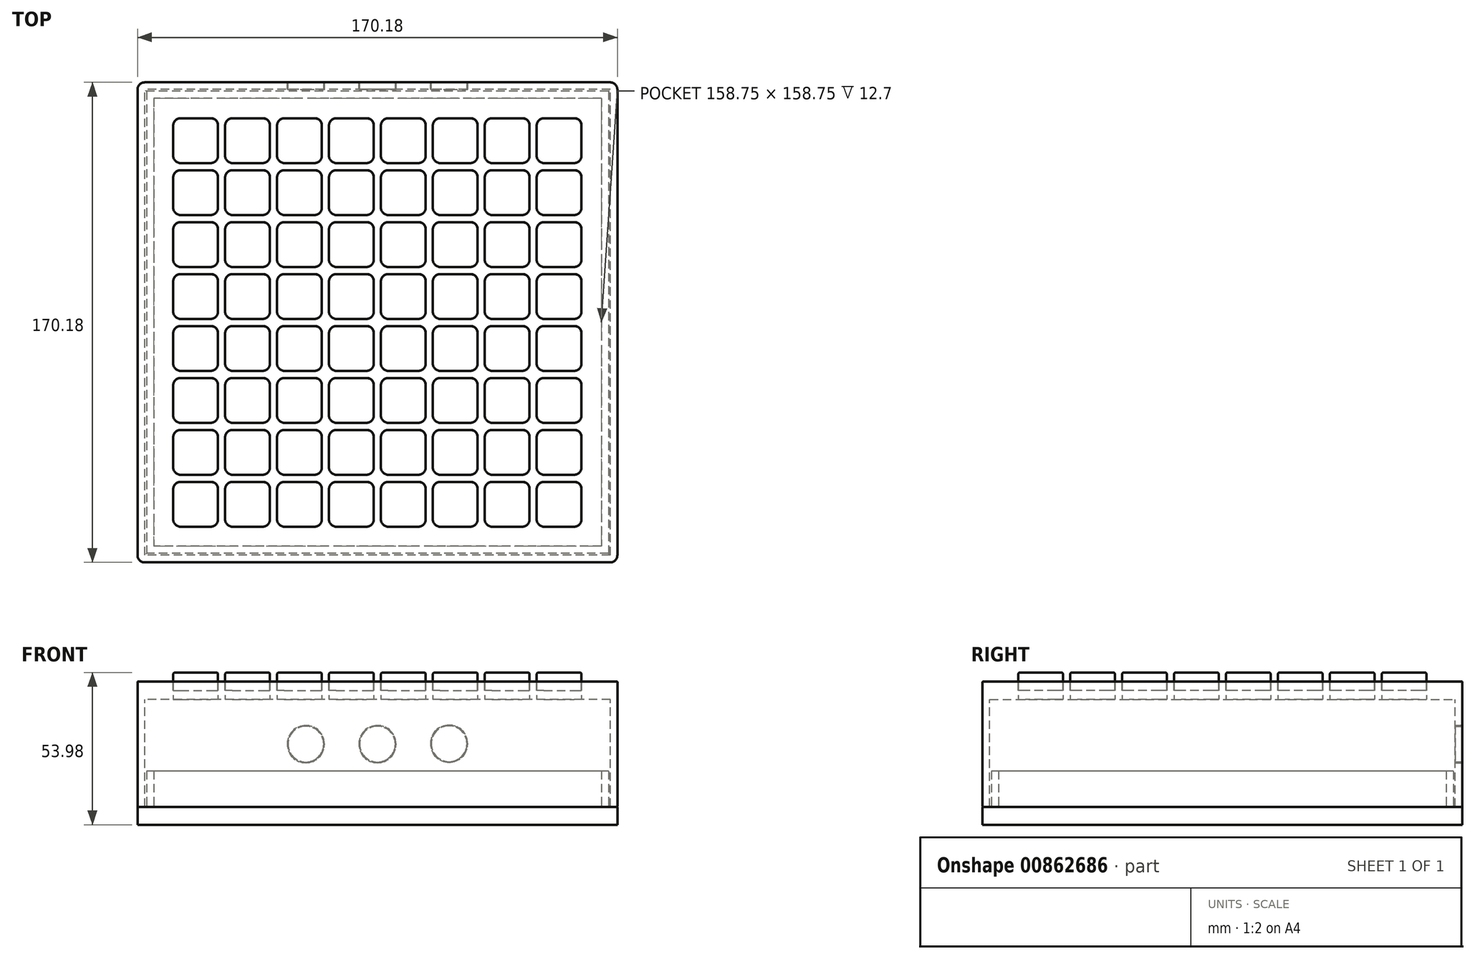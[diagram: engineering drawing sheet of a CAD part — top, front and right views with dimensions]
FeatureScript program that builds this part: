
annotation { "Feature Type Name" : "Feature", "Feature Type Description" : "" }
export const myFeature = defineFeature(function(context is Context, id is Id, definition is map)
    precondition{}
    {
        {
            var Q0;
            Q0=qCreatedBy(makeId("Top.planeOp"),FACE);
            var sketch = newSketch(context, id + "F0", { "sketchPlane" : qUnion([Q0])});
            skLineSegment(sketch, "E0.bottom", {"start": v(82.55, 85.1) * mm, "end": v(-82.55, 85.1) * mm});
            skLineSegment(sketch, "E0.top", {"start": v(82.55, -85.1) * mm, "end": v(-82.55, -85.1) * mm});
            skLineSegment(sketch, "E0.left", {"start": v(85.1, 82.55) * mm, "end": v(85.09, -82.55) * mm});
            skLineSegment(sketch, "E0.right", {"start": v(-85.1, 82.55) * mm, "end": v(-85.1, -82.55) * mm});
            skPoint(sketch, "E0.middle", {"position": v(0, 0) * mm});
            skPoint(sketch, "E1.visualSharp", {"position": v(-85.09, 85.1) * mm});
            skArc(sketch, "E1.filletArc", {"start": v(-82.55, 85.1) * mm, "mid": v(-84.35, 84.35) * mm, "end": v(-85.1, 82.55) * mm});
            skPoint(sketch, "E2.visualSharp", {"position": v(85.1, 85.1) * mm});
            skArc(sketch, "E2.filletArc", {"start": v(85.1, 82.55) * mm, "mid": v(84.35, 84.35) * mm, "end": v(82.55, 85.1) * mm});
            skPoint(sketch, "E3.visualSharp", {"position": v(85.09, -85.1) * mm});
            skArc(sketch, "E3.filletArc", {"start": v(82.55, -85.1) * mm, "mid": v(84.35, -84.35) * mm, "end": v(85.09, -82.55) * mm});
            skPoint(sketch, "E4.visualSharp", {"position": v(-85.1, -85.1) * mm});
            skArc(sketch, "E4.filletArc", {"start": v(-85.1, -82.55) * mm, "mid": v(-84.35, -84.35) * mm, "end": v(-82.55, -85.1) * mm});
            skLineSegment(sketch, "E5.bottom", {"start": v(-69.86, 72.38) * mm, "end": v(-59.07, 72.38) * mm});
            skLineSegment(sketch, "E5.top", {"start": v(-69.86, 56.5) * mm, "end": v(-59.07, 56.5) * mm});
            skLineSegment(sketch, "E5.left", {"start": v(-72.4, 69.84) * mm, "end": v(-72.4, 59.05) * mm});
            skLineSegment(sketch, "E5.right", {"start": v(-56.53, 69.84) * mm, "end": v(-56.53, 59.05) * mm});
            skPoint(sketch, "E6.visualSharp", {"position": v(-72.4, 72.38) * mm});
            skArc(sketch, "E6.filletArc", {"start": v(-69.86, 72.38) * mm, "mid": v(-71.66, 71.64) * mm, "end": v(-72.4, 69.84) * mm});
            skPoint(sketch, "E7.visualSharp", {"position": v(-56.53, 72.38) * mm});
            skArc(sketch, "E7.filletArc", {"start": v(-56.53, 69.84) * mm, "mid": v(-57.27, 71.64) * mm, "end": v(-59.07, 72.38) * mm});
            skPoint(sketch, "E8.visualSharp", {"position": v(-56.53, 56.5) * mm});
            skArc(sketch, "E8.filletArc", {"start": v(-59.07, 56.5) * mm, "mid": v(-57.27, 57.25) * mm, "end": v(-56.53, 59.05) * mm});
            skPoint(sketch, "E9.visualSharp", {"position": v(-72.4, 56.5) * mm});
            skArc(sketch, "E9.filletArc", {"start": v(-72.4, 59.05) * mm, "mid": v(-71.66, 57.25) * mm, "end": v(-69.86, 56.5) * mm});
            skLineSegment(sketch, "E10.0.1.0", {"start": v(-69.86, 53.97) * mm, "end": v(-59.07, 53.97) * mm});
            skArc(sketch, "E10.0.1.1", {"start": v(-56.53, 51.43) * mm, "mid": v(-57.27, 53.22) * mm, "end": v(-59.07, 53.97) * mm});
            skLineSegment(sketch, "E10.0.1.2", {"start": v(-56.53, 51.43) * mm, "end": v(-56.53, 40.63) * mm});
            skArc(sketch, "E10.0.1.3", {"start": v(-59.07, 38.1) * mm, "mid": v(-57.27, 38.84) * mm, "end": v(-56.53, 40.63) * mm});
            skLineSegment(sketch, "E10.0.1.4", {"start": v(-69.86, 38.1) * mm, "end": v(-59.07, 38.1) * mm});
            skArc(sketch, "E10.0.1.5", {"start": v(-72.4, 40.63) * mm, "mid": v(-71.66, 38.84) * mm, "end": v(-69.86, 38.1) * mm});
            skLineSegment(sketch, "E10.0.1.6", {"start": v(-72.4, 51.43) * mm, "end": v(-72.4, 40.63) * mm});
            skArc(sketch, "E10.0.1.7", {"start": v(-69.86, 53.97) * mm, "mid": v(-71.66, 53.22) * mm, "end": v(-72.4, 51.43) * mm});
            skLineSegment(sketch, "E10.0.2.0", {"start": v(-69.86, 35.55) * mm, "end": v(-59.07, 35.55) * mm});
            skArc(sketch, "E10.0.2.1", {"start": v(-56.53, 33.01) * mm, "mid": v(-57.27, 34.8) * mm, "end": v(-59.07, 35.55) * mm});
            skLineSegment(sketch, "E10.0.2.2", {"start": v(-56.53, 33.01) * mm, "end": v(-56.53, 22.22) * mm});
            skArc(sketch, "E10.0.2.3", {"start": v(-59.07, 19.68) * mm, "mid": v(-57.27, 20.42) * mm, "end": v(-56.53, 22.22) * mm});
            skLineSegment(sketch, "E10.0.2.4", {"start": v(-69.86, 19.68) * mm, "end": v(-59.07, 19.68) * mm});
            skArc(sketch, "E10.0.2.5", {"start": v(-72.4, 22.22) * mm, "mid": v(-71.66, 20.42) * mm, "end": v(-69.86, 19.68) * mm});
            skLineSegment(sketch, "E10.0.2.6", {"start": v(-72.4, 33.01) * mm, "end": v(-72.4, 22.22) * mm});
            skArc(sketch, "E10.0.2.7", {"start": v(-69.86, 35.55) * mm, "mid": v(-71.66, 34.8) * mm, "end": v(-72.4, 33.01) * mm});
            skLineSegment(sketch, "E10.0.3.0", {"start": v(-69.86, 17.14) * mm, "end": v(-59.07, 17.14) * mm});
            skArc(sketch, "E10.0.3.1", {"start": v(-56.53, 14.6) * mm, "mid": v(-57.27, 16.4) * mm, "end": v(-59.07, 17.14) * mm});
            skLineSegment(sketch, "E10.0.3.2", {"start": v(-56.53, 14.6) * mm, "end": v(-56.53, 3.8) * mm});
            skArc(sketch, "E10.0.3.3", {"start": v(-59.07, 1.26) * mm, "mid": v(-57.27, 2) * mm, "end": v(-56.53, 3.8) * mm});
            skLineSegment(sketch, "E10.0.3.4", {"start": v(-69.86, 1.26) * mm, "end": v(-59.07, 1.26) * mm});
            skArc(sketch, "E10.0.3.5", {"start": v(-72.4, 3.8) * mm, "mid": v(-71.66, 2) * mm, "end": v(-69.86, 1.26) * mm});
            skLineSegment(sketch, "E10.0.3.6", {"start": v(-72.4, 14.6) * mm, "end": v(-72.4, 3.8) * mm});
            skArc(sketch, "E10.0.3.7", {"start": v(-69.86, 17.14) * mm, "mid": v(-71.66, 16.4) * mm, "end": v(-72.4, 14.6) * mm});
            skLineSegment(sketch, "E10.0.4.0", {"start": v(-69.86, -1.28) * mm, "end": v(-59.07, -1.28) * mm});
            skArc(sketch, "E10.0.4.1", {"start": v(-56.53, -3.82) * mm, "mid": v(-57.27, -2.02) * mm, "end": v(-59.07, -1.28) * mm});
            skLineSegment(sketch, "E10.0.4.2", {"start": v(-56.53, -3.82) * mm, "end": v(-56.53, -14.61) * mm});
            skArc(sketch, "E10.0.4.3", {"start": v(-59.07, -17.15) * mm, "mid": v(-57.27, -16.4) * mm, "end": v(-56.53, -14.61) * mm});
            skLineSegment(sketch, "E10.0.4.4", {"start": v(-69.86, -17.15) * mm, "end": v(-59.07, -17.15) * mm});
            skArc(sketch, "E10.0.4.5", {"start": v(-72.4, -14.61) * mm, "mid": v(-71.66, -16.4) * mm, "end": v(-69.86, -17.15) * mm});
            skLineSegment(sketch, "E10.0.4.6", {"start": v(-72.4, -3.82) * mm, "end": v(-72.4, -14.61) * mm});
            skArc(sketch, "E10.0.4.7", {"start": v(-69.86, -1.28) * mm, "mid": v(-71.66, -2.02) * mm, "end": v(-72.4, -3.82) * mm});
            skLineSegment(sketch, "E10.0.5.0", {"start": v(-69.86, -19.7) * mm, "end": v(-59.07, -19.7) * mm});
            skArc(sketch, "E10.0.5.1", {"start": v(-56.53, -22.23) * mm, "mid": v(-57.27, -20.44) * mm, "end": v(-59.07, -19.7) * mm});
            skLineSegment(sketch, "E10.0.5.2", {"start": v(-56.53, -22.23) * mm, "end": v(-56.53, -33.03) * mm});
            skArc(sketch, "E10.0.5.3", {"start": v(-59.07, -35.57) * mm, "mid": v(-57.27, -34.82) * mm, "end": v(-56.53, -33.03) * mm});
            skLineSegment(sketch, "E10.0.5.4", {"start": v(-69.86, -35.57) * mm, "end": v(-59.07, -35.57) * mm});
            skArc(sketch, "E10.0.5.5", {"start": v(-72.4, -33.03) * mm, "mid": v(-71.66, -34.82) * mm, "end": v(-69.86, -35.57) * mm});
            skLineSegment(sketch, "E10.0.5.6", {"start": v(-72.4, -22.23) * mm, "end": v(-72.4, -33.03) * mm});
            skArc(sketch, "E10.0.5.7", {"start": v(-69.86, -19.7) * mm, "mid": v(-71.66, -20.44) * mm, "end": v(-72.4, -22.23) * mm});
            skLineSegment(sketch, "E10.0.6.0", {"start": v(-69.86, -38.1) * mm, "end": v(-59.07, -38.1) * mm});
            skArc(sketch, "E10.0.6.1", {"start": v(-56.53, -40.65) * mm, "mid": v(-57.27, -38.85) * mm, "end": v(-59.07, -38.1) * mm});
            skLineSegment(sketch, "E10.0.6.2", {"start": v(-56.53, -40.65) * mm, "end": v(-56.53, -51.44) * mm});
            skArc(sketch, "E10.0.6.3", {"start": v(-59.07, -53.98) * mm, "mid": v(-57.27, -53.24) * mm, "end": v(-56.53, -51.44) * mm});
            skLineSegment(sketch, "E10.0.6.4", {"start": v(-69.86, -53.98) * mm, "end": v(-59.07, -53.98) * mm});
            skArc(sketch, "E10.0.6.5", {"start": v(-72.4, -51.44) * mm, "mid": v(-71.66, -53.24) * mm, "end": v(-69.86, -53.98) * mm});
            skLineSegment(sketch, "E10.0.6.6", {"start": v(-72.4, -40.65) * mm, "end": v(-72.4, -51.44) * mm});
            skArc(sketch, "E10.0.6.7", {"start": v(-69.86, -38.1) * mm, "mid": v(-71.66, -38.85) * mm, "end": v(-72.4, -40.65) * mm});
            skLineSegment(sketch, "E10.0.7.0", {"start": v(-69.86, -56.52) * mm, "end": v(-59.07, -56.52) * mm});
            skArc(sketch, "E10.0.7.1", {"start": v(-56.53, -59.06) * mm, "mid": v(-57.27, -57.27) * mm, "end": v(-59.07, -56.52) * mm});
            skLineSegment(sketch, "E10.0.7.2", {"start": v(-56.53, -59.06) * mm, "end": v(-56.53, -69.86) * mm});
            skArc(sketch, "E10.0.7.3", {"start": v(-59.07, -72.4) * mm, "mid": v(-57.27, -71.65) * mm, "end": v(-56.53, -69.86) * mm});
            skLineSegment(sketch, "E10.0.7.4", {"start": v(-69.86, -72.4) * mm, "end": v(-59.07, -72.4) * mm});
            skArc(sketch, "E10.0.7.5", {"start": v(-72.4, -69.86) * mm, "mid": v(-71.66, -71.65) * mm, "end": v(-69.86, -72.4) * mm});
            skLineSegment(sketch, "E10.0.7.6", {"start": v(-72.4, -59.06) * mm, "end": v(-72.4, -69.86) * mm});
            skArc(sketch, "E10.0.7.7", {"start": v(-69.86, -56.52) * mm, "mid": v(-71.66, -57.27) * mm, "end": v(-72.4, -59.06) * mm});
            skLineSegment(sketch, "E10.1.0.0", {"start": v(-51.45, 72.38) * mm, "end": v(-40.65, 72.38) * mm});
            skArc(sketch, "E10.1.0.1", {"start": v(-38.11, 69.84) * mm, "mid": v(-38.85, 71.64) * mm, "end": v(-40.65, 72.38) * mm});
            skLineSegment(sketch, "E10.1.0.2", {"start": v(-38.11, 69.84) * mm, "end": v(-38.11, 59.05) * mm});
            skArc(sketch, "E10.1.0.3", {"start": v(-40.65, 56.5) * mm, "mid": v(-38.85, 57.25) * mm, "end": v(-38.11, 59.05) * mm});
            skLineSegment(sketch, "E10.1.0.4", {"start": v(-51.45, 56.5) * mm, "end": v(-40.65, 56.5) * mm});
            skArc(sketch, "E10.1.0.5", {"start": v(-53.99, 59.05) * mm, "mid": v(-53.24, 57.25) * mm, "end": v(-51.45, 56.5) * mm});
            skLineSegment(sketch, "E10.1.0.6", {"start": v(-53.99, 69.84) * mm, "end": v(-53.99, 59.05) * mm});
            skArc(sketch, "E10.1.0.7", {"start": v(-51.45, 72.38) * mm, "mid": v(-53.24, 71.64) * mm, "end": v(-53.99, 69.84) * mm});
            skLineSegment(sketch, "E10.1.1.0", {"start": v(-51.45, 53.97) * mm, "end": v(-40.65, 53.97) * mm});
            skArc(sketch, "E10.1.1.1", {"start": v(-38.11, 51.43) * mm, "mid": v(-38.85, 53.22) * mm, "end": v(-40.65, 53.97) * mm});
            skLineSegment(sketch, "E10.1.1.2", {"start": v(-38.11, 51.43) * mm, "end": v(-38.11, 40.63) * mm});
            skArc(sketch, "E10.1.1.3", {"start": v(-40.65, 38.1) * mm, "mid": v(-38.85, 38.84) * mm, "end": v(-38.11, 40.63) * mm});
            skLineSegment(sketch, "E10.1.1.4", {"start": v(-51.45, 38.1) * mm, "end": v(-40.65, 38.1) * mm});
            skArc(sketch, "E10.1.1.5", {"start": v(-53.99, 40.63) * mm, "mid": v(-53.24, 38.84) * mm, "end": v(-51.45, 38.1) * mm});
            skLineSegment(sketch, "E10.1.1.6", {"start": v(-53.99, 51.43) * mm, "end": v(-53.99, 40.63) * mm});
            skArc(sketch, "E10.1.1.7", {"start": v(-51.45, 53.97) * mm, "mid": v(-53.24, 53.22) * mm, "end": v(-53.99, 51.43) * mm});
            skLineSegment(sketch, "E10.1.2.0", {"start": v(-51.45, 35.55) * mm, "end": v(-40.65, 35.55) * mm});
            skArc(sketch, "E10.1.2.1", {"start": v(-38.11, 33.01) * mm, "mid": v(-38.85, 34.8) * mm, "end": v(-40.65, 35.55) * mm});
            skLineSegment(sketch, "E10.1.2.2", {"start": v(-38.11, 33.01) * mm, "end": v(-38.11, 22.22) * mm});
            skArc(sketch, "E10.1.2.3", {"start": v(-40.65, 19.68) * mm, "mid": v(-38.85, 20.42) * mm, "end": v(-38.11, 22.22) * mm});
            skLineSegment(sketch, "E10.1.2.4", {"start": v(-51.45, 19.68) * mm, "end": v(-40.65, 19.68) * mm});
            skArc(sketch, "E10.1.2.5", {"start": v(-53.99, 22.22) * mm, "mid": v(-53.24, 20.42) * mm, "end": v(-51.45, 19.68) * mm});
            skLineSegment(sketch, "E10.1.2.6", {"start": v(-53.99, 33.01) * mm, "end": v(-53.99, 22.22) * mm});
            skArc(sketch, "E10.1.2.7", {"start": v(-51.45, 35.55) * mm, "mid": v(-53.24, 34.8) * mm, "end": v(-53.99, 33.01) * mm});
            skLineSegment(sketch, "E10.1.3.0", {"start": v(-51.45, 17.14) * mm, "end": v(-40.65, 17.14) * mm});
            skArc(sketch, "E10.1.3.1", {"start": v(-38.11, 14.6) * mm, "mid": v(-38.85, 16.4) * mm, "end": v(-40.65, 17.14) * mm});
            skLineSegment(sketch, "E10.1.3.2", {"start": v(-38.11, 14.6) * mm, "end": v(-38.11, 3.8) * mm});
            skArc(sketch, "E10.1.3.3", {"start": v(-40.65, 1.26) * mm, "mid": v(-38.85, 2) * mm, "end": v(-38.11, 3.8) * mm});
            skLineSegment(sketch, "E10.1.3.4", {"start": v(-51.45, 1.26) * mm, "end": v(-40.65, 1.26) * mm});
            skArc(sketch, "E10.1.3.5", {"start": v(-53.99, 3.8) * mm, "mid": v(-53.24, 2) * mm, "end": v(-51.45, 1.26) * mm});
            skLineSegment(sketch, "E10.1.3.6", {"start": v(-53.99, 14.6) * mm, "end": v(-53.99, 3.8) * mm});
            skArc(sketch, "E10.1.3.7", {"start": v(-51.45, 17.14) * mm, "mid": v(-53.24, 16.4) * mm, "end": v(-53.99, 14.6) * mm});
            skLineSegment(sketch, "E10.1.4.0", {"start": v(-51.45, -1.28) * mm, "end": v(-40.65, -1.28) * mm});
            skArc(sketch, "E10.1.4.1", {"start": v(-38.11, -3.82) * mm, "mid": v(-38.85, -2.02) * mm, "end": v(-40.65, -1.28) * mm});
            skLineSegment(sketch, "E10.1.4.2", {"start": v(-38.11, -3.82) * mm, "end": v(-38.11, -14.61) * mm});
            skArc(sketch, "E10.1.4.3", {"start": v(-40.65, -17.15) * mm, "mid": v(-38.85, -16.4) * mm, "end": v(-38.11, -14.61) * mm});
            skLineSegment(sketch, "E10.1.4.4", {"start": v(-51.45, -17.15) * mm, "end": v(-40.65, -17.15) * mm});
            skArc(sketch, "E10.1.4.5", {"start": v(-53.99, -14.61) * mm, "mid": v(-53.24, -16.4) * mm, "end": v(-51.45, -17.15) * mm});
            skLineSegment(sketch, "E10.1.4.6", {"start": v(-53.99, -3.82) * mm, "end": v(-53.99, -14.61) * mm});
            skArc(sketch, "E10.1.4.7", {"start": v(-51.45, -1.28) * mm, "mid": v(-53.24, -2.02) * mm, "end": v(-53.99, -3.82) * mm});
            skLineSegment(sketch, "E10.1.5.0", {"start": v(-51.45, -19.7) * mm, "end": v(-40.65, -19.7) * mm});
            skArc(sketch, "E10.1.5.1", {"start": v(-38.11, -22.23) * mm, "mid": v(-38.85, -20.44) * mm, "end": v(-40.65, -19.7) * mm});
            skLineSegment(sketch, "E10.1.5.2", {"start": v(-38.11, -22.23) * mm, "end": v(-38.11, -33.03) * mm});
            skArc(sketch, "E10.1.5.3", {"start": v(-40.65, -35.57) * mm, "mid": v(-38.85, -34.82) * mm, "end": v(-38.11, -33.03) * mm});
            skLineSegment(sketch, "E10.1.5.4", {"start": v(-51.45, -35.57) * mm, "end": v(-40.65, -35.57) * mm});
            skArc(sketch, "E10.1.5.5", {"start": v(-53.99, -33.03) * mm, "mid": v(-53.24, -34.82) * mm, "end": v(-51.45, -35.57) * mm});
            skLineSegment(sketch, "E10.1.5.6", {"start": v(-53.99, -22.23) * mm, "end": v(-53.99, -33.03) * mm});
            skArc(sketch, "E10.1.5.7", {"start": v(-51.45, -19.7) * mm, "mid": v(-53.24, -20.44) * mm, "end": v(-53.99, -22.23) * mm});
            skLineSegment(sketch, "E10.1.6.0", {"start": v(-51.45, -38.1) * mm, "end": v(-40.65, -38.1) * mm});
            skArc(sketch, "E10.1.6.1", {"start": v(-38.11, -40.65) * mm, "mid": v(-38.85, -38.85) * mm, "end": v(-40.65, -38.1) * mm});
            skLineSegment(sketch, "E10.1.6.2", {"start": v(-38.11, -40.65) * mm, "end": v(-38.11, -51.44) * mm});
            skArc(sketch, "E10.1.6.3", {"start": v(-40.65, -53.98) * mm, "mid": v(-38.85, -53.24) * mm, "end": v(-38.11, -51.44) * mm});
            skLineSegment(sketch, "E10.1.6.4", {"start": v(-51.45, -53.98) * mm, "end": v(-40.65, -53.98) * mm});
            skArc(sketch, "E10.1.6.5", {"start": v(-53.99, -51.44) * mm, "mid": v(-53.24, -53.24) * mm, "end": v(-51.45, -53.98) * mm});
            skLineSegment(sketch, "E10.1.6.6", {"start": v(-53.99, -40.65) * mm, "end": v(-53.99, -51.44) * mm});
            skArc(sketch, "E10.1.6.7", {"start": v(-51.45, -38.1) * mm, "mid": v(-53.24, -38.85) * mm, "end": v(-53.99, -40.65) * mm});
            skLineSegment(sketch, "E10.1.7.0", {"start": v(-51.45, -56.52) * mm, "end": v(-40.65, -56.52) * mm});
            skArc(sketch, "E10.1.7.1", {"start": v(-38.11, -59.06) * mm, "mid": v(-38.85, -57.27) * mm, "end": v(-40.65, -56.52) * mm});
            skLineSegment(sketch, "E10.1.7.2", {"start": v(-38.11, -59.06) * mm, "end": v(-38.11, -69.86) * mm});
            skArc(sketch, "E10.1.7.3", {"start": v(-40.65, -72.4) * mm, "mid": v(-38.85, -71.65) * mm, "end": v(-38.11, -69.86) * mm});
            skLineSegment(sketch, "E10.1.7.4", {"start": v(-51.45, -72.4) * mm, "end": v(-40.65, -72.4) * mm});
            skArc(sketch, "E10.1.7.5", {"start": v(-53.99, -69.86) * mm, "mid": v(-53.24, -71.65) * mm, "end": v(-51.45, -72.4) * mm});
            skLineSegment(sketch, "E10.1.7.6", {"start": v(-53.99, -59.06) * mm, "end": v(-53.99, -69.86) * mm});
            skArc(sketch, "E10.1.7.7", {"start": v(-51.45, -56.52) * mm, "mid": v(-53.24, -57.27) * mm, "end": v(-53.99, -59.06) * mm});
            skLineSegment(sketch, "E10.2.0.0", {"start": v(-33.03, 72.38) * mm, "end": v(-22.24, 72.38) * mm});
            skArc(sketch, "E10.2.0.1", {"start": v(-19.7, 69.84) * mm, "mid": v(-20.44, 71.64) * mm, "end": v(-22.24, 72.38) * mm});
            skLineSegment(sketch, "E10.2.0.2", {"start": v(-19.7, 69.84) * mm, "end": v(-19.7, 59.05) * mm});
            skArc(sketch, "E10.2.0.3", {"start": v(-22.24, 56.5) * mm, "mid": v(-20.44, 57.25) * mm, "end": v(-19.7, 59.05) * mm});
            skLineSegment(sketch, "E10.2.0.4", {"start": v(-33.03, 56.5) * mm, "end": v(-22.24, 56.5) * mm});
            skArc(sketch, "E10.2.0.5", {"start": v(-35.57, 59.05) * mm, "mid": v(-34.83, 57.25) * mm, "end": v(-33.03, 56.5) * mm});
            skLineSegment(sketch, "E10.2.0.6", {"start": v(-35.57, 69.84) * mm, "end": v(-35.57, 59.05) * mm});
            skArc(sketch, "E10.2.0.7", {"start": v(-33.03, 72.38) * mm, "mid": v(-34.83, 71.64) * mm, "end": v(-35.57, 69.84) * mm});
            skLineSegment(sketch, "E10.2.1.0", {"start": v(-33.03, 53.97) * mm, "end": v(-22.24, 53.97) * mm});
            skArc(sketch, "E10.2.1.1", {"start": v(-19.7, 51.43) * mm, "mid": v(-20.44, 53.22) * mm, "end": v(-22.24, 53.97) * mm});
            skLineSegment(sketch, "E10.2.1.2", {"start": v(-19.7, 51.43) * mm, "end": v(-19.7, 40.63) * mm});
            skArc(sketch, "E10.2.1.3", {"start": v(-22.24, 38.1) * mm, "mid": v(-20.44, 38.84) * mm, "end": v(-19.7, 40.63) * mm});
            skLineSegment(sketch, "E10.2.1.4", {"start": v(-33.03, 38.1) * mm, "end": v(-22.24, 38.1) * mm});
            skArc(sketch, "E10.2.1.5", {"start": v(-35.57, 40.63) * mm, "mid": v(-34.83, 38.84) * mm, "end": v(-33.03, 38.1) * mm});
            skLineSegment(sketch, "E10.2.1.6", {"start": v(-35.57, 51.43) * mm, "end": v(-35.57, 40.63) * mm});
            skArc(sketch, "E10.2.1.7", {"start": v(-33.03, 53.97) * mm, "mid": v(-34.83, 53.22) * mm, "end": v(-35.57, 51.43) * mm});
            skLineSegment(sketch, "E10.2.2.0", {"start": v(-33.03, 35.55) * mm, "end": v(-22.24, 35.55) * mm});
            skArc(sketch, "E10.2.2.1", {"start": v(-19.7, 33.01) * mm, "mid": v(-20.44, 34.8) * mm, "end": v(-22.24, 35.55) * mm});
            skLineSegment(sketch, "E10.2.2.2", {"start": v(-19.7, 33.01) * mm, "end": v(-19.7, 22.22) * mm});
            skArc(sketch, "E10.2.2.3", {"start": v(-22.24, 19.68) * mm, "mid": v(-20.44, 20.42) * mm, "end": v(-19.7, 22.22) * mm});
            skLineSegment(sketch, "E10.2.2.4", {"start": v(-33.03, 19.68) * mm, "end": v(-22.24, 19.68) * mm});
            skArc(sketch, "E10.2.2.5", {"start": v(-35.57, 22.22) * mm, "mid": v(-34.83, 20.42) * mm, "end": v(-33.03, 19.68) * mm});
            skLineSegment(sketch, "E10.2.2.6", {"start": v(-35.57, 33.01) * mm, "end": v(-35.57, 22.22) * mm});
            skArc(sketch, "E10.2.2.7", {"start": v(-33.03, 35.55) * mm, "mid": v(-34.83, 34.8) * mm, "end": v(-35.57, 33.01) * mm});
            skLineSegment(sketch, "E10.2.3.0", {"start": v(-33.03, 17.14) * mm, "end": v(-22.24, 17.14) * mm});
            skArc(sketch, "E10.2.3.1", {"start": v(-19.7, 14.6) * mm, "mid": v(-20.44, 16.4) * mm, "end": v(-22.24, 17.14) * mm});
            skLineSegment(sketch, "E10.2.3.2", {"start": v(-19.7, 14.6) * mm, "end": v(-19.7, 3.8) * mm});
            skArc(sketch, "E10.2.3.3", {"start": v(-22.24, 1.26) * mm, "mid": v(-20.44, 2) * mm, "end": v(-19.7, 3.8) * mm});
            skLineSegment(sketch, "E10.2.3.4", {"start": v(-33.03, 1.26) * mm, "end": v(-22.24, 1.26) * mm});
            skArc(sketch, "E10.2.3.5", {"start": v(-35.57, 3.8) * mm, "mid": v(-34.83, 2) * mm, "end": v(-33.03, 1.26) * mm});
            skLineSegment(sketch, "E10.2.3.6", {"start": v(-35.57, 14.6) * mm, "end": v(-35.57, 3.8) * mm});
            skArc(sketch, "E10.2.3.7", {"start": v(-33.03, 17.14) * mm, "mid": v(-34.83, 16.4) * mm, "end": v(-35.57, 14.6) * mm});
            skLineSegment(sketch, "E10.2.4.0", {"start": v(-33.03, -1.28) * mm, "end": v(-22.24, -1.28) * mm});
            skArc(sketch, "E10.2.4.1", {"start": v(-19.7, -3.82) * mm, "mid": v(-20.44, -2.02) * mm, "end": v(-22.24, -1.28) * mm});
            skLineSegment(sketch, "E10.2.4.2", {"start": v(-19.7, -3.82) * mm, "end": v(-19.7, -14.61) * mm});
            skArc(sketch, "E10.2.4.3", {"start": v(-22.24, -17.15) * mm, "mid": v(-20.44, -16.4) * mm, "end": v(-19.7, -14.61) * mm});
            skLineSegment(sketch, "E10.2.4.4", {"start": v(-33.03, -17.15) * mm, "end": v(-22.24, -17.15) * mm});
            skArc(sketch, "E10.2.4.5", {"start": v(-35.57, -14.61) * mm, "mid": v(-34.83, -16.4) * mm, "end": v(-33.03, -17.15) * mm});
            skLineSegment(sketch, "E10.2.4.6", {"start": v(-35.57, -3.82) * mm, "end": v(-35.57, -14.61) * mm});
            skArc(sketch, "E10.2.4.7", {"start": v(-33.03, -1.28) * mm, "mid": v(-34.83, -2.02) * mm, "end": v(-35.57, -3.82) * mm});
            skLineSegment(sketch, "E10.2.5.0", {"start": v(-33.03, -19.7) * mm, "end": v(-22.24, -19.7) * mm});
            skArc(sketch, "E10.2.5.1", {"start": v(-19.7, -22.23) * mm, "mid": v(-20.44, -20.44) * mm, "end": v(-22.24, -19.7) * mm});
            skLineSegment(sketch, "E10.2.5.2", {"start": v(-19.7, -22.23) * mm, "end": v(-19.7, -33.03) * mm});
            skArc(sketch, "E10.2.5.3", {"start": v(-22.24, -35.57) * mm, "mid": v(-20.44, -34.82) * mm, "end": v(-19.7, -33.03) * mm});
            skLineSegment(sketch, "E10.2.5.4", {"start": v(-33.03, -35.57) * mm, "end": v(-22.24, -35.57) * mm});
            skArc(sketch, "E10.2.5.5", {"start": v(-35.57, -33.03) * mm, "mid": v(-34.83, -34.82) * mm, "end": v(-33.03, -35.57) * mm});
            skLineSegment(sketch, "E10.2.5.6", {"start": v(-35.57, -22.23) * mm, "end": v(-35.57, -33.03) * mm});
            skArc(sketch, "E10.2.5.7", {"start": v(-33.03, -19.7) * mm, "mid": v(-34.83, -20.44) * mm, "end": v(-35.57, -22.23) * mm});
            skLineSegment(sketch, "E10.2.6.0", {"start": v(-33.03, -38.1) * mm, "end": v(-22.24, -38.1) * mm});
            skArc(sketch, "E10.2.6.1", {"start": v(-19.7, -40.65) * mm, "mid": v(-20.44, -38.85) * mm, "end": v(-22.24, -38.1) * mm});
            skLineSegment(sketch, "E10.2.6.2", {"start": v(-19.7, -40.65) * mm, "end": v(-19.7, -51.44) * mm});
            skArc(sketch, "E10.2.6.3", {"start": v(-22.24, -53.98) * mm, "mid": v(-20.44, -53.24) * mm, "end": v(-19.7, -51.44) * mm});
            skLineSegment(sketch, "E10.2.6.4", {"start": v(-33.03, -53.98) * mm, "end": v(-22.24, -53.98) * mm});
            skArc(sketch, "E10.2.6.5", {"start": v(-35.57, -51.44) * mm, "mid": v(-34.83, -53.24) * mm, "end": v(-33.03, -53.98) * mm});
            skLineSegment(sketch, "E10.2.6.6", {"start": v(-35.57, -40.65) * mm, "end": v(-35.57, -51.44) * mm});
            skArc(sketch, "E10.2.6.7", {"start": v(-33.03, -38.1) * mm, "mid": v(-34.83, -38.85) * mm, "end": v(-35.57, -40.65) * mm});
            skLineSegment(sketch, "E10.2.7.0", {"start": v(-33.03, -56.52) * mm, "end": v(-22.24, -56.52) * mm});
            skArc(sketch, "E10.2.7.1", {"start": v(-19.7, -59.06) * mm, "mid": v(-20.44, -57.27) * mm, "end": v(-22.24, -56.52) * mm});
            skLineSegment(sketch, "E10.2.7.2", {"start": v(-19.7, -59.06) * mm, "end": v(-19.7, -69.86) * mm});
            skArc(sketch, "E10.2.7.3", {"start": v(-22.24, -72.4) * mm, "mid": v(-20.44, -71.65) * mm, "end": v(-19.7, -69.86) * mm});
            skLineSegment(sketch, "E10.2.7.4", {"start": v(-33.03, -72.4) * mm, "end": v(-22.24, -72.4) * mm});
            skArc(sketch, "E10.2.7.5", {"start": v(-35.57, -69.86) * mm, "mid": v(-34.83, -71.65) * mm, "end": v(-33.03, -72.4) * mm});
            skLineSegment(sketch, "E10.2.7.6", {"start": v(-35.57, -59.06) * mm, "end": v(-35.57, -69.86) * mm});
            skArc(sketch, "E10.2.7.7", {"start": v(-33.03, -56.52) * mm, "mid": v(-34.83, -57.27) * mm, "end": v(-35.57, -59.06) * mm});
            skLineSegment(sketch, "E10.3.0.0", {"start": v(-14.62, 72.38) * mm, "end": v(-3.82, 72.38) * mm});
            skArc(sketch, "E10.3.0.1", {"start": v(-1.28, 69.84) * mm, "mid": v(-2.02, 71.64) * mm, "end": v(-3.82, 72.38) * mm});
            skLineSegment(sketch, "E10.3.0.2", {"start": v(-1.28, 69.84) * mm, "end": v(-1.28, 59.05) * mm});
            skArc(sketch, "E10.3.0.3", {"start": v(-3.82, 56.5) * mm, "mid": v(-2.02, 57.25) * mm, "end": v(-1.28, 59.05) * mm});
            skLineSegment(sketch, "E10.3.0.4", {"start": v(-14.62, 56.5) * mm, "end": v(-3.82, 56.5) * mm});
            skArc(sketch, "E10.3.0.5", {"start": v(-17.16, 59.05) * mm, "mid": v(-16.41, 57.25) * mm, "end": v(-14.62, 56.5) * mm});
            skLineSegment(sketch, "E10.3.0.6", {"start": v(-17.16, 69.84) * mm, "end": v(-17.16, 59.05) * mm});
            skArc(sketch, "E10.3.0.7", {"start": v(-14.62, 72.38) * mm, "mid": v(-16.41, 71.64) * mm, "end": v(-17.16, 69.84) * mm});
            skLineSegment(sketch, "E10.3.1.0", {"start": v(-14.62, 53.97) * mm, "end": v(-3.82, 53.97) * mm});
            skArc(sketch, "E10.3.1.1", {"start": v(-1.28, 51.43) * mm, "mid": v(-2.02, 53.22) * mm, "end": v(-3.82, 53.97) * mm});
            skLineSegment(sketch, "E10.3.1.2", {"start": v(-1.28, 51.43) * mm, "end": v(-1.28, 40.63) * mm});
            skArc(sketch, "E10.3.1.3", {"start": v(-3.82, 38.1) * mm, "mid": v(-2.02, 38.84) * mm, "end": v(-1.28, 40.63) * mm});
            skLineSegment(sketch, "E10.3.1.4", {"start": v(-14.62, 38.1) * mm, "end": v(-3.82, 38.1) * mm});
            skArc(sketch, "E10.3.1.5", {"start": v(-17.16, 40.63) * mm, "mid": v(-16.41, 38.84) * mm, "end": v(-14.62, 38.1) * mm});
            skLineSegment(sketch, "E10.3.1.6", {"start": v(-17.16, 51.43) * mm, "end": v(-17.16, 40.63) * mm});
            skArc(sketch, "E10.3.1.7", {"start": v(-14.62, 53.97) * mm, "mid": v(-16.41, 53.22) * mm, "end": v(-17.16, 51.43) * mm});
            skLineSegment(sketch, "E10.3.2.0", {"start": v(-14.62, 35.55) * mm, "end": v(-3.82, 35.55) * mm});
            skArc(sketch, "E10.3.2.1", {"start": v(-1.28, 33.01) * mm, "mid": v(-2.02, 34.8) * mm, "end": v(-3.82, 35.55) * mm});
            skLineSegment(sketch, "E10.3.2.2", {"start": v(-1.28, 33.01) * mm, "end": v(-1.28, 22.22) * mm});
            skArc(sketch, "E10.3.2.3", {"start": v(-3.82, 19.68) * mm, "mid": v(-2.02, 20.42) * mm, "end": v(-1.28, 22.22) * mm});
            skLineSegment(sketch, "E10.3.2.4", {"start": v(-14.62, 19.68) * mm, "end": v(-3.82, 19.68) * mm});
            skArc(sketch, "E10.3.2.5", {"start": v(-17.16, 22.22) * mm, "mid": v(-16.41, 20.42) * mm, "end": v(-14.62, 19.68) * mm});
            skLineSegment(sketch, "E10.3.2.6", {"start": v(-17.16, 33.01) * mm, "end": v(-17.16, 22.22) * mm});
            skArc(sketch, "E10.3.2.7", {"start": v(-14.62, 35.55) * mm, "mid": v(-16.41, 34.8) * mm, "end": v(-17.16, 33.01) * mm});
            skLineSegment(sketch, "E10.3.3.0", {"start": v(-14.62, 17.14) * mm, "end": v(-3.82, 17.14) * mm});
            skArc(sketch, "E10.3.3.1", {"start": v(-1.28, 14.6) * mm, "mid": v(-2.02, 16.4) * mm, "end": v(-3.82, 17.14) * mm});
            skLineSegment(sketch, "E10.3.3.2", {"start": v(-1.28, 14.6) * mm, "end": v(-1.28, 3.8) * mm});
            skArc(sketch, "E10.3.3.3", {"start": v(-3.82, 1.26) * mm, "mid": v(-2.02, 2) * mm, "end": v(-1.28, 3.8) * mm});
            skLineSegment(sketch, "E10.3.3.4", {"start": v(-14.62, 1.26) * mm, "end": v(-3.82, 1.26) * mm});
            skArc(sketch, "E10.3.3.5", {"start": v(-17.16, 3.8) * mm, "mid": v(-16.41, 2) * mm, "end": v(-14.62, 1.26) * mm});
            skLineSegment(sketch, "E10.3.3.6", {"start": v(-17.16, 14.6) * mm, "end": v(-17.16, 3.8) * mm});
            skArc(sketch, "E10.3.3.7", {"start": v(-14.62, 17.14) * mm, "mid": v(-16.41, 16.4) * mm, "end": v(-17.16, 14.6) * mm});
            skLineSegment(sketch, "E10.3.4.0", {"start": v(-14.62, -1.28) * mm, "end": v(-3.82, -1.28) * mm});
            skArc(sketch, "E10.3.4.1", {"start": v(-1.28, -3.82) * mm, "mid": v(-2.02, -2.02) * mm, "end": v(-3.82, -1.28) * mm});
            skLineSegment(sketch, "E10.3.4.2", {"start": v(-1.28, -3.82) * mm, "end": v(-1.28, -14.61) * mm});
            skArc(sketch, "E10.3.4.3", {"start": v(-3.82, -17.15) * mm, "mid": v(-2.02, -16.4) * mm, "end": v(-1.28, -14.61) * mm});
            skLineSegment(sketch, "E10.3.4.4", {"start": v(-14.62, -17.15) * mm, "end": v(-3.82, -17.15) * mm});
            skArc(sketch, "E10.3.4.5", {"start": v(-17.16, -14.61) * mm, "mid": v(-16.41, -16.4) * mm, "end": v(-14.62, -17.15) * mm});
            skLineSegment(sketch, "E10.3.4.6", {"start": v(-17.16, -3.82) * mm, "end": v(-17.16, -14.61) * mm});
            skArc(sketch, "E10.3.4.7", {"start": v(-14.62, -1.28) * mm, "mid": v(-16.41, -2.02) * mm, "end": v(-17.16, -3.82) * mm});
            skLineSegment(sketch, "E10.3.5.0", {"start": v(-14.62, -19.7) * mm, "end": v(-3.82, -19.7) * mm});
            skArc(sketch, "E10.3.5.1", {"start": v(-1.28, -22.23) * mm, "mid": v(-2.02, -20.44) * mm, "end": v(-3.82, -19.7) * mm});
            skLineSegment(sketch, "E10.3.5.2", {"start": v(-1.28, -22.23) * mm, "end": v(-1.28, -33.03) * mm});
            skArc(sketch, "E10.3.5.3", {"start": v(-3.82, -35.57) * mm, "mid": v(-2.02, -34.82) * mm, "end": v(-1.28, -33.03) * mm});
            skLineSegment(sketch, "E10.3.5.4", {"start": v(-14.62, -35.57) * mm, "end": v(-3.82, -35.57) * mm});
            skArc(sketch, "E10.3.5.5", {"start": v(-17.16, -33.03) * mm, "mid": v(-16.41, -34.82) * mm, "end": v(-14.62, -35.57) * mm});
            skLineSegment(sketch, "E10.3.5.6", {"start": v(-17.16, -22.23) * mm, "end": v(-17.16, -33.03) * mm});
            skArc(sketch, "E10.3.5.7", {"start": v(-14.62, -19.7) * mm, "mid": v(-16.41, -20.44) * mm, "end": v(-17.16, -22.23) * mm});
            skLineSegment(sketch, "E10.3.6.0", {"start": v(-14.62, -38.1) * mm, "end": v(-3.82, -38.1) * mm});
            skArc(sketch, "E10.3.6.1", {"start": v(-1.28, -40.65) * mm, "mid": v(-2.02, -38.85) * mm, "end": v(-3.82, -38.1) * mm});
            skLineSegment(sketch, "E10.3.6.2", {"start": v(-1.28, -40.65) * mm, "end": v(-1.28, -51.44) * mm});
            skArc(sketch, "E10.3.6.3", {"start": v(-3.82, -53.98) * mm, "mid": v(-2.02, -53.24) * mm, "end": v(-1.28, -51.44) * mm});
            skLineSegment(sketch, "E10.3.6.4", {"start": v(-14.62, -53.98) * mm, "end": v(-3.82, -53.98) * mm});
            skArc(sketch, "E10.3.6.5", {"start": v(-17.16, -51.44) * mm, "mid": v(-16.41, -53.24) * mm, "end": v(-14.62, -53.98) * mm});
            skLineSegment(sketch, "E10.3.6.6", {"start": v(-17.16, -40.65) * mm, "end": v(-17.16, -51.44) * mm});
            skArc(sketch, "E10.3.6.7", {"start": v(-14.62, -38.1) * mm, "mid": v(-16.41, -38.85) * mm, "end": v(-17.16, -40.65) * mm});
            skLineSegment(sketch, "E10.3.7.0", {"start": v(-14.62, -56.52) * mm, "end": v(-3.82, -56.52) * mm});
            skArc(sketch, "E10.3.7.1", {"start": v(-1.28, -59.06) * mm, "mid": v(-2.02, -57.27) * mm, "end": v(-3.82, -56.52) * mm});
            skLineSegment(sketch, "E10.3.7.2", {"start": v(-1.28, -59.06) * mm, "end": v(-1.28, -69.86) * mm});
            skArc(sketch, "E10.3.7.3", {"start": v(-3.82, -72.4) * mm, "mid": v(-2.02, -71.65) * mm, "end": v(-1.28, -69.86) * mm});
            skLineSegment(sketch, "E10.3.7.4", {"start": v(-14.62, -72.4) * mm, "end": v(-3.82, -72.4) * mm});
            skArc(sketch, "E10.3.7.5", {"start": v(-17.16, -69.86) * mm, "mid": v(-16.41, -71.65) * mm, "end": v(-14.62, -72.4) * mm});
            skLineSegment(sketch, "E10.3.7.6", {"start": v(-17.16, -59.06) * mm, "end": v(-17.16, -69.86) * mm});
            skArc(sketch, "E10.3.7.7", {"start": v(-14.62, -56.52) * mm, "mid": v(-16.41, -57.27) * mm, "end": v(-17.16, -59.06) * mm});
            skLineSegment(sketch, "E10.4.0.0", {"start": v(3.8, 72.38) * mm, "end": v(14.6, 72.38) * mm});
            skArc(sketch, "E10.4.0.1", {"start": v(17.13, 69.84) * mm, "mid": v(16.4, 71.64) * mm, "end": v(14.6, 72.38) * mm});
            skLineSegment(sketch, "E10.4.0.2", {"start": v(17.13, 69.84) * mm, "end": v(17.13, 59.05) * mm});
            skArc(sketch, "E10.4.0.3", {"start": v(14.6, 56.5) * mm, "mid": v(16.4, 57.25) * mm, "end": v(17.13, 59.05) * mm});
            skLineSegment(sketch, "E10.4.0.4", {"start": v(3.8, 56.5) * mm, "end": v(14.6, 56.5) * mm});
            skArc(sketch, "E10.4.0.5", {"start": v(1.26, 59.05) * mm, "mid": v(2, 57.25) * mm, "end": v(3.8, 56.5) * mm});
            skLineSegment(sketch, "E10.4.0.6", {"start": v(1.26, 69.84) * mm, "end": v(1.26, 59.05) * mm});
            skArc(sketch, "E10.4.0.7", {"start": v(3.8, 72.38) * mm, "mid": v(2, 71.64) * mm, "end": v(1.26, 69.84) * mm});
            skLineSegment(sketch, "E10.4.1.0", {"start": v(3.8, 53.97) * mm, "end": v(14.6, 53.97) * mm});
            skArc(sketch, "E10.4.1.1", {"start": v(17.13, 51.43) * mm, "mid": v(16.4, 53.22) * mm, "end": v(14.6, 53.97) * mm});
            skLineSegment(sketch, "E10.4.1.2", {"start": v(17.13, 51.43) * mm, "end": v(17.13, 40.63) * mm});
            skArc(sketch, "E10.4.1.3", {"start": v(14.6, 38.1) * mm, "mid": v(16.4, 38.84) * mm, "end": v(17.13, 40.63) * mm});
            skLineSegment(sketch, "E10.4.1.4", {"start": v(3.8, 38.1) * mm, "end": v(14.6, 38.1) * mm});
            skArc(sketch, "E10.4.1.5", {"start": v(1.26, 40.63) * mm, "mid": v(2, 38.84) * mm, "end": v(3.8, 38.1) * mm});
            skLineSegment(sketch, "E10.4.1.6", {"start": v(1.26, 51.43) * mm, "end": v(1.26, 40.63) * mm});
            skArc(sketch, "E10.4.1.7", {"start": v(3.8, 53.97) * mm, "mid": v(2, 53.22) * mm, "end": v(1.26, 51.43) * mm});
            skLineSegment(sketch, "E10.4.2.0", {"start": v(3.8, 35.55) * mm, "end": v(14.6, 35.55) * mm});
            skArc(sketch, "E10.4.2.1", {"start": v(17.13, 33.01) * mm, "mid": v(16.4, 34.8) * mm, "end": v(14.6, 35.55) * mm});
            skLineSegment(sketch, "E10.4.2.2", {"start": v(17.13, 33.01) * mm, "end": v(17.13, 22.22) * mm});
            skArc(sketch, "E10.4.2.3", {"start": v(14.6, 19.68) * mm, "mid": v(16.4, 20.42) * mm, "end": v(17.13, 22.22) * mm});
            skLineSegment(sketch, "E10.4.2.4", {"start": v(3.8, 19.68) * mm, "end": v(14.6, 19.68) * mm});
            skArc(sketch, "E10.4.2.5", {"start": v(1.26, 22.22) * mm, "mid": v(2, 20.42) * mm, "end": v(3.8, 19.68) * mm});
            skLineSegment(sketch, "E10.4.2.6", {"start": v(1.26, 33.01) * mm, "end": v(1.26, 22.22) * mm});
            skArc(sketch, "E10.4.2.7", {"start": v(3.8, 35.55) * mm, "mid": v(2, 34.8) * mm, "end": v(1.26, 33.01) * mm});
            skLineSegment(sketch, "E10.4.3.0", {"start": v(3.8, 17.14) * mm, "end": v(14.6, 17.14) * mm});
            skArc(sketch, "E10.4.3.1", {"start": v(17.13, 14.6) * mm, "mid": v(16.4, 16.4) * mm, "end": v(14.6, 17.14) * mm});
            skLineSegment(sketch, "E10.4.3.2", {"start": v(17.13, 14.6) * mm, "end": v(17.13, 3.8) * mm});
            skArc(sketch, "E10.4.3.3", {"start": v(14.6, 1.26) * mm, "mid": v(16.4, 2) * mm, "end": v(17.13, 3.8) * mm});
            skLineSegment(sketch, "E10.4.3.4", {"start": v(3.8, 1.26) * mm, "end": v(14.6, 1.26) * mm});
            skArc(sketch, "E10.4.3.5", {"start": v(1.26, 3.8) * mm, "mid": v(2, 2) * mm, "end": v(3.8, 1.26) * mm});
            skLineSegment(sketch, "E10.4.3.6", {"start": v(1.26, 14.6) * mm, "end": v(1.26, 3.8) * mm});
            skArc(sketch, "E10.4.3.7", {"start": v(3.8, 17.14) * mm, "mid": v(2, 16.4) * mm, "end": v(1.26, 14.6) * mm});
            skLineSegment(sketch, "E10.4.4.0", {"start": v(3.8, -1.28) * mm, "end": v(14.6, -1.28) * mm});
            skArc(sketch, "E10.4.4.1", {"start": v(17.13, -3.82) * mm, "mid": v(16.4, -2.02) * mm, "end": v(14.6, -1.28) * mm});
            skLineSegment(sketch, "E10.4.4.2", {"start": v(17.13, -3.82) * mm, "end": v(17.13, -14.61) * mm});
            skArc(sketch, "E10.4.4.3", {"start": v(14.6, -17.15) * mm, "mid": v(16.4, -16.4) * mm, "end": v(17.13, -14.61) * mm});
            skLineSegment(sketch, "E10.4.4.4", {"start": v(3.8, -17.15) * mm, "end": v(14.6, -17.15) * mm});
            skArc(sketch, "E10.4.4.5", {"start": v(1.26, -14.61) * mm, "mid": v(2, -16.4) * mm, "end": v(3.8, -17.15) * mm});
            skLineSegment(sketch, "E10.4.4.6", {"start": v(1.26, -3.82) * mm, "end": v(1.26, -14.61) * mm});
            skArc(sketch, "E10.4.4.7", {"start": v(3.8, -1.28) * mm, "mid": v(2, -2.02) * mm, "end": v(1.26, -3.82) * mm});
            skLineSegment(sketch, "E10.4.5.0", {"start": v(3.8, -19.7) * mm, "end": v(14.6, -19.7) * mm});
            skArc(sketch, "E10.4.5.1", {"start": v(17.13, -22.23) * mm, "mid": v(16.4, -20.44) * mm, "end": v(14.6, -19.7) * mm});
            skLineSegment(sketch, "E10.4.5.2", {"start": v(17.13, -22.23) * mm, "end": v(17.13, -33.03) * mm});
            skArc(sketch, "E10.4.5.3", {"start": v(14.6, -35.57) * mm, "mid": v(16.4, -34.82) * mm, "end": v(17.13, -33.03) * mm});
            skLineSegment(sketch, "E10.4.5.4", {"start": v(3.8, -35.57) * mm, "end": v(14.6, -35.57) * mm});
            skArc(sketch, "E10.4.5.5", {"start": v(1.26, -33.03) * mm, "mid": v(2, -34.82) * mm, "end": v(3.8, -35.57) * mm});
            skLineSegment(sketch, "E10.4.5.6", {"start": v(1.26, -22.23) * mm, "end": v(1.26, -33.03) * mm});
            skArc(sketch, "E10.4.5.7", {"start": v(3.8, -19.7) * mm, "mid": v(2, -20.44) * mm, "end": v(1.26, -22.23) * mm});
            skLineSegment(sketch, "E10.4.6.0", {"start": v(3.8, -38.1) * mm, "end": v(14.6, -38.1) * mm});
            skArc(sketch, "E10.4.6.1", {"start": v(17.13, -40.65) * mm, "mid": v(16.4, -38.85) * mm, "end": v(14.6, -38.1) * mm});
            skLineSegment(sketch, "E10.4.6.2", {"start": v(17.13, -40.65) * mm, "end": v(17.13, -51.44) * mm});
            skArc(sketch, "E10.4.6.3", {"start": v(14.6, -53.98) * mm, "mid": v(16.4, -53.24) * mm, "end": v(17.13, -51.44) * mm});
            skLineSegment(sketch, "E10.4.6.4", {"start": v(3.8, -53.98) * mm, "end": v(14.6, -53.98) * mm});
            skArc(sketch, "E10.4.6.5", {"start": v(1.26, -51.44) * mm, "mid": v(2, -53.24) * mm, "end": v(3.8, -53.98) * mm});
            skLineSegment(sketch, "E10.4.6.6", {"start": v(1.26, -40.65) * mm, "end": v(1.26, -51.44) * mm});
            skArc(sketch, "E10.4.6.7", {"start": v(3.8, -38.1) * mm, "mid": v(2, -38.85) * mm, "end": v(1.26, -40.65) * mm});
            skLineSegment(sketch, "E10.4.7.0", {"start": v(3.8, -56.52) * mm, "end": v(14.6, -56.52) * mm});
            skArc(sketch, "E10.4.7.1", {"start": v(17.13, -59.06) * mm, "mid": v(16.4, -57.27) * mm, "end": v(14.6, -56.52) * mm});
            skLineSegment(sketch, "E10.4.7.2", {"start": v(17.13, -59.06) * mm, "end": v(17.13, -69.86) * mm});
            skArc(sketch, "E10.4.7.3", {"start": v(14.6, -72.4) * mm, "mid": v(16.4, -71.65) * mm, "end": v(17.13, -69.86) * mm});
            skLineSegment(sketch, "E10.4.7.4", {"start": v(3.8, -72.4) * mm, "end": v(14.6, -72.4) * mm});
            skArc(sketch, "E10.4.7.5", {"start": v(1.26, -69.86) * mm, "mid": v(2, -71.65) * mm, "end": v(3.8, -72.4) * mm});
            skLineSegment(sketch, "E10.4.7.6", {"start": v(1.26, -59.06) * mm, "end": v(1.26, -69.86) * mm});
            skArc(sketch, "E10.4.7.7", {"start": v(3.8, -56.52) * mm, "mid": v(2, -57.27) * mm, "end": v(1.26, -59.06) * mm});
            skLineSegment(sketch, "E10.5.0.0", {"start": v(22.21, 72.38) * mm, "end": v(33, 72.38) * mm});
            skArc(sketch, "E10.5.0.1", {"start": v(35.55, 69.84) * mm, "mid": v(34.8, 71.64) * mm, "end": v(33, 72.38) * mm});
            skLineSegment(sketch, "E10.5.0.2", {"start": v(35.55, 69.84) * mm, "end": v(35.55, 59.05) * mm});
            skArc(sketch, "E10.5.0.3", {"start": v(33, 56.5) * mm, "mid": v(34.8, 57.25) * mm, "end": v(35.55, 59.05) * mm});
            skLineSegment(sketch, "E10.5.0.4", {"start": v(22.21, 56.5) * mm, "end": v(33, 56.5) * mm});
            skArc(sketch, "E10.5.0.5", {"start": v(19.67, 59.05) * mm, "mid": v(20.42, 57.25) * mm, "end": v(22.21, 56.5) * mm});
            skLineSegment(sketch, "E10.5.0.6", {"start": v(19.67, 69.84) * mm, "end": v(19.67, 59.05) * mm});
            skArc(sketch, "E10.5.0.7", {"start": v(22.21, 72.38) * mm, "mid": v(20.42, 71.64) * mm, "end": v(19.67, 69.84) * mm});
            skLineSegment(sketch, "E10.5.1.0", {"start": v(22.21, 53.97) * mm, "end": v(33, 53.97) * mm});
            skArc(sketch, "E10.5.1.1", {"start": v(35.55, 51.43) * mm, "mid": v(34.8, 53.22) * mm, "end": v(33, 53.97) * mm});
            skLineSegment(sketch, "E10.5.1.2", {"start": v(35.55, 51.43) * mm, "end": v(35.55, 40.63) * mm});
            skArc(sketch, "E10.5.1.3", {"start": v(33, 38.1) * mm, "mid": v(34.8, 38.84) * mm, "end": v(35.55, 40.63) * mm});
            skLineSegment(sketch, "E10.5.1.4", {"start": v(22.21, 38.1) * mm, "end": v(33, 38.1) * mm});
            skArc(sketch, "E10.5.1.5", {"start": v(19.67, 40.63) * mm, "mid": v(20.42, 38.84) * mm, "end": v(22.21, 38.1) * mm});
            skLineSegment(sketch, "E10.5.1.6", {"start": v(19.67, 51.43) * mm, "end": v(19.67, 40.63) * mm});
            skArc(sketch, "E10.5.1.7", {"start": v(22.21, 53.97) * mm, "mid": v(20.42, 53.22) * mm, "end": v(19.67, 51.43) * mm});
            skLineSegment(sketch, "E10.5.2.0", {"start": v(22.21, 35.55) * mm, "end": v(33, 35.55) * mm});
            skArc(sketch, "E10.5.2.1", {"start": v(35.55, 33.01) * mm, "mid": v(34.8, 34.8) * mm, "end": v(33, 35.55) * mm});
            skLineSegment(sketch, "E10.5.2.2", {"start": v(35.55, 33.01) * mm, "end": v(35.55, 22.22) * mm});
            skArc(sketch, "E10.5.2.3", {"start": v(33, 19.68) * mm, "mid": v(34.8, 20.42) * mm, "end": v(35.55, 22.22) * mm});
            skLineSegment(sketch, "E10.5.2.4", {"start": v(22.21, 19.68) * mm, "end": v(33, 19.68) * mm});
            skArc(sketch, "E10.5.2.5", {"start": v(19.67, 22.22) * mm, "mid": v(20.42, 20.42) * mm, "end": v(22.21, 19.68) * mm});
            skLineSegment(sketch, "E10.5.2.6", {"start": v(19.67, 33.01) * mm, "end": v(19.67, 22.22) * mm});
            skArc(sketch, "E10.5.2.7", {"start": v(22.21, 35.55) * mm, "mid": v(20.42, 34.8) * mm, "end": v(19.67, 33.01) * mm});
            skLineSegment(sketch, "E10.5.3.0", {"start": v(22.21, 17.14) * mm, "end": v(33, 17.14) * mm});
            skArc(sketch, "E10.5.3.1", {"start": v(35.55, 14.6) * mm, "mid": v(34.8, 16.4) * mm, "end": v(33, 17.14) * mm});
            skLineSegment(sketch, "E10.5.3.2", {"start": v(35.55, 14.6) * mm, "end": v(35.55, 3.8) * mm});
            skArc(sketch, "E10.5.3.3", {"start": v(33, 1.26) * mm, "mid": v(34.8, 2) * mm, "end": v(35.55, 3.8) * mm});
            skLineSegment(sketch, "E10.5.3.4", {"start": v(22.21, 1.26) * mm, "end": v(33, 1.26) * mm});
            skArc(sketch, "E10.5.3.5", {"start": v(19.67, 3.8) * mm, "mid": v(20.42, 2) * mm, "end": v(22.21, 1.26) * mm});
            skLineSegment(sketch, "E10.5.3.6", {"start": v(19.67, 14.6) * mm, "end": v(19.67, 3.8) * mm});
            skArc(sketch, "E10.5.3.7", {"start": v(22.21, 17.14) * mm, "mid": v(20.42, 16.4) * mm, "end": v(19.67, 14.6) * mm});
            skLineSegment(sketch, "E10.5.4.0", {"start": v(22.21, -1.28) * mm, "end": v(33, -1.28) * mm});
            skArc(sketch, "E10.5.4.1", {"start": v(35.55, -3.82) * mm, "mid": v(34.8, -2.02) * mm, "end": v(33, -1.28) * mm});
            skLineSegment(sketch, "E10.5.4.2", {"start": v(35.55, -3.82) * mm, "end": v(35.55, -14.61) * mm});
            skArc(sketch, "E10.5.4.3", {"start": v(33, -17.15) * mm, "mid": v(34.8, -16.4) * mm, "end": v(35.55, -14.61) * mm});
            skLineSegment(sketch, "E10.5.4.4", {"start": v(22.21, -17.15) * mm, "end": v(33, -17.15) * mm});
            skArc(sketch, "E10.5.4.5", {"start": v(19.67, -14.61) * mm, "mid": v(20.42, -16.4) * mm, "end": v(22.21, -17.15) * mm});
            skLineSegment(sketch, "E10.5.4.6", {"start": v(19.67, -3.82) * mm, "end": v(19.67, -14.61) * mm});
            skArc(sketch, "E10.5.4.7", {"start": v(22.21, -1.28) * mm, "mid": v(20.42, -2.02) * mm, "end": v(19.67, -3.82) * mm});
            skLineSegment(sketch, "E10.5.5.0", {"start": v(22.21, -19.7) * mm, "end": v(33, -19.7) * mm});
            skArc(sketch, "E10.5.5.1", {"start": v(35.55, -22.23) * mm, "mid": v(34.8, -20.44) * mm, "end": v(33, -19.7) * mm});
            skLineSegment(sketch, "E10.5.5.2", {"start": v(35.55, -22.23) * mm, "end": v(35.55, -33.03) * mm});
            skArc(sketch, "E10.5.5.3", {"start": v(33, -35.57) * mm, "mid": v(34.8, -34.82) * mm, "end": v(35.55, -33.03) * mm});
            skLineSegment(sketch, "E10.5.5.4", {"start": v(22.21, -35.57) * mm, "end": v(33, -35.57) * mm});
            skArc(sketch, "E10.5.5.5", {"start": v(19.67, -33.03) * mm, "mid": v(20.42, -34.82) * mm, "end": v(22.21, -35.57) * mm});
            skLineSegment(sketch, "E10.5.5.6", {"start": v(19.67, -22.23) * mm, "end": v(19.67, -33.03) * mm});
            skArc(sketch, "E10.5.5.7", {"start": v(22.21, -19.7) * mm, "mid": v(20.42, -20.44) * mm, "end": v(19.67, -22.23) * mm});
            skLineSegment(sketch, "E10.5.6.0", {"start": v(22.21, -38.1) * mm, "end": v(33, -38.1) * mm});
            skArc(sketch, "E10.5.6.1", {"start": v(35.55, -40.65) * mm, "mid": v(34.8, -38.85) * mm, "end": v(33, -38.1) * mm});
            skLineSegment(sketch, "E10.5.6.2", {"start": v(35.55, -40.65) * mm, "end": v(35.55, -51.44) * mm});
            skArc(sketch, "E10.5.6.3", {"start": v(33, -53.98) * mm, "mid": v(34.8, -53.24) * mm, "end": v(35.55, -51.44) * mm});
            skLineSegment(sketch, "E10.5.6.4", {"start": v(22.21, -53.98) * mm, "end": v(33, -53.98) * mm});
            skArc(sketch, "E10.5.6.5", {"start": v(19.67, -51.44) * mm, "mid": v(20.42, -53.24) * mm, "end": v(22.21, -53.98) * mm});
            skLineSegment(sketch, "E10.5.6.6", {"start": v(19.67, -40.65) * mm, "end": v(19.67, -51.44) * mm});
            skArc(sketch, "E10.5.6.7", {"start": v(22.21, -38.1) * mm, "mid": v(20.42, -38.85) * mm, "end": v(19.67, -40.65) * mm});
            skLineSegment(sketch, "E10.5.7.0", {"start": v(22.21, -56.52) * mm, "end": v(33, -56.52) * mm});
            skArc(sketch, "E10.5.7.1", {"start": v(35.55, -59.06) * mm, "mid": v(34.8, -57.27) * mm, "end": v(33, -56.52) * mm});
            skLineSegment(sketch, "E10.5.7.2", {"start": v(35.55, -59.06) * mm, "end": v(35.55, -69.86) * mm});
            skArc(sketch, "E10.5.7.3", {"start": v(33, -72.4) * mm, "mid": v(34.8, -71.65) * mm, "end": v(35.55, -69.86) * mm});
            skLineSegment(sketch, "E10.5.7.4", {"start": v(22.21, -72.4) * mm, "end": v(33, -72.4) * mm});
            skArc(sketch, "E10.5.7.5", {"start": v(19.67, -69.86) * mm, "mid": v(20.42, -71.65) * mm, "end": v(22.21, -72.4) * mm});
            skLineSegment(sketch, "E10.5.7.6", {"start": v(19.67, -59.06) * mm, "end": v(19.67, -69.86) * mm});
            skArc(sketch, "E10.5.7.7", {"start": v(22.21, -56.52) * mm, "mid": v(20.42, -57.27) * mm, "end": v(19.67, -59.06) * mm});
            skLineSegment(sketch, "E10.6.0.0", {"start": v(40.63, 72.38) * mm, "end": v(51.42, 72.38) * mm});
            skArc(sketch, "E10.6.0.1", {"start": v(53.96, 69.84) * mm, "mid": v(53.22, 71.64) * mm, "end": v(51.42, 72.38) * mm});
            skLineSegment(sketch, "E10.6.0.2", {"start": v(53.96, 69.84) * mm, "end": v(53.96, 59.05) * mm});
            skArc(sketch, "E10.6.0.3", {"start": v(51.42, 56.5) * mm, "mid": v(53.22, 57.25) * mm, "end": v(53.96, 59.05) * mm});
            skLineSegment(sketch, "E10.6.0.4", {"start": v(40.63, 56.5) * mm, "end": v(51.42, 56.5) * mm});
            skArc(sketch, "E10.6.0.5", {"start": v(38.09, 59.05) * mm, "mid": v(38.83, 57.25) * mm, "end": v(40.63, 56.5) * mm});
            skLineSegment(sketch, "E10.6.0.6", {"start": v(38.09, 69.84) * mm, "end": v(38.09, 59.05) * mm});
            skArc(sketch, "E10.6.0.7", {"start": v(40.63, 72.38) * mm, "mid": v(38.83, 71.64) * mm, "end": v(38.09, 69.84) * mm});
            skLineSegment(sketch, "E10.6.1.0", {"start": v(40.63, 53.97) * mm, "end": v(51.42, 53.97) * mm});
            skArc(sketch, "E10.6.1.1", {"start": v(53.96, 51.43) * mm, "mid": v(53.22, 53.22) * mm, "end": v(51.42, 53.97) * mm});
            skLineSegment(sketch, "E10.6.1.2", {"start": v(53.96, 51.43) * mm, "end": v(53.96, 40.63) * mm});
            skArc(sketch, "E10.6.1.3", {"start": v(51.42, 38.1) * mm, "mid": v(53.22, 38.84) * mm, "end": v(53.96, 40.63) * mm});
            skLineSegment(sketch, "E10.6.1.4", {"start": v(40.63, 38.1) * mm, "end": v(51.42, 38.1) * mm});
            skArc(sketch, "E10.6.1.5", {"start": v(38.09, 40.63) * mm, "mid": v(38.83, 38.84) * mm, "end": v(40.63, 38.1) * mm});
            skLineSegment(sketch, "E10.6.1.6", {"start": v(38.09, 51.43) * mm, "end": v(38.09, 40.63) * mm});
            skArc(sketch, "E10.6.1.7", {"start": v(40.63, 53.97) * mm, "mid": v(38.83, 53.22) * mm, "end": v(38.09, 51.43) * mm});
            skLineSegment(sketch, "E10.6.2.0", {"start": v(40.63, 35.55) * mm, "end": v(51.42, 35.55) * mm});
            skArc(sketch, "E10.6.2.1", {"start": v(53.96, 33.01) * mm, "mid": v(53.22, 34.8) * mm, "end": v(51.42, 35.55) * mm});
            skLineSegment(sketch, "E10.6.2.2", {"start": v(53.96, 33.01) * mm, "end": v(53.96, 22.22) * mm});
            skArc(sketch, "E10.6.2.3", {"start": v(51.42, 19.68) * mm, "mid": v(53.22, 20.42) * mm, "end": v(53.96, 22.22) * mm});
            skLineSegment(sketch, "E10.6.2.4", {"start": v(40.63, 19.68) * mm, "end": v(51.42, 19.68) * mm});
            skArc(sketch, "E10.6.2.5", {"start": v(38.09, 22.22) * mm, "mid": v(38.83, 20.42) * mm, "end": v(40.63, 19.68) * mm});
            skLineSegment(sketch, "E10.6.2.6", {"start": v(38.09, 33.01) * mm, "end": v(38.09, 22.22) * mm});
            skArc(sketch, "E10.6.2.7", {"start": v(40.63, 35.55) * mm, "mid": v(38.83, 34.8) * mm, "end": v(38.09, 33.01) * mm});
            skLineSegment(sketch, "E10.6.3.0", {"start": v(40.63, 17.14) * mm, "end": v(51.42, 17.14) * mm});
            skArc(sketch, "E10.6.3.1", {"start": v(53.96, 14.6) * mm, "mid": v(53.22, 16.4) * mm, "end": v(51.42, 17.14) * mm});
            skLineSegment(sketch, "E10.6.3.2", {"start": v(53.96, 14.6) * mm, "end": v(53.96, 3.8) * mm});
            skArc(sketch, "E10.6.3.3", {"start": v(51.42, 1.26) * mm, "mid": v(53.22, 2) * mm, "end": v(53.96, 3.8) * mm});
            skLineSegment(sketch, "E10.6.3.4", {"start": v(40.63, 1.26) * mm, "end": v(51.42, 1.26) * mm});
            skArc(sketch, "E10.6.3.5", {"start": v(38.09, 3.8) * mm, "mid": v(38.83, 2) * mm, "end": v(40.63, 1.26) * mm});
            skLineSegment(sketch, "E10.6.3.6", {"start": v(38.09, 14.6) * mm, "end": v(38.09, 3.8) * mm});
            skArc(sketch, "E10.6.3.7", {"start": v(40.63, 17.14) * mm, "mid": v(38.83, 16.4) * mm, "end": v(38.09, 14.6) * mm});
            skLineSegment(sketch, "E10.6.4.0", {"start": v(40.63, -1.28) * mm, "end": v(51.42, -1.28) * mm});
            skArc(sketch, "E10.6.4.1", {"start": v(53.96, -3.82) * mm, "mid": v(53.22, -2.02) * mm, "end": v(51.42, -1.28) * mm});
            skLineSegment(sketch, "E10.6.4.2", {"start": v(53.96, -3.82) * mm, "end": v(53.96, -14.61) * mm});
            skArc(sketch, "E10.6.4.3", {"start": v(51.42, -17.15) * mm, "mid": v(53.22, -16.4) * mm, "end": v(53.96, -14.61) * mm});
            skLineSegment(sketch, "E10.6.4.4", {"start": v(40.63, -17.15) * mm, "end": v(51.42, -17.15) * mm});
            skArc(sketch, "E10.6.4.5", {"start": v(38.09, -14.61) * mm, "mid": v(38.83, -16.4) * mm, "end": v(40.63, -17.15) * mm});
            skLineSegment(sketch, "E10.6.4.6", {"start": v(38.09, -3.82) * mm, "end": v(38.09, -14.61) * mm});
            skArc(sketch, "E10.6.4.7", {"start": v(40.63, -1.28) * mm, "mid": v(38.83, -2.02) * mm, "end": v(38.09, -3.82) * mm});
            skLineSegment(sketch, "E10.6.5.0", {"start": v(40.63, -19.7) * mm, "end": v(51.42, -19.7) * mm});
            skArc(sketch, "E10.6.5.1", {"start": v(53.96, -22.23) * mm, "mid": v(53.22, -20.44) * mm, "end": v(51.42, -19.7) * mm});
            skLineSegment(sketch, "E10.6.5.2", {"start": v(53.96, -22.23) * mm, "end": v(53.96, -33.03) * mm});
            skArc(sketch, "E10.6.5.3", {"start": v(51.42, -35.57) * mm, "mid": v(53.22, -34.82) * mm, "end": v(53.96, -33.03) * mm});
            skLineSegment(sketch, "E10.6.5.4", {"start": v(40.63, -35.57) * mm, "end": v(51.42, -35.57) * mm});
            skArc(sketch, "E10.6.5.5", {"start": v(38.09, -33.03) * mm, "mid": v(38.83, -34.82) * mm, "end": v(40.63, -35.57) * mm});
            skLineSegment(sketch, "E10.6.5.6", {"start": v(38.09, -22.23) * mm, "end": v(38.09, -33.03) * mm});
            skArc(sketch, "E10.6.5.7", {"start": v(40.63, -19.7) * mm, "mid": v(38.83, -20.44) * mm, "end": v(38.09, -22.23) * mm});
            skLineSegment(sketch, "E10.6.6.0", {"start": v(40.63, -38.1) * mm, "end": v(51.42, -38.1) * mm});
            skArc(sketch, "E10.6.6.1", {"start": v(53.96, -40.65) * mm, "mid": v(53.22, -38.85) * mm, "end": v(51.42, -38.1) * mm});
            skLineSegment(sketch, "E10.6.6.2", {"start": v(53.96, -40.65) * mm, "end": v(53.96, -51.44) * mm});
            skArc(sketch, "E10.6.6.3", {"start": v(51.42, -53.98) * mm, "mid": v(53.22, -53.24) * mm, "end": v(53.96, -51.44) * mm});
            skLineSegment(sketch, "E10.6.6.4", {"start": v(40.63, -53.98) * mm, "end": v(51.42, -53.98) * mm});
            skArc(sketch, "E10.6.6.5", {"start": v(38.09, -51.44) * mm, "mid": v(38.83, -53.24) * mm, "end": v(40.63, -53.98) * mm});
            skLineSegment(sketch, "E10.6.6.6", {"start": v(38.09, -40.65) * mm, "end": v(38.09, -51.44) * mm});
            skArc(sketch, "E10.6.6.7", {"start": v(40.63, -38.1) * mm, "mid": v(38.83, -38.85) * mm, "end": v(38.09, -40.65) * mm});
            skLineSegment(sketch, "E10.6.7.0", {"start": v(40.63, -56.52) * mm, "end": v(51.42, -56.52) * mm});
            skArc(sketch, "E10.6.7.1", {"start": v(53.96, -59.06) * mm, "mid": v(53.22, -57.27) * mm, "end": v(51.42, -56.52) * mm});
            skLineSegment(sketch, "E10.6.7.2", {"start": v(53.96, -59.06) * mm, "end": v(53.96, -69.86) * mm});
            skArc(sketch, "E10.6.7.3", {"start": v(51.42, -72.4) * mm, "mid": v(53.22, -71.65) * mm, "end": v(53.96, -69.86) * mm});
            skLineSegment(sketch, "E10.6.7.4", {"start": v(40.63, -72.4) * mm, "end": v(51.42, -72.4) * mm});
            skArc(sketch, "E10.6.7.5", {"start": v(38.09, -69.86) * mm, "mid": v(38.83, -71.65) * mm, "end": v(40.63, -72.4) * mm});
            skLineSegment(sketch, "E10.6.7.6", {"start": v(38.09, -59.06) * mm, "end": v(38.09, -69.86) * mm});
            skArc(sketch, "E10.6.7.7", {"start": v(40.63, -56.52) * mm, "mid": v(38.83, -57.27) * mm, "end": v(38.09, -59.06) * mm});
            skLineSegment(sketch, "E10.7.0.0", {"start": v(59.04, 72.38) * mm, "end": v(69.84, 72.38) * mm});
            skArc(sketch, "E10.7.0.1", {"start": v(72.38, 69.84) * mm, "mid": v(71.64, 71.64) * mm, "end": v(69.84, 72.38) * mm});
            skLineSegment(sketch, "E10.7.0.2", {"start": v(72.38, 69.84) * mm, "end": v(72.38, 59.05) * mm});
            skArc(sketch, "E10.7.0.3", {"start": v(69.84, 56.5) * mm, "mid": v(71.64, 57.25) * mm, "end": v(72.38, 59.05) * mm});
            skLineSegment(sketch, "E10.7.0.4", {"start": v(59.04, 56.5) * mm, "end": v(69.84, 56.5) * mm});
            skArc(sketch, "E10.7.0.5", {"start": v(56.5, 59.05) * mm, "mid": v(57.25, 57.25) * mm, "end": v(59.04, 56.5) * mm});
            skLineSegment(sketch, "E10.7.0.6", {"start": v(56.5, 69.84) * mm, "end": v(56.5, 59.05) * mm});
            skArc(sketch, "E10.7.0.7", {"start": v(59.04, 72.38) * mm, "mid": v(57.25, 71.64) * mm, "end": v(56.5, 69.84) * mm});
            skLineSegment(sketch, "E10.7.1.0", {"start": v(59.04, 53.97) * mm, "end": v(69.84, 53.97) * mm});
            skArc(sketch, "E10.7.1.1", {"start": v(72.38, 51.43) * mm, "mid": v(71.64, 53.22) * mm, "end": v(69.84, 53.97) * mm});
            skLineSegment(sketch, "E10.7.1.2", {"start": v(72.38, 51.43) * mm, "end": v(72.38, 40.63) * mm});
            skArc(sketch, "E10.7.1.3", {"start": v(69.84, 38.1) * mm, "mid": v(71.64, 38.84) * mm, "end": v(72.38, 40.63) * mm});
            skLineSegment(sketch, "E10.7.1.4", {"start": v(59.04, 38.1) * mm, "end": v(69.84, 38.1) * mm});
            skArc(sketch, "E10.7.1.5", {"start": v(56.5, 40.63) * mm, "mid": v(57.25, 38.84) * mm, "end": v(59.04, 38.1) * mm});
            skLineSegment(sketch, "E10.7.1.6", {"start": v(56.5, 51.43) * mm, "end": v(56.5, 40.63) * mm});
            skArc(sketch, "E10.7.1.7", {"start": v(59.04, 53.97) * mm, "mid": v(57.25, 53.22) * mm, "end": v(56.5, 51.43) * mm});
            skLineSegment(sketch, "E10.7.2.0", {"start": v(59.04, 35.55) * mm, "end": v(69.84, 35.55) * mm});
            skArc(sketch, "E10.7.2.1", {"start": v(72.38, 33.01) * mm, "mid": v(71.64, 34.8) * mm, "end": v(69.84, 35.55) * mm});
            skLineSegment(sketch, "E10.7.2.2", {"start": v(72.38, 33.01) * mm, "end": v(72.38, 22.22) * mm});
            skArc(sketch, "E10.7.2.3", {"start": v(69.84, 19.68) * mm, "mid": v(71.64, 20.42) * mm, "end": v(72.38, 22.22) * mm});
            skLineSegment(sketch, "E10.7.2.4", {"start": v(59.04, 19.68) * mm, "end": v(69.84, 19.68) * mm});
            skArc(sketch, "E10.7.2.5", {"start": v(56.5, 22.22) * mm, "mid": v(57.25, 20.42) * mm, "end": v(59.04, 19.68) * mm});
            skLineSegment(sketch, "E10.7.2.6", {"start": v(56.5, 33.01) * mm, "end": v(56.5, 22.22) * mm});
            skArc(sketch, "E10.7.2.7", {"start": v(59.04, 35.55) * mm, "mid": v(57.25, 34.8) * mm, "end": v(56.5, 33.01) * mm});
            skLineSegment(sketch, "E10.7.3.0", {"start": v(59.04, 17.14) * mm, "end": v(69.84, 17.14) * mm});
            skArc(sketch, "E10.7.3.1", {"start": v(72.38, 14.6) * mm, "mid": v(71.64, 16.4) * mm, "end": v(69.84, 17.14) * mm});
            skLineSegment(sketch, "E10.7.3.2", {"start": v(72.38, 14.6) * mm, "end": v(72.38, 3.8) * mm});
            skArc(sketch, "E10.7.3.3", {"start": v(69.84, 1.26) * mm, "mid": v(71.64, 2) * mm, "end": v(72.38, 3.8) * mm});
            skLineSegment(sketch, "E10.7.3.4", {"start": v(59.04, 1.26) * mm, "end": v(69.84, 1.26) * mm});
            skArc(sketch, "E10.7.3.5", {"start": v(56.5, 3.8) * mm, "mid": v(57.25, 2) * mm, "end": v(59.04, 1.26) * mm});
            skLineSegment(sketch, "E10.7.3.6", {"start": v(56.5, 14.6) * mm, "end": v(56.5, 3.8) * mm});
            skArc(sketch, "E10.7.3.7", {"start": v(59.04, 17.14) * mm, "mid": v(57.25, 16.4) * mm, "end": v(56.5, 14.6) * mm});
            skLineSegment(sketch, "E10.7.4.0", {"start": v(59.04, -1.28) * mm, "end": v(69.84, -1.28) * mm});
            skArc(sketch, "E10.7.4.1", {"start": v(72.38, -3.82) * mm, "mid": v(71.64, -2.02) * mm, "end": v(69.84, -1.28) * mm});
            skLineSegment(sketch, "E10.7.4.2", {"start": v(72.38, -3.82) * mm, "end": v(72.38, -14.61) * mm});
            skArc(sketch, "E10.7.4.3", {"start": v(69.84, -17.15) * mm, "mid": v(71.64, -16.4) * mm, "end": v(72.38, -14.61) * mm});
            skLineSegment(sketch, "E10.7.4.4", {"start": v(59.04, -17.15) * mm, "end": v(69.84, -17.15) * mm});
            skArc(sketch, "E10.7.4.5", {"start": v(56.5, -14.61) * mm, "mid": v(57.25, -16.4) * mm, "end": v(59.04, -17.15) * mm});
            skLineSegment(sketch, "E10.7.4.6", {"start": v(56.5, -3.82) * mm, "end": v(56.5, -14.61) * mm});
            skArc(sketch, "E10.7.4.7", {"start": v(59.04, -1.28) * mm, "mid": v(57.25, -2.02) * mm, "end": v(56.5, -3.82) * mm});
            skLineSegment(sketch, "E10.7.5.0", {"start": v(59.04, -19.7) * mm, "end": v(69.84, -19.7) * mm});
            skArc(sketch, "E10.7.5.1", {"start": v(72.38, -22.23) * mm, "mid": v(71.64, -20.44) * mm, "end": v(69.84, -19.7) * mm});
            skLineSegment(sketch, "E10.7.5.2", {"start": v(72.38, -22.23) * mm, "end": v(72.38, -33.03) * mm});
            skArc(sketch, "E10.7.5.3", {"start": v(69.84, -35.57) * mm, "mid": v(71.64, -34.82) * mm, "end": v(72.38, -33.03) * mm});
            skLineSegment(sketch, "E10.7.5.4", {"start": v(59.04, -35.57) * mm, "end": v(69.84, -35.57) * mm});
            skArc(sketch, "E10.7.5.5", {"start": v(56.5, -33.03) * mm, "mid": v(57.25, -34.82) * mm, "end": v(59.04, -35.57) * mm});
            skLineSegment(sketch, "E10.7.5.6", {"start": v(56.5, -22.23) * mm, "end": v(56.5, -33.03) * mm});
            skArc(sketch, "E10.7.5.7", {"start": v(59.04, -19.7) * mm, "mid": v(57.25, -20.44) * mm, "end": v(56.5, -22.23) * mm});
            skLineSegment(sketch, "E10.7.6.0", {"start": v(59.04, -38.1) * mm, "end": v(69.84, -38.1) * mm});
            skArc(sketch, "E10.7.6.1", {"start": v(72.38, -40.65) * mm, "mid": v(71.64, -38.85) * mm, "end": v(69.84, -38.1) * mm});
            skLineSegment(sketch, "E10.7.6.2", {"start": v(72.38, -40.65) * mm, "end": v(72.38, -51.44) * mm});
            skArc(sketch, "E10.7.6.3", {"start": v(69.84, -53.98) * mm, "mid": v(71.64, -53.24) * mm, "end": v(72.38, -51.44) * mm});
            skLineSegment(sketch, "E10.7.6.4", {"start": v(59.04, -53.98) * mm, "end": v(69.84, -53.98) * mm});
            skArc(sketch, "E10.7.6.5", {"start": v(56.5, -51.44) * mm, "mid": v(57.25, -53.24) * mm, "end": v(59.04, -53.98) * mm});
            skLineSegment(sketch, "E10.7.6.6", {"start": v(56.5, -40.65) * mm, "end": v(56.5, -51.44) * mm});
            skArc(sketch, "E10.7.6.7", {"start": v(59.04, -38.1) * mm, "mid": v(57.25, -38.85) * mm, "end": v(56.5, -40.65) * mm});
            skLineSegment(sketch, "E10.7.7.0", {"start": v(59.04, -56.52) * mm, "end": v(69.84, -56.52) * mm});
            skArc(sketch, "E10.7.7.1", {"start": v(72.38, -59.06) * mm, "mid": v(71.64, -57.27) * mm, "end": v(69.84, -56.52) * mm});
            skLineSegment(sketch, "E10.7.7.2", {"start": v(72.38, -59.06) * mm, "end": v(72.38, -69.86) * mm});
            skArc(sketch, "E10.7.7.3", {"start": v(69.84, -72.4) * mm, "mid": v(71.64, -71.65) * mm, "end": v(72.38, -69.86) * mm});
            skLineSegment(sketch, "E10.7.7.4", {"start": v(59.04, -72.4) * mm, "end": v(69.84, -72.4) * mm});
            skArc(sketch, "E10.7.7.5", {"start": v(56.5, -69.86) * mm, "mid": v(57.25, -71.65) * mm, "end": v(59.04, -72.4) * mm});
            skLineSegment(sketch, "E10.7.7.6", {"start": v(56.5, -59.06) * mm, "end": v(56.5, -69.86) * mm});
            skArc(sketch, "E10.7.7.7", {"start": v(59.04, -56.52) * mm, "mid": v(57.25, -57.27) * mm, "end": v(56.5, -59.06) * mm});
            skLineSegment(sketch, "E10.direction1", {"start": v(-69.86, 72.38) * mm, "end": v(-51.45, 72.38) * mm, "construction": true});
            skLineSegment(sketch, "E10.direction2", {"start": v(-69.86, 72.38) * mm, "end": v(-69.86, 53.97) * mm, "construction": true});
            skSolve(sketch);
        }
        {
            var Q0;
            Q0 = qSketchRegion(id + "F0", true);
            extrude(context, id + "F1", {"entities" : qUnion([Q0]), "depth" : 6.35 * mm, "offsetDistance" : 25.4 * mm});
        }
        {
            var Q0;
            Q0=makeQuery(id+"F1.opExtrude","CAP_FACE",FACE,{"disambiguationData":[OSD([sQuery(id+"F0.wireOp",EDGE,"E0.bottom"),sQuery(id+"F0.wireOp",EDGE,"E0.top"),sQuery(id+"F0.wireOp",EDGE,"E0.left"),sQuery(id+"F0.wireOp",EDGE,"E0.right"),sQuery(id+"F0.wireOp",EDGE,"E1.filletArc"),sQuery(id+"F0.wireOp",EDGE,"E2.filletArc"),sQuery(id+"F0.wireOp",EDGE,"E3.filletArc"),sQuery(id+"F0.wireOp",EDGE,"E4.filletArc"),sQuery(id+"F0.wireOp",EDGE,"E5.bottom"),sQuery(id+"F0.wireOp",EDGE,"E5.top"),sQuery(id+"F0.wireOp",EDGE,"E5.left"),sQuery(id+"F0.wireOp",EDGE,"E5.right"),sQuery(id+"F0.wireOp",EDGE,"E6.filletArc"),sQuery(id+"F0.wireOp",EDGE,"E7.filletArc"),sQuery(id+"F0.wireOp",EDGE,"E8.filletArc"),sQuery(id+"F0.wireOp",EDGE,"E9.filletArc"),sQuery(id+"F0.wireOp",EDGE,"E10.0.1.0"),sQuery(id+"F0.wireOp",EDGE,"E10.0.1.1"),sQuery(id+"F0.wireOp",EDGE,"E10.0.1.2"),sQuery(id+"F0.wireOp",EDGE,"E10.0.1.3"),sQuery(id+"F0.wireOp",EDGE,"E10.0.1.4"),sQuery(id+"F0.wireOp",EDGE,"E10.0.1.5"),sQuery(id+"F0.wireOp",EDGE,"E10.0.1.6"),sQuery(id+"F0.wireOp",EDGE,"E10.0.1.7"),sQuery(id+"F0.wireOp",EDGE,"E10.0.2.0"),sQuery(id+"F0.wireOp",EDGE,"E10.0.2.1"),sQuery(id+"F0.wireOp",EDGE,"E10.0.2.2"),sQuery(id+"F0.wireOp",EDGE,"E10.0.2.3"),sQuery(id+"F0.wireOp",EDGE,"E10.0.2.4"),sQuery(id+"F0.wireOp",EDGE,"E10.0.2.5"),sQuery(id+"F0.wireOp",EDGE,"E10.0.2.6"),sQuery(id+"F0.wireOp",EDGE,"E10.0.2.7"),sQuery(id+"F0.wireOp",EDGE,"E10.0.3.0"),sQuery(id+"F0.wireOp",EDGE,"E10.0.3.1"),sQuery(id+"F0.wireOp",EDGE,"E10.0.3.2"),sQuery(id+"F0.wireOp",EDGE,"E10.0.3.3"),sQuery(id+"F0.wireOp",EDGE,"E10.0.3.4"),sQuery(id+"F0.wireOp",EDGE,"E10.0.3.5"),sQuery(id+"F0.wireOp",EDGE,"E10.0.3.6"),sQuery(id+"F0.wireOp",EDGE,"E10.0.3.7"),sQuery(id+"F0.wireOp",EDGE,"E10.0.4.0"),sQuery(id+"F0.wireOp",EDGE,"E10.0.4.1"),sQuery(id+"F0.wireOp",EDGE,"E10.0.4.2"),sQuery(id+"F0.wireOp",EDGE,"E10.0.4.3"),sQuery(id+"F0.wireOp",EDGE,"E10.0.4.4"),sQuery(id+"F0.wireOp",EDGE,"E10.0.4.5"),sQuery(id+"F0.wireOp",EDGE,"E10.0.4.6"),sQuery(id+"F0.wireOp",EDGE,"E10.0.4.7"),sQuery(id+"F0.wireOp",EDGE,"E10.0.5.0"),sQuery(id+"F0.wireOp",EDGE,"E10.0.5.1"),sQuery(id+"F0.wireOp",EDGE,"E10.0.5.2"),sQuery(id+"F0.wireOp",EDGE,"E10.0.5.3"),sQuery(id+"F0.wireOp",EDGE,"E10.0.5.4"),sQuery(id+"F0.wireOp",EDGE,"E10.0.5.5"),sQuery(id+"F0.wireOp",EDGE,"E10.0.5.6"),sQuery(id+"F0.wireOp",EDGE,"E10.0.5.7"),sQuery(id+"F0.wireOp",EDGE,"E10.0.6.0"),sQuery(id+"F0.wireOp",EDGE,"E10.0.6.1"),sQuery(id+"F0.wireOp",EDGE,"E10.0.6.2"),sQuery(id+"F0.wireOp",EDGE,"E10.0.6.3"),sQuery(id+"F0.wireOp",EDGE,"E10.0.6.4"),sQuery(id+"F0.wireOp",EDGE,"E10.0.6.5"),sQuery(id+"F0.wireOp",EDGE,"E10.0.6.6"),sQuery(id+"F0.wireOp",EDGE,"E10.0.6.7"),sQuery(id+"F0.wireOp",EDGE,"E10.0.7.0"),sQuery(id+"F0.wireOp",EDGE,"E10.0.7.1"),sQuery(id+"F0.wireOp",EDGE,"E10.0.7.2"),sQuery(id+"F0.wireOp",EDGE,"E10.0.7.3"),sQuery(id+"F0.wireOp",EDGE,"E10.0.7.4"),sQuery(id+"F0.wireOp",EDGE,"E10.0.7.5"),sQuery(id+"F0.wireOp",EDGE,"E10.0.7.6"),sQuery(id+"F0.wireOp",EDGE,"E10.0.7.7"),sQuery(id+"F0.wireOp",EDGE,"E10.1.0.0"),sQuery(id+"F0.wireOp",EDGE,"E10.1.0.1"),sQuery(id+"F0.wireOp",EDGE,"E10.1.0.2"),sQuery(id+"F0.wireOp",EDGE,"E10.1.0.3"),sQuery(id+"F0.wireOp",EDGE,"E10.1.0.4"),sQuery(id+"F0.wireOp",EDGE,"E10.1.0.5"),sQuery(id+"F0.wireOp",EDGE,"E10.1.0.6"),sQuery(id+"F0.wireOp",EDGE,"E10.1.0.7"),sQuery(id+"F0.wireOp",EDGE,"E10.1.1.0"),sQuery(id+"F0.wireOp",EDGE,"E10.1.1.1"),sQuery(id+"F0.wireOp",EDGE,"E10.1.1.2"),sQuery(id+"F0.wireOp",EDGE,"E10.1.1.3"),sQuery(id+"F0.wireOp",EDGE,"E10.1.1.4"),sQuery(id+"F0.wireOp",EDGE,"E10.1.1.5"),sQuery(id+"F0.wireOp",EDGE,"E10.1.1.6"),sQuery(id+"F0.wireOp",EDGE,"E10.1.1.7"),sQuery(id+"F0.wireOp",EDGE,"E10.1.2.0"),sQuery(id+"F0.wireOp",EDGE,"E10.1.2.1"),sQuery(id+"F0.wireOp",EDGE,"E10.1.2.2"),sQuery(id+"F0.wireOp",EDGE,"E10.1.2.3"),sQuery(id+"F0.wireOp",EDGE,"E10.1.2.4"),sQuery(id+"F0.wireOp",EDGE,"E10.1.2.5"),sQuery(id+"F0.wireOp",EDGE,"E10.1.2.6"),sQuery(id+"F0.wireOp",EDGE,"E10.1.2.7"),sQuery(id+"F0.wireOp",EDGE,"E10.1.3.0"),sQuery(id+"F0.wireOp",EDGE,"E10.1.3.1"),sQuery(id+"F0.wireOp",EDGE,"E10.1.3.2"),sQuery(id+"F0.wireOp",EDGE,"E10.1.3.3"),sQuery(id+"F0.wireOp",EDGE,"E10.1.3.4"),sQuery(id+"F0.wireOp",EDGE,"E10.1.3.5"),sQuery(id+"F0.wireOp",EDGE,"E10.1.3.6"),sQuery(id+"F0.wireOp",EDGE,"E10.1.3.7"),sQuery(id+"F0.wireOp",EDGE,"E10.1.4.0"),sQuery(id+"F0.wireOp",EDGE,"E10.1.4.1"),sQuery(id+"F0.wireOp",EDGE,"E10.1.4.2"),sQuery(id+"F0.wireOp",EDGE,"E10.1.4.3"),sQuery(id+"F0.wireOp",EDGE,"E10.1.4.4"),sQuery(id+"F0.wireOp",EDGE,"E10.1.4.5"),sQuery(id+"F0.wireOp",EDGE,"E10.1.4.6"),sQuery(id+"F0.wireOp",EDGE,"E10.1.4.7"),sQuery(id+"F0.wireOp",EDGE,"E10.1.5.0"),sQuery(id+"F0.wireOp",EDGE,"E10.1.5.1"),sQuery(id+"F0.wireOp",EDGE,"E10.1.5.2"),sQuery(id+"F0.wireOp",EDGE,"E10.1.5.3"),sQuery(id+"F0.wireOp",EDGE,"E10.1.5.4"),sQuery(id+"F0.wireOp",EDGE,"E10.1.5.5"),sQuery(id+"F0.wireOp",EDGE,"E10.1.5.6"),sQuery(id+"F0.wireOp",EDGE,"E10.1.5.7"),sQuery(id+"F0.wireOp",EDGE,"E10.1.6.0"),sQuery(id+"F0.wireOp",EDGE,"E10.1.6.1"),sQuery(id+"F0.wireOp",EDGE,"E10.1.6.2"),sQuery(id+"F0.wireOp",EDGE,"E10.1.6.3"),sQuery(id+"F0.wireOp",EDGE,"E10.1.6.4"),sQuery(id+"F0.wireOp",EDGE,"E10.1.6.5"),sQuery(id+"F0.wireOp",EDGE,"E10.1.6.6"),sQuery(id+"F0.wireOp",EDGE,"E10.1.6.7"),sQuery(id+"F0.wireOp",EDGE,"E10.1.7.0"),sQuery(id+"F0.wireOp",EDGE,"E10.1.7.1"),sQuery(id+"F0.wireOp",EDGE,"E10.1.7.2"),sQuery(id+"F0.wireOp",EDGE,"E10.1.7.3"),sQuery(id+"F0.wireOp",EDGE,"E10.1.7.4"),sQuery(id+"F0.wireOp",EDGE,"E10.1.7.5"),sQuery(id+"F0.wireOp",EDGE,"E10.1.7.6"),sQuery(id+"F0.wireOp",EDGE,"E10.1.7.7"),sQuery(id+"F0.wireOp",EDGE,"E10.2.0.0"),sQuery(id+"F0.wireOp",EDGE,"E10.2.0.1"),sQuery(id+"F0.wireOp",EDGE,"E10.2.0.2"),sQuery(id+"F0.wireOp",EDGE,"E10.2.0.3"),sQuery(id+"F0.wireOp",EDGE,"E10.2.0.4"),sQuery(id+"F0.wireOp",EDGE,"E10.2.0.5"),sQuery(id+"F0.wireOp",EDGE,"E10.2.0.6"),sQuery(id+"F0.wireOp",EDGE,"E10.2.0.7"),sQuery(id+"F0.wireOp",EDGE,"E10.2.1.0"),sQuery(id+"F0.wireOp",EDGE,"E10.2.1.1"),sQuery(id+"F0.wireOp",EDGE,"E10.2.1.2"),sQuery(id+"F0.wireOp",EDGE,"E10.2.1.3"),sQuery(id+"F0.wireOp",EDGE,"E10.2.1.4"),sQuery(id+"F0.wireOp",EDGE,"E10.2.1.5"),sQuery(id+"F0.wireOp",EDGE,"E10.2.1.6"),sQuery(id+"F0.wireOp",EDGE,"E10.2.1.7"),sQuery(id+"F0.wireOp",EDGE,"E10.2.2.0"),sQuery(id+"F0.wireOp",EDGE,"E10.2.2.1"),sQuery(id+"F0.wireOp",EDGE,"E10.2.2.2"),sQuery(id+"F0.wireOp",EDGE,"E10.2.2.3"),sQuery(id+"F0.wireOp",EDGE,"E10.2.2.4"),sQuery(id+"F0.wireOp",EDGE,"E10.2.2.5"),sQuery(id+"F0.wireOp",EDGE,"E10.2.2.6"),sQuery(id+"F0.wireOp",EDGE,"E10.2.2.7"),sQuery(id+"F0.wireOp",EDGE,"E10.2.3.0"),sQuery(id+"F0.wireOp",EDGE,"E10.2.3.1"),sQuery(id+"F0.wireOp",EDGE,"E10.2.3.2"),sQuery(id+"F0.wireOp",EDGE,"E10.2.3.3"),sQuery(id+"F0.wireOp",EDGE,"E10.2.3.4"),sQuery(id+"F0.wireOp",EDGE,"E10.2.3.5"),sQuery(id+"F0.wireOp",EDGE,"E10.2.3.6"),sQuery(id+"F0.wireOp",EDGE,"E10.2.3.7"),sQuery(id+"F0.wireOp",EDGE,"E10.2.4.0"),sQuery(id+"F0.wireOp",EDGE,"E10.2.4.1"),sQuery(id+"F0.wireOp",EDGE,"E10.2.4.2"),sQuery(id+"F0.wireOp",EDGE,"E10.2.4.3"),sQuery(id+"F0.wireOp",EDGE,"E10.2.4.4"),sQuery(id+"F0.wireOp",EDGE,"E10.2.4.5"),sQuery(id+"F0.wireOp",EDGE,"E10.2.4.6"),sQuery(id+"F0.wireOp",EDGE,"E10.2.4.7"),sQuery(id+"F0.wireOp",EDGE,"E10.2.5.0"),sQuery(id+"F0.wireOp",EDGE,"E10.2.5.1"),sQuery(id+"F0.wireOp",EDGE,"E10.2.5.2"),sQuery(id+"F0.wireOp",EDGE,"E10.2.5.3"),sQuery(id+"F0.wireOp",EDGE,"E10.2.5.4"),sQuery(id+"F0.wireOp",EDGE,"E10.2.5.5"),sQuery(id+"F0.wireOp",EDGE,"E10.2.5.6"),sQuery(id+"F0.wireOp",EDGE,"E10.2.5.7"),sQuery(id+"F0.wireOp",EDGE,"E10.2.6.0"),sQuery(id+"F0.wireOp",EDGE,"E10.2.6.1"),sQuery(id+"F0.wireOp",EDGE,"E10.2.6.2"),sQuery(id+"F0.wireOp",EDGE,"E10.2.6.3"),sQuery(id+"F0.wireOp",EDGE,"E10.2.6.4"),sQuery(id+"F0.wireOp",EDGE,"E10.2.6.5"),sQuery(id+"F0.wireOp",EDGE,"E10.2.6.6"),sQuery(id+"F0.wireOp",EDGE,"E10.2.6.7"),sQuery(id+"F0.wireOp",EDGE,"E10.2.7.0"),sQuery(id+"F0.wireOp",EDGE,"E10.2.7.1"),sQuery(id+"F0.wireOp",EDGE,"E10.2.7.2"),sQuery(id+"F0.wireOp",EDGE,"E10.2.7.3"),sQuery(id+"F0.wireOp",EDGE,"E10.2.7.4"),sQuery(id+"F0.wireOp",EDGE,"E10.2.7.5"),sQuery(id+"F0.wireOp",EDGE,"E10.2.7.6"),sQuery(id+"F0.wireOp",EDGE,"E10.2.7.7"),sQuery(id+"F0.wireOp",EDGE,"E10.3.0.0"),sQuery(id+"F0.wireOp",EDGE,"E10.3.0.1"),sQuery(id+"F0.wireOp",EDGE,"E10.3.0.2"),sQuery(id+"F0.wireOp",EDGE,"E10.3.0.3"),sQuery(id+"F0.wireOp",EDGE,"E10.3.0.4"),sQuery(id+"F0.wireOp",EDGE,"E10.3.0.5"),sQuery(id+"F0.wireOp",EDGE,"E10.3.0.6"),sQuery(id+"F0.wireOp",EDGE,"E10.3.0.7"),sQuery(id+"F0.wireOp",EDGE,"E10.3.1.0"),sQuery(id+"F0.wireOp",EDGE,"E10.3.1.1"),sQuery(id+"F0.wireOp",EDGE,"E10.3.1.2"),sQuery(id+"F0.wireOp",EDGE,"E10.3.1.3"),sQuery(id+"F0.wireOp",EDGE,"E10.3.1.4"),sQuery(id+"F0.wireOp",EDGE,"E10.3.1.5"),sQuery(id+"F0.wireOp",EDGE,"E10.3.1.6"),sQuery(id+"F0.wireOp",EDGE,"E10.3.1.7"),sQuery(id+"F0.wireOp",EDGE,"E10.3.2.0"),sQuery(id+"F0.wireOp",EDGE,"E10.3.2.1"),sQuery(id+"F0.wireOp",EDGE,"E10.3.2.2"),sQuery(id+"F0.wireOp",EDGE,"E10.3.2.3"),sQuery(id+"F0.wireOp",EDGE,"E10.3.2.4"),sQuery(id+"F0.wireOp",EDGE,"E10.3.2.5"),sQuery(id+"F0.wireOp",EDGE,"E10.3.2.6"),sQuery(id+"F0.wireOp",EDGE,"E10.3.2.7"),sQuery(id+"F0.wireOp",EDGE,"E10.3.3.0"),sQuery(id+"F0.wireOp",EDGE,"E10.3.3.1"),sQuery(id+"F0.wireOp",EDGE,"E10.3.3.2"),sQuery(id+"F0.wireOp",EDGE,"E10.3.3.3"),sQuery(id+"F0.wireOp",EDGE,"E10.3.3.4"),sQuery(id+"F0.wireOp",EDGE,"E10.3.3.5"),sQuery(id+"F0.wireOp",EDGE,"E10.3.3.6"),sQuery(id+"F0.wireOp",EDGE,"E10.3.3.7"),sQuery(id+"F0.wireOp",EDGE,"E10.3.4.0"),sQuery(id+"F0.wireOp",EDGE,"E10.3.4.1"),sQuery(id+"F0.wireOp",EDGE,"E10.3.4.2"),sQuery(id+"F0.wireOp",EDGE,"E10.3.4.3"),sQuery(id+"F0.wireOp",EDGE,"E10.3.4.4"),sQuery(id+"F0.wireOp",EDGE,"E10.3.4.5"),sQuery(id+"F0.wireOp",EDGE,"E10.3.4.6"),sQuery(id+"F0.wireOp",EDGE,"E10.3.4.7"),sQuery(id+"F0.wireOp",EDGE,"E10.3.5.0"),sQuery(id+"F0.wireOp",EDGE,"E10.3.5.1"),sQuery(id+"F0.wireOp",EDGE,"E10.3.5.2"),sQuery(id+"F0.wireOp",EDGE,"E10.3.5.3"),sQuery(id+"F0.wireOp",EDGE,"E10.3.5.4"),sQuery(id+"F0.wireOp",EDGE,"E10.3.5.5"),sQuery(id+"F0.wireOp",EDGE,"E10.3.5.6"),sQuery(id+"F0.wireOp",EDGE,"E10.3.5.7"),sQuery(id+"F0.wireOp",EDGE,"E10.3.6.0"),sQuery(id+"F0.wireOp",EDGE,"E10.3.6.1"),sQuery(id+"F0.wireOp",EDGE,"E10.3.6.2"),sQuery(id+"F0.wireOp",EDGE,"E10.3.6.3"),sQuery(id+"F0.wireOp",EDGE,"E10.3.6.4"),sQuery(id+"F0.wireOp",EDGE,"E10.3.6.5"),sQuery(id+"F0.wireOp",EDGE,"E10.3.6.6"),sQuery(id+"F0.wireOp",EDGE,"E10.3.6.7"),sQuery(id+"F0.wireOp",EDGE,"E10.3.7.0"),sQuery(id+"F0.wireOp",EDGE,"E10.3.7.1"),sQuery(id+"F0.wireOp",EDGE,"E10.3.7.2"),sQuery(id+"F0.wireOp",EDGE,"E10.3.7.3"),sQuery(id+"F0.wireOp",EDGE,"E10.3.7.4"),sQuery(id+"F0.wireOp",EDGE,"E10.3.7.5"),sQuery(id+"F0.wireOp",EDGE,"E10.3.7.6"),sQuery(id+"F0.wireOp",EDGE,"E10.3.7.7"),sQuery(id+"F0.wireOp",EDGE,"E10.4.0.0"),sQuery(id+"F0.wireOp",EDGE,"E10.4.0.1"),sQuery(id+"F0.wireOp",EDGE,"E10.4.0.2"),sQuery(id+"F0.wireOp",EDGE,"E10.4.0.3"),sQuery(id+"F0.wireOp",EDGE,"E10.4.0.4"),sQuery(id+"F0.wireOp",EDGE,"E10.4.0.5"),sQuery(id+"F0.wireOp",EDGE,"E10.4.0.6"),sQuery(id+"F0.wireOp",EDGE,"E10.4.0.7"),sQuery(id+"F0.wireOp",EDGE,"E10.4.1.0"),sQuery(id+"F0.wireOp",EDGE,"E10.4.1.1"),sQuery(id+"F0.wireOp",EDGE,"E10.4.1.2"),sQuery(id+"F0.wireOp",EDGE,"E10.4.1.3"),sQuery(id+"F0.wireOp",EDGE,"E10.4.1.4"),sQuery(id+"F0.wireOp",EDGE,"E10.4.1.5"),sQuery(id+"F0.wireOp",EDGE,"E10.4.1.6"),sQuery(id+"F0.wireOp",EDGE,"E10.4.1.7"),sQuery(id+"F0.wireOp",EDGE,"E10.4.2.0"),sQuery(id+"F0.wireOp",EDGE,"E10.4.2.1"),sQuery(id+"F0.wireOp",EDGE,"E10.4.2.2"),sQuery(id+"F0.wireOp",EDGE,"E10.4.2.3"),sQuery(id+"F0.wireOp",EDGE,"E10.4.2.4"),sQuery(id+"F0.wireOp",EDGE,"E10.4.2.5"),sQuery(id+"F0.wireOp",EDGE,"E10.4.2.6"),sQuery(id+"F0.wireOp",EDGE,"E10.4.2.7"),sQuery(id+"F0.wireOp",EDGE,"E10.4.3.0"),sQuery(id+"F0.wireOp",EDGE,"E10.4.3.1"),sQuery(id+"F0.wireOp",EDGE,"E10.4.3.2"),sQuery(id+"F0.wireOp",EDGE,"E10.4.3.3"),sQuery(id+"F0.wireOp",EDGE,"E10.4.3.4"),sQuery(id+"F0.wireOp",EDGE,"E10.4.3.5"),sQuery(id+"F0.wireOp",EDGE,"E10.4.3.6"),sQuery(id+"F0.wireOp",EDGE,"E10.4.3.7"),sQuery(id+"F0.wireOp",EDGE,"E10.4.4.0"),sQuery(id+"F0.wireOp",EDGE,"E10.4.4.1"),sQuery(id+"F0.wireOp",EDGE,"E10.4.4.2"),sQuery(id+"F0.wireOp",EDGE,"E10.4.4.3"),sQuery(id+"F0.wireOp",EDGE,"E10.4.4.4"),sQuery(id+"F0.wireOp",EDGE,"E10.4.4.5"),sQuery(id+"F0.wireOp",EDGE,"E10.4.4.6"),sQuery(id+"F0.wireOp",EDGE,"E10.4.4.7"),sQuery(id+"F0.wireOp",EDGE,"E10.4.5.0"),sQuery(id+"F0.wireOp",EDGE,"E10.4.5.1"),sQuery(id+"F0.wireOp",EDGE,"E10.4.5.2"),sQuery(id+"F0.wireOp",EDGE,"E10.4.5.3"),sQuery(id+"F0.wireOp",EDGE,"E10.4.5.4"),sQuery(id+"F0.wireOp",EDGE,"E10.4.5.5"),sQuery(id+"F0.wireOp",EDGE,"E10.4.5.6"),sQuery(id+"F0.wireOp",EDGE,"E10.4.5.7"),sQuery(id+"F0.wireOp",EDGE,"E10.4.6.0"),sQuery(id+"F0.wireOp",EDGE,"E10.4.6.1"),sQuery(id+"F0.wireOp",EDGE,"E10.4.6.2"),sQuery(id+"F0.wireOp",EDGE,"E10.4.6.3"),sQuery(id+"F0.wireOp",EDGE,"E10.4.6.4"),sQuery(id+"F0.wireOp",EDGE,"E10.4.6.5"),sQuery(id+"F0.wireOp",EDGE,"E10.4.6.6"),sQuery(id+"F0.wireOp",EDGE,"E10.4.6.7"),sQuery(id+"F0.wireOp",EDGE,"E10.4.7.0"),sQuery(id+"F0.wireOp",EDGE,"E10.4.7.1"),sQuery(id+"F0.wireOp",EDGE,"E10.4.7.2"),sQuery(id+"F0.wireOp",EDGE,"E10.4.7.3"),sQuery(id+"F0.wireOp",EDGE,"E10.4.7.4"),sQuery(id+"F0.wireOp",EDGE,"E10.4.7.5"),sQuery(id+"F0.wireOp",EDGE,"E10.4.7.6"),sQuery(id+"F0.wireOp",EDGE,"E10.4.7.7"),sQuery(id+"F0.wireOp",EDGE,"E10.5.0.0"),sQuery(id+"F0.wireOp",EDGE,"E10.5.0.1"),sQuery(id+"F0.wireOp",EDGE,"E10.5.0.2"),sQuery(id+"F0.wireOp",EDGE,"E10.5.0.3"),sQuery(id+"F0.wireOp",EDGE,"E10.5.0.4"),sQuery(id+"F0.wireOp",EDGE,"E10.5.0.5"),sQuery(id+"F0.wireOp",EDGE,"E10.5.0.6"),sQuery(id+"F0.wireOp",EDGE,"E10.5.0.7"),sQuery(id+"F0.wireOp",EDGE,"E10.5.1.0"),sQuery(id+"F0.wireOp",EDGE,"E10.5.1.1"),sQuery(id+"F0.wireOp",EDGE,"E10.5.1.2"),sQuery(id+"F0.wireOp",EDGE,"E10.5.1.3"),sQuery(id+"F0.wireOp",EDGE,"E10.5.1.4"),sQuery(id+"F0.wireOp",EDGE,"E10.5.1.5"),sQuery(id+"F0.wireOp",EDGE,"E10.5.1.6"),sQuery(id+"F0.wireOp",EDGE,"E10.5.1.7"),sQuery(id+"F0.wireOp",EDGE,"E10.5.2.0"),sQuery(id+"F0.wireOp",EDGE,"E10.5.2.1"),sQuery(id+"F0.wireOp",EDGE,"E10.5.2.2"),sQuery(id+"F0.wireOp",EDGE,"E10.5.2.3"),sQuery(id+"F0.wireOp",EDGE,"E10.5.2.4"),sQuery(id+"F0.wireOp",EDGE,"E10.5.2.5"),sQuery(id+"F0.wireOp",EDGE,"E10.5.2.6"),sQuery(id+"F0.wireOp",EDGE,"E10.5.2.7"),sQuery(id+"F0.wireOp",EDGE,"E10.5.3.0"),sQuery(id+"F0.wireOp",EDGE,"E10.5.3.1"),sQuery(id+"F0.wireOp",EDGE,"E10.5.3.2"),sQuery(id+"F0.wireOp",EDGE,"E10.5.3.3"),sQuery(id+"F0.wireOp",EDGE,"E10.5.3.4"),sQuery(id+"F0.wireOp",EDGE,"E10.5.3.5"),sQuery(id+"F0.wireOp",EDGE,"E10.5.3.6"),sQuery(id+"F0.wireOp",EDGE,"E10.5.3.7"),sQuery(id+"F0.wireOp",EDGE,"E10.5.4.0"),sQuery(id+"F0.wireOp",EDGE,"E10.5.4.1"),sQuery(id+"F0.wireOp",EDGE,"E10.5.4.2"),sQuery(id+"F0.wireOp",EDGE,"E10.5.4.3"),sQuery(id+"F0.wireOp",EDGE,"E10.5.4.4"),sQuery(id+"F0.wireOp",EDGE,"E10.5.4.5"),sQuery(id+"F0.wireOp",EDGE,"E10.5.4.6"),sQuery(id+"F0.wireOp",EDGE,"E10.5.4.7"),sQuery(id+"F0.wireOp",EDGE,"E10.5.5.0"),sQuery(id+"F0.wireOp",EDGE,"E10.5.5.1"),sQuery(id+"F0.wireOp",EDGE,"E10.5.5.2"),sQuery(id+"F0.wireOp",EDGE,"E10.5.5.3"),sQuery(id+"F0.wireOp",EDGE,"E10.5.5.4"),sQuery(id+"F0.wireOp",EDGE,"E10.5.5.5"),sQuery(id+"F0.wireOp",EDGE,"E10.5.5.6"),sQuery(id+"F0.wireOp",EDGE,"E10.5.5.7"),sQuery(id+"F0.wireOp",EDGE,"E10.5.6.0"),sQuery(id+"F0.wireOp",EDGE,"E10.5.6.1"),sQuery(id+"F0.wireOp",EDGE,"E10.5.6.2"),sQuery(id+"F0.wireOp",EDGE,"E10.5.6.3"),sQuery(id+"F0.wireOp",EDGE,"E10.5.6.4"),sQuery(id+"F0.wireOp",EDGE,"E10.5.6.5"),sQuery(id+"F0.wireOp",EDGE,"E10.5.6.6"),sQuery(id+"F0.wireOp",EDGE,"E10.5.6.7"),sQuery(id+"F0.wireOp",EDGE,"E10.5.7.0"),sQuery(id+"F0.wireOp",EDGE,"E10.5.7.1"),sQuery(id+"F0.wireOp",EDGE,"E10.5.7.2"),sQuery(id+"F0.wireOp",EDGE,"E10.5.7.3"),sQuery(id+"F0.wireOp",EDGE,"E10.5.7.4"),sQuery(id+"F0.wireOp",EDGE,"E10.5.7.5"),sQuery(id+"F0.wireOp",EDGE,"E10.5.7.6"),sQuery(id+"F0.wireOp",EDGE,"E10.5.7.7"),sQuery(id+"F0.wireOp",EDGE,"E10.6.0.0"),sQuery(id+"F0.wireOp",EDGE,"E10.6.0.1"),sQuery(id+"F0.wireOp",EDGE,"E10.6.0.2"),sQuery(id+"F0.wireOp",EDGE,"E10.6.0.3"),sQuery(id+"F0.wireOp",EDGE,"E10.6.0.4"),sQuery(id+"F0.wireOp",EDGE,"E10.6.0.5"),sQuery(id+"F0.wireOp",EDGE,"E10.6.0.6"),sQuery(id+"F0.wireOp",EDGE,"E10.6.0.7"),sQuery(id+"F0.wireOp",EDGE,"E10.6.1.0"),sQuery(id+"F0.wireOp",EDGE,"E10.6.1.1"),sQuery(id+"F0.wireOp",EDGE,"E10.6.1.2"),sQuery(id+"F0.wireOp",EDGE,"E10.6.1.3"),sQuery(id+"F0.wireOp",EDGE,"E10.6.1.4"),sQuery(id+"F0.wireOp",EDGE,"E10.6.1.5"),sQuery(id+"F0.wireOp",EDGE,"E10.6.1.6"),sQuery(id+"F0.wireOp",EDGE,"E10.6.1.7"),sQuery(id+"F0.wireOp",EDGE,"E10.6.2.0"),sQuery(id+"F0.wireOp",EDGE,"E10.6.2.1"),sQuery(id+"F0.wireOp",EDGE,"E10.6.2.2"),sQuery(id+"F0.wireOp",EDGE,"E10.6.2.3"),sQuery(id+"F0.wireOp",EDGE,"E10.6.2.4"),sQuery(id+"F0.wireOp",EDGE,"E10.6.2.5"),sQuery(id+"F0.wireOp",EDGE,"E10.6.2.6"),sQuery(id+"F0.wireOp",EDGE,"E10.6.2.7"),sQuery(id+"F0.wireOp",EDGE,"E10.6.3.0"),sQuery(id+"F0.wireOp",EDGE,"E10.6.3.1"),sQuery(id+"F0.wireOp",EDGE,"E10.6.3.2"),sQuery(id+"F0.wireOp",EDGE,"E10.6.3.3"),sQuery(id+"F0.wireOp",EDGE,"E10.6.3.4"),sQuery(id+"F0.wireOp",EDGE,"E10.6.3.5"),sQuery(id+"F0.wireOp",EDGE,"E10.6.3.6"),sQuery(id+"F0.wireOp",EDGE,"E10.6.3.7"),sQuery(id+"F0.wireOp",EDGE,"E10.6.4.0"),sQuery(id+"F0.wireOp",EDGE,"E10.6.4.1"),sQuery(id+"F0.wireOp",EDGE,"E10.6.4.2"),sQuery(id+"F0.wireOp",EDGE,"E10.6.4.3"),sQuery(id+"F0.wireOp",EDGE,"E10.6.4.4"),sQuery(id+"F0.wireOp",EDGE,"E10.6.4.5"),sQuery(id+"F0.wireOp",EDGE,"E10.6.4.6"),sQuery(id+"F0.wireOp",EDGE,"E10.6.4.7"),sQuery(id+"F0.wireOp",EDGE,"E10.6.5.0"),sQuery(id+"F0.wireOp",EDGE,"E10.6.5.1"),sQuery(id+"F0.wireOp",EDGE,"E10.6.5.2"),sQuery(id+"F0.wireOp",EDGE,"E10.6.5.3"),sQuery(id+"F0.wireOp",EDGE,"E10.6.5.4"),sQuery(id+"F0.wireOp",EDGE,"E10.6.5.5"),sQuery(id+"F0.wireOp",EDGE,"E10.6.5.6"),sQuery(id+"F0.wireOp",EDGE,"E10.6.5.7"),sQuery(id+"F0.wireOp",EDGE,"E10.6.6.0"),sQuery(id+"F0.wireOp",EDGE,"E10.6.6.1"),sQuery(id+"F0.wireOp",EDGE,"E10.6.6.2"),sQuery(id+"F0.wireOp",EDGE,"E10.6.6.3"),sQuery(id+"F0.wireOp",EDGE,"E10.6.6.4"),sQuery(id+"F0.wireOp",EDGE,"E10.6.6.5"),sQuery(id+"F0.wireOp",EDGE,"E10.6.6.6"),sQuery(id+"F0.wireOp",EDGE,"E10.6.6.7"),sQuery(id+"F0.wireOp",EDGE,"E10.6.7.0"),sQuery(id+"F0.wireOp",EDGE,"E10.6.7.1"),sQuery(id+"F0.wireOp",EDGE,"E10.6.7.2"),sQuery(id+"F0.wireOp",EDGE,"E10.6.7.3"),sQuery(id+"F0.wireOp",EDGE,"E10.6.7.4"),sQuery(id+"F0.wireOp",EDGE,"E10.6.7.5"),sQuery(id+"F0.wireOp",EDGE,"E10.6.7.6"),sQuery(id+"F0.wireOp",EDGE,"E10.6.7.7"),sQuery(id+"F0.wireOp",EDGE,"E10.7.0.0"),sQuery(id+"F0.wireOp",EDGE,"E10.7.0.1"),sQuery(id+"F0.wireOp",EDGE,"E10.7.0.2"),sQuery(id+"F0.wireOp",EDGE,"E10.7.0.3"),sQuery(id+"F0.wireOp",EDGE,"E10.7.0.4"),sQuery(id+"F0.wireOp",EDGE,"E10.7.0.5"),sQuery(id+"F0.wireOp",EDGE,"E10.7.0.6"),sQuery(id+"F0.wireOp",EDGE,"E10.7.0.7"),sQuery(id+"F0.wireOp",EDGE,"E10.7.1.0"),sQuery(id+"F0.wireOp",EDGE,"E10.7.1.1"),sQuery(id+"F0.wireOp",EDGE,"E10.7.1.2"),sQuery(id+"F0.wireOp",EDGE,"E10.7.1.3"),sQuery(id+"F0.wireOp",EDGE,"E10.7.1.4"),sQuery(id+"F0.wireOp",EDGE,"E10.7.1.5"),sQuery(id+"F0.wireOp",EDGE,"E10.7.1.6"),sQuery(id+"F0.wireOp",EDGE,"E10.7.1.7"),sQuery(id+"F0.wireOp",EDGE,"E10.7.2.0"),sQuery(id+"F0.wireOp",EDGE,"E10.7.2.1"),sQuery(id+"F0.wireOp",EDGE,"E10.7.2.2"),sQuery(id+"F0.wireOp",EDGE,"E10.7.2.3"),sQuery(id+"F0.wireOp",EDGE,"E10.7.2.4"),sQuery(id+"F0.wireOp",EDGE,"E10.7.2.5"),sQuery(id+"F0.wireOp",EDGE,"E10.7.2.6"),sQuery(id+"F0.wireOp",EDGE,"E10.7.2.7"),sQuery(id+"F0.wireOp",EDGE,"E10.7.3.0"),sQuery(id+"F0.wireOp",EDGE,"E10.7.3.1"),sQuery(id+"F0.wireOp",EDGE,"E10.7.3.2"),sQuery(id+"F0.wireOp",EDGE,"E10.7.3.3"),sQuery(id+"F0.wireOp",EDGE,"E10.7.3.4"),sQuery(id+"F0.wireOp",EDGE,"E10.7.3.5"),sQuery(id+"F0.wireOp",EDGE,"E10.7.3.6"),sQuery(id+"F0.wireOp",EDGE,"E10.7.3.7"),sQuery(id+"F0.wireOp",EDGE,"E10.7.4.0"),sQuery(id+"F0.wireOp",EDGE,"E10.7.4.1"),sQuery(id+"F0.wireOp",EDGE,"E10.7.4.2"),sQuery(id+"F0.wireOp",EDGE,"E10.7.4.3"),sQuery(id+"F0.wireOp",EDGE,"E10.7.4.4"),sQuery(id+"F0.wireOp",EDGE,"E10.7.4.5"),sQuery(id+"F0.wireOp",EDGE,"E10.7.4.6"),sQuery(id+"F0.wireOp",EDGE,"E10.7.4.7"),sQuery(id+"F0.wireOp",EDGE,"E10.7.5.0"),sQuery(id+"F0.wireOp",EDGE,"E10.7.5.1"),sQuery(id+"F0.wireOp",EDGE,"E10.7.5.2"),sQuery(id+"F0.wireOp",EDGE,"E10.7.5.3"),sQuery(id+"F0.wireOp",EDGE,"E10.7.5.4"),sQuery(id+"F0.wireOp",EDGE,"E10.7.5.5"),sQuery(id+"F0.wireOp",EDGE,"E10.7.5.6"),sQuery(id+"F0.wireOp",EDGE,"E10.7.5.7"),sQuery(id+"F0.wireOp",EDGE,"E10.7.6.0"),sQuery(id+"F0.wireOp",EDGE,"E10.7.6.1"),sQuery(id+"F0.wireOp",EDGE,"E10.7.6.2"),sQuery(id+"F0.wireOp",EDGE,"E10.7.6.3"),sQuery(id+"F0.wireOp",EDGE,"E10.7.6.4"),sQuery(id+"F0.wireOp",EDGE,"E10.7.6.5"),sQuery(id+"F0.wireOp",EDGE,"E10.7.6.6"),sQuery(id+"F0.wireOp",EDGE,"E10.7.6.7"),sQuery(id+"F0.wireOp",EDGE,"E10.7.7.0"),sQuery(id+"F0.wireOp",EDGE,"E10.7.7.1"),sQuery(id+"F0.wireOp",EDGE,"E10.7.7.2"),sQuery(id+"F0.wireOp",EDGE,"E10.7.7.3"),sQuery(id+"F0.wireOp",EDGE,"E10.7.7.4"),sQuery(id+"F0.wireOp",EDGE,"E10.7.7.5"),sQuery(id+"F0.wireOp",EDGE,"E10.7.7.6"),sQuery(id+"F0.wireOp",EDGE,"E10.7.7.7")])],"isStart":false});
            fillet(context, id + "F2", {"entities" : qUnion([Q0]), "radius" : 0.25 * mm, "tangentPropagation" : true, "allowEdgeOverflow" : false});
        }
        {
            var Q0;
            Q0=makeQuery(id+"F1.opExtrude","CAP_FACE",FACE,{"disambiguationData":[OSD([sQuery(id+"F0.wireOp",EDGE,"E0.bottom"),sQuery(id+"F0.wireOp",EDGE,"E0.top"),sQuery(id+"F0.wireOp",EDGE,"E0.left"),sQuery(id+"F0.wireOp",EDGE,"E0.right"),sQuery(id+"F0.wireOp",EDGE,"E1.filletArc"),sQuery(id+"F0.wireOp",EDGE,"E2.filletArc"),sQuery(id+"F0.wireOp",EDGE,"E3.filletArc"),sQuery(id+"F0.wireOp",EDGE,"E4.filletArc"),sQuery(id+"F0.wireOp",EDGE,"E5.bottom"),sQuery(id+"F0.wireOp",EDGE,"E5.top"),sQuery(id+"F0.wireOp",EDGE,"E5.left"),sQuery(id+"F0.wireOp",EDGE,"E5.right"),sQuery(id+"F0.wireOp",EDGE,"E6.filletArc"),sQuery(id+"F0.wireOp",EDGE,"E7.filletArc"),sQuery(id+"F0.wireOp",EDGE,"E8.filletArc"),sQuery(id+"F0.wireOp",EDGE,"E9.filletArc"),sQuery(id+"F0.wireOp",EDGE,"E10.0.1.0"),sQuery(id+"F0.wireOp",EDGE,"E10.0.1.1"),sQuery(id+"F0.wireOp",EDGE,"E10.0.1.2"),sQuery(id+"F0.wireOp",EDGE,"E10.0.1.3"),sQuery(id+"F0.wireOp",EDGE,"E10.0.1.4"),sQuery(id+"F0.wireOp",EDGE,"E10.0.1.5"),sQuery(id+"F0.wireOp",EDGE,"E10.0.1.6"),sQuery(id+"F0.wireOp",EDGE,"E10.0.1.7"),sQuery(id+"F0.wireOp",EDGE,"E10.0.2.0"),sQuery(id+"F0.wireOp",EDGE,"E10.0.2.1"),sQuery(id+"F0.wireOp",EDGE,"E10.0.2.2"),sQuery(id+"F0.wireOp",EDGE,"E10.0.2.3"),sQuery(id+"F0.wireOp",EDGE,"E10.0.2.4"),sQuery(id+"F0.wireOp",EDGE,"E10.0.2.5"),sQuery(id+"F0.wireOp",EDGE,"E10.0.2.6"),sQuery(id+"F0.wireOp",EDGE,"E10.0.2.7"),sQuery(id+"F0.wireOp",EDGE,"E10.0.3.0"),sQuery(id+"F0.wireOp",EDGE,"E10.0.3.1"),sQuery(id+"F0.wireOp",EDGE,"E10.0.3.2"),sQuery(id+"F0.wireOp",EDGE,"E10.0.3.3"),sQuery(id+"F0.wireOp",EDGE,"E10.0.3.4"),sQuery(id+"F0.wireOp",EDGE,"E10.0.3.5"),sQuery(id+"F0.wireOp",EDGE,"E10.0.3.6"),sQuery(id+"F0.wireOp",EDGE,"E10.0.3.7"),sQuery(id+"F0.wireOp",EDGE,"E10.0.4.0"),sQuery(id+"F0.wireOp",EDGE,"E10.0.4.1"),sQuery(id+"F0.wireOp",EDGE,"E10.0.4.2"),sQuery(id+"F0.wireOp",EDGE,"E10.0.4.3"),sQuery(id+"F0.wireOp",EDGE,"E10.0.4.4"),sQuery(id+"F0.wireOp",EDGE,"E10.0.4.5"),sQuery(id+"F0.wireOp",EDGE,"E10.0.4.6"),sQuery(id+"F0.wireOp",EDGE,"E10.0.4.7"),sQuery(id+"F0.wireOp",EDGE,"E10.0.5.0"),sQuery(id+"F0.wireOp",EDGE,"E10.0.5.1"),sQuery(id+"F0.wireOp",EDGE,"E10.0.5.2"),sQuery(id+"F0.wireOp",EDGE,"E10.0.5.3"),sQuery(id+"F0.wireOp",EDGE,"E10.0.5.4"),sQuery(id+"F0.wireOp",EDGE,"E10.0.5.5"),sQuery(id+"F0.wireOp",EDGE,"E10.0.5.6"),sQuery(id+"F0.wireOp",EDGE,"E10.0.5.7"),sQuery(id+"F0.wireOp",EDGE,"E10.0.6.0"),sQuery(id+"F0.wireOp",EDGE,"E10.0.6.1"),sQuery(id+"F0.wireOp",EDGE,"E10.0.6.2"),sQuery(id+"F0.wireOp",EDGE,"E10.0.6.3"),sQuery(id+"F0.wireOp",EDGE,"E10.0.6.4"),sQuery(id+"F0.wireOp",EDGE,"E10.0.6.5"),sQuery(id+"F0.wireOp",EDGE,"E10.0.6.6"),sQuery(id+"F0.wireOp",EDGE,"E10.0.6.7"),sQuery(id+"F0.wireOp",EDGE,"E10.0.7.0"),sQuery(id+"F0.wireOp",EDGE,"E10.0.7.1"),sQuery(id+"F0.wireOp",EDGE,"E10.0.7.2"),sQuery(id+"F0.wireOp",EDGE,"E10.0.7.3"),sQuery(id+"F0.wireOp",EDGE,"E10.0.7.4"),sQuery(id+"F0.wireOp",EDGE,"E10.0.7.5"),sQuery(id+"F0.wireOp",EDGE,"E10.0.7.6"),sQuery(id+"F0.wireOp",EDGE,"E10.0.7.7"),sQuery(id+"F0.wireOp",EDGE,"E10.1.0.0"),sQuery(id+"F0.wireOp",EDGE,"E10.1.0.1"),sQuery(id+"F0.wireOp",EDGE,"E10.1.0.2"),sQuery(id+"F0.wireOp",EDGE,"E10.1.0.3"),sQuery(id+"F0.wireOp",EDGE,"E10.1.0.4"),sQuery(id+"F0.wireOp",EDGE,"E10.1.0.5"),sQuery(id+"F0.wireOp",EDGE,"E10.1.0.6"),sQuery(id+"F0.wireOp",EDGE,"E10.1.0.7"),sQuery(id+"F0.wireOp",EDGE,"E10.1.1.0"),sQuery(id+"F0.wireOp",EDGE,"E10.1.1.1"),sQuery(id+"F0.wireOp",EDGE,"E10.1.1.2"),sQuery(id+"F0.wireOp",EDGE,"E10.1.1.3"),sQuery(id+"F0.wireOp",EDGE,"E10.1.1.4"),sQuery(id+"F0.wireOp",EDGE,"E10.1.1.5"),sQuery(id+"F0.wireOp",EDGE,"E10.1.1.6"),sQuery(id+"F0.wireOp",EDGE,"E10.1.1.7"),sQuery(id+"F0.wireOp",EDGE,"E10.1.2.0"),sQuery(id+"F0.wireOp",EDGE,"E10.1.2.1"),sQuery(id+"F0.wireOp",EDGE,"E10.1.2.2"),sQuery(id+"F0.wireOp",EDGE,"E10.1.2.3"),sQuery(id+"F0.wireOp",EDGE,"E10.1.2.4"),sQuery(id+"F0.wireOp",EDGE,"E10.1.2.5"),sQuery(id+"F0.wireOp",EDGE,"E10.1.2.6"),sQuery(id+"F0.wireOp",EDGE,"E10.1.2.7"),sQuery(id+"F0.wireOp",EDGE,"E10.1.3.0"),sQuery(id+"F0.wireOp",EDGE,"E10.1.3.1"),sQuery(id+"F0.wireOp",EDGE,"E10.1.3.2"),sQuery(id+"F0.wireOp",EDGE,"E10.1.3.3"),sQuery(id+"F0.wireOp",EDGE,"E10.1.3.4"),sQuery(id+"F0.wireOp",EDGE,"E10.1.3.5"),sQuery(id+"F0.wireOp",EDGE,"E10.1.3.6"),sQuery(id+"F0.wireOp",EDGE,"E10.1.3.7"),sQuery(id+"F0.wireOp",EDGE,"E10.1.4.0"),sQuery(id+"F0.wireOp",EDGE,"E10.1.4.1"),sQuery(id+"F0.wireOp",EDGE,"E10.1.4.2"),sQuery(id+"F0.wireOp",EDGE,"E10.1.4.3"),sQuery(id+"F0.wireOp",EDGE,"E10.1.4.4"),sQuery(id+"F0.wireOp",EDGE,"E10.1.4.5"),sQuery(id+"F0.wireOp",EDGE,"E10.1.4.6"),sQuery(id+"F0.wireOp",EDGE,"E10.1.4.7"),sQuery(id+"F0.wireOp",EDGE,"E10.1.5.0"),sQuery(id+"F0.wireOp",EDGE,"E10.1.5.1"),sQuery(id+"F0.wireOp",EDGE,"E10.1.5.2"),sQuery(id+"F0.wireOp",EDGE,"E10.1.5.3"),sQuery(id+"F0.wireOp",EDGE,"E10.1.5.4"),sQuery(id+"F0.wireOp",EDGE,"E10.1.5.5"),sQuery(id+"F0.wireOp",EDGE,"E10.1.5.6"),sQuery(id+"F0.wireOp",EDGE,"E10.1.5.7"),sQuery(id+"F0.wireOp",EDGE,"E10.1.6.0"),sQuery(id+"F0.wireOp",EDGE,"E10.1.6.1"),sQuery(id+"F0.wireOp",EDGE,"E10.1.6.2"),sQuery(id+"F0.wireOp",EDGE,"E10.1.6.3"),sQuery(id+"F0.wireOp",EDGE,"E10.1.6.4"),sQuery(id+"F0.wireOp",EDGE,"E10.1.6.5"),sQuery(id+"F0.wireOp",EDGE,"E10.1.6.6"),sQuery(id+"F0.wireOp",EDGE,"E10.1.6.7"),sQuery(id+"F0.wireOp",EDGE,"E10.1.7.0"),sQuery(id+"F0.wireOp",EDGE,"E10.1.7.1"),sQuery(id+"F0.wireOp",EDGE,"E10.1.7.2"),sQuery(id+"F0.wireOp",EDGE,"E10.1.7.3"),sQuery(id+"F0.wireOp",EDGE,"E10.1.7.4"),sQuery(id+"F0.wireOp",EDGE,"E10.1.7.5"),sQuery(id+"F0.wireOp",EDGE,"E10.1.7.6"),sQuery(id+"F0.wireOp",EDGE,"E10.1.7.7"),sQuery(id+"F0.wireOp",EDGE,"E10.2.0.0"),sQuery(id+"F0.wireOp",EDGE,"E10.2.0.1"),sQuery(id+"F0.wireOp",EDGE,"E10.2.0.2"),sQuery(id+"F0.wireOp",EDGE,"E10.2.0.3"),sQuery(id+"F0.wireOp",EDGE,"E10.2.0.4"),sQuery(id+"F0.wireOp",EDGE,"E10.2.0.5"),sQuery(id+"F0.wireOp",EDGE,"E10.2.0.6"),sQuery(id+"F0.wireOp",EDGE,"E10.2.0.7"),sQuery(id+"F0.wireOp",EDGE,"E10.2.1.0"),sQuery(id+"F0.wireOp",EDGE,"E10.2.1.1"),sQuery(id+"F0.wireOp",EDGE,"E10.2.1.2"),sQuery(id+"F0.wireOp",EDGE,"E10.2.1.3"),sQuery(id+"F0.wireOp",EDGE,"E10.2.1.4"),sQuery(id+"F0.wireOp",EDGE,"E10.2.1.5"),sQuery(id+"F0.wireOp",EDGE,"E10.2.1.6"),sQuery(id+"F0.wireOp",EDGE,"E10.2.1.7"),sQuery(id+"F0.wireOp",EDGE,"E10.2.2.0"),sQuery(id+"F0.wireOp",EDGE,"E10.2.2.1"),sQuery(id+"F0.wireOp",EDGE,"E10.2.2.2"),sQuery(id+"F0.wireOp",EDGE,"E10.2.2.3"),sQuery(id+"F0.wireOp",EDGE,"E10.2.2.4"),sQuery(id+"F0.wireOp",EDGE,"E10.2.2.5"),sQuery(id+"F0.wireOp",EDGE,"E10.2.2.6"),sQuery(id+"F0.wireOp",EDGE,"E10.2.2.7"),sQuery(id+"F0.wireOp",EDGE,"E10.2.3.0"),sQuery(id+"F0.wireOp",EDGE,"E10.2.3.1"),sQuery(id+"F0.wireOp",EDGE,"E10.2.3.2"),sQuery(id+"F0.wireOp",EDGE,"E10.2.3.3"),sQuery(id+"F0.wireOp",EDGE,"E10.2.3.4"),sQuery(id+"F0.wireOp",EDGE,"E10.2.3.5"),sQuery(id+"F0.wireOp",EDGE,"E10.2.3.6"),sQuery(id+"F0.wireOp",EDGE,"E10.2.3.7"),sQuery(id+"F0.wireOp",EDGE,"E10.2.4.0"),sQuery(id+"F0.wireOp",EDGE,"E10.2.4.1"),sQuery(id+"F0.wireOp",EDGE,"E10.2.4.2"),sQuery(id+"F0.wireOp",EDGE,"E10.2.4.3"),sQuery(id+"F0.wireOp",EDGE,"E10.2.4.4"),sQuery(id+"F0.wireOp",EDGE,"E10.2.4.5"),sQuery(id+"F0.wireOp",EDGE,"E10.2.4.6"),sQuery(id+"F0.wireOp",EDGE,"E10.2.4.7"),sQuery(id+"F0.wireOp",EDGE,"E10.2.5.0"),sQuery(id+"F0.wireOp",EDGE,"E10.2.5.1"),sQuery(id+"F0.wireOp",EDGE,"E10.2.5.2"),sQuery(id+"F0.wireOp",EDGE,"E10.2.5.3"),sQuery(id+"F0.wireOp",EDGE,"E10.2.5.4"),sQuery(id+"F0.wireOp",EDGE,"E10.2.5.5"),sQuery(id+"F0.wireOp",EDGE,"E10.2.5.6"),sQuery(id+"F0.wireOp",EDGE,"E10.2.5.7"),sQuery(id+"F0.wireOp",EDGE,"E10.2.6.0"),sQuery(id+"F0.wireOp",EDGE,"E10.2.6.1"),sQuery(id+"F0.wireOp",EDGE,"E10.2.6.2"),sQuery(id+"F0.wireOp",EDGE,"E10.2.6.3"),sQuery(id+"F0.wireOp",EDGE,"E10.2.6.4"),sQuery(id+"F0.wireOp",EDGE,"E10.2.6.5"),sQuery(id+"F0.wireOp",EDGE,"E10.2.6.6"),sQuery(id+"F0.wireOp",EDGE,"E10.2.6.7"),sQuery(id+"F0.wireOp",EDGE,"E10.2.7.0"),sQuery(id+"F0.wireOp",EDGE,"E10.2.7.1"),sQuery(id+"F0.wireOp",EDGE,"E10.2.7.2"),sQuery(id+"F0.wireOp",EDGE,"E10.2.7.3"),sQuery(id+"F0.wireOp",EDGE,"E10.2.7.4"),sQuery(id+"F0.wireOp",EDGE,"E10.2.7.5"),sQuery(id+"F0.wireOp",EDGE,"E10.2.7.6"),sQuery(id+"F0.wireOp",EDGE,"E10.2.7.7"),sQuery(id+"F0.wireOp",EDGE,"E10.3.0.0"),sQuery(id+"F0.wireOp",EDGE,"E10.3.0.1"),sQuery(id+"F0.wireOp",EDGE,"E10.3.0.2"),sQuery(id+"F0.wireOp",EDGE,"E10.3.0.3"),sQuery(id+"F0.wireOp",EDGE,"E10.3.0.4"),sQuery(id+"F0.wireOp",EDGE,"E10.3.0.5"),sQuery(id+"F0.wireOp",EDGE,"E10.3.0.6"),sQuery(id+"F0.wireOp",EDGE,"E10.3.0.7"),sQuery(id+"F0.wireOp",EDGE,"E10.3.1.0"),sQuery(id+"F0.wireOp",EDGE,"E10.3.1.1"),sQuery(id+"F0.wireOp",EDGE,"E10.3.1.2"),sQuery(id+"F0.wireOp",EDGE,"E10.3.1.3"),sQuery(id+"F0.wireOp",EDGE,"E10.3.1.4"),sQuery(id+"F0.wireOp",EDGE,"E10.3.1.5"),sQuery(id+"F0.wireOp",EDGE,"E10.3.1.6"),sQuery(id+"F0.wireOp",EDGE,"E10.3.1.7"),sQuery(id+"F0.wireOp",EDGE,"E10.3.2.0"),sQuery(id+"F0.wireOp",EDGE,"E10.3.2.1"),sQuery(id+"F0.wireOp",EDGE,"E10.3.2.2"),sQuery(id+"F0.wireOp",EDGE,"E10.3.2.3"),sQuery(id+"F0.wireOp",EDGE,"E10.3.2.4"),sQuery(id+"F0.wireOp",EDGE,"E10.3.2.5"),sQuery(id+"F0.wireOp",EDGE,"E10.3.2.6"),sQuery(id+"F0.wireOp",EDGE,"E10.3.2.7"),sQuery(id+"F0.wireOp",EDGE,"E10.3.3.0"),sQuery(id+"F0.wireOp",EDGE,"E10.3.3.1"),sQuery(id+"F0.wireOp",EDGE,"E10.3.3.2"),sQuery(id+"F0.wireOp",EDGE,"E10.3.3.3"),sQuery(id+"F0.wireOp",EDGE,"E10.3.3.4"),sQuery(id+"F0.wireOp",EDGE,"E10.3.3.5"),sQuery(id+"F0.wireOp",EDGE,"E10.3.3.6"),sQuery(id+"F0.wireOp",EDGE,"E10.3.3.7"),sQuery(id+"F0.wireOp",EDGE,"E10.3.4.0"),sQuery(id+"F0.wireOp",EDGE,"E10.3.4.1"),sQuery(id+"F0.wireOp",EDGE,"E10.3.4.2"),sQuery(id+"F0.wireOp",EDGE,"E10.3.4.3"),sQuery(id+"F0.wireOp",EDGE,"E10.3.4.4"),sQuery(id+"F0.wireOp",EDGE,"E10.3.4.5"),sQuery(id+"F0.wireOp",EDGE,"E10.3.4.6"),sQuery(id+"F0.wireOp",EDGE,"E10.3.4.7"),sQuery(id+"F0.wireOp",EDGE,"E10.3.5.0"),sQuery(id+"F0.wireOp",EDGE,"E10.3.5.1"),sQuery(id+"F0.wireOp",EDGE,"E10.3.5.2"),sQuery(id+"F0.wireOp",EDGE,"E10.3.5.3"),sQuery(id+"F0.wireOp",EDGE,"E10.3.5.4"),sQuery(id+"F0.wireOp",EDGE,"E10.3.5.5"),sQuery(id+"F0.wireOp",EDGE,"E10.3.5.6"),sQuery(id+"F0.wireOp",EDGE,"E10.3.5.7"),sQuery(id+"F0.wireOp",EDGE,"E10.3.6.0"),sQuery(id+"F0.wireOp",EDGE,"E10.3.6.1"),sQuery(id+"F0.wireOp",EDGE,"E10.3.6.2"),sQuery(id+"F0.wireOp",EDGE,"E10.3.6.3"),sQuery(id+"F0.wireOp",EDGE,"E10.3.6.4"),sQuery(id+"F0.wireOp",EDGE,"E10.3.6.5"),sQuery(id+"F0.wireOp",EDGE,"E10.3.6.6"),sQuery(id+"F0.wireOp",EDGE,"E10.3.6.7"),sQuery(id+"F0.wireOp",EDGE,"E10.3.7.0"),sQuery(id+"F0.wireOp",EDGE,"E10.3.7.1"),sQuery(id+"F0.wireOp",EDGE,"E10.3.7.2"),sQuery(id+"F0.wireOp",EDGE,"E10.3.7.3"),sQuery(id+"F0.wireOp",EDGE,"E10.3.7.4"),sQuery(id+"F0.wireOp",EDGE,"E10.3.7.5"),sQuery(id+"F0.wireOp",EDGE,"E10.3.7.6"),sQuery(id+"F0.wireOp",EDGE,"E10.3.7.7"),sQuery(id+"F0.wireOp",EDGE,"E10.4.0.0"),sQuery(id+"F0.wireOp",EDGE,"E10.4.0.1"),sQuery(id+"F0.wireOp",EDGE,"E10.4.0.2"),sQuery(id+"F0.wireOp",EDGE,"E10.4.0.3"),sQuery(id+"F0.wireOp",EDGE,"E10.4.0.4"),sQuery(id+"F0.wireOp",EDGE,"E10.4.0.5"),sQuery(id+"F0.wireOp",EDGE,"E10.4.0.6"),sQuery(id+"F0.wireOp",EDGE,"E10.4.0.7"),sQuery(id+"F0.wireOp",EDGE,"E10.4.1.0"),sQuery(id+"F0.wireOp",EDGE,"E10.4.1.1"),sQuery(id+"F0.wireOp",EDGE,"E10.4.1.2"),sQuery(id+"F0.wireOp",EDGE,"E10.4.1.3"),sQuery(id+"F0.wireOp",EDGE,"E10.4.1.4"),sQuery(id+"F0.wireOp",EDGE,"E10.4.1.5"),sQuery(id+"F0.wireOp",EDGE,"E10.4.1.6"),sQuery(id+"F0.wireOp",EDGE,"E10.4.1.7"),sQuery(id+"F0.wireOp",EDGE,"E10.4.2.0"),sQuery(id+"F0.wireOp",EDGE,"E10.4.2.1"),sQuery(id+"F0.wireOp",EDGE,"E10.4.2.2"),sQuery(id+"F0.wireOp",EDGE,"E10.4.2.3"),sQuery(id+"F0.wireOp",EDGE,"E10.4.2.4"),sQuery(id+"F0.wireOp",EDGE,"E10.4.2.5"),sQuery(id+"F0.wireOp",EDGE,"E10.4.2.6"),sQuery(id+"F0.wireOp",EDGE,"E10.4.2.7"),sQuery(id+"F0.wireOp",EDGE,"E10.4.3.0"),sQuery(id+"F0.wireOp",EDGE,"E10.4.3.1"),sQuery(id+"F0.wireOp",EDGE,"E10.4.3.2"),sQuery(id+"F0.wireOp",EDGE,"E10.4.3.3"),sQuery(id+"F0.wireOp",EDGE,"E10.4.3.4"),sQuery(id+"F0.wireOp",EDGE,"E10.4.3.5"),sQuery(id+"F0.wireOp",EDGE,"E10.4.3.6"),sQuery(id+"F0.wireOp",EDGE,"E10.4.3.7"),sQuery(id+"F0.wireOp",EDGE,"E10.4.4.0"),sQuery(id+"F0.wireOp",EDGE,"E10.4.4.1"),sQuery(id+"F0.wireOp",EDGE,"E10.4.4.2"),sQuery(id+"F0.wireOp",EDGE,"E10.4.4.3"),sQuery(id+"F0.wireOp",EDGE,"E10.4.4.4"),sQuery(id+"F0.wireOp",EDGE,"E10.4.4.5"),sQuery(id+"F0.wireOp",EDGE,"E10.4.4.6"),sQuery(id+"F0.wireOp",EDGE,"E10.4.4.7"),sQuery(id+"F0.wireOp",EDGE,"E10.4.5.0"),sQuery(id+"F0.wireOp",EDGE,"E10.4.5.1"),sQuery(id+"F0.wireOp",EDGE,"E10.4.5.2"),sQuery(id+"F0.wireOp",EDGE,"E10.4.5.3"),sQuery(id+"F0.wireOp",EDGE,"E10.4.5.4"),sQuery(id+"F0.wireOp",EDGE,"E10.4.5.5"),sQuery(id+"F0.wireOp",EDGE,"E10.4.5.6"),sQuery(id+"F0.wireOp",EDGE,"E10.4.5.7"),sQuery(id+"F0.wireOp",EDGE,"E10.4.6.0"),sQuery(id+"F0.wireOp",EDGE,"E10.4.6.1"),sQuery(id+"F0.wireOp",EDGE,"E10.4.6.2"),sQuery(id+"F0.wireOp",EDGE,"E10.4.6.3"),sQuery(id+"F0.wireOp",EDGE,"E10.4.6.4"),sQuery(id+"F0.wireOp",EDGE,"E10.4.6.5"),sQuery(id+"F0.wireOp",EDGE,"E10.4.6.6"),sQuery(id+"F0.wireOp",EDGE,"E10.4.6.7"),sQuery(id+"F0.wireOp",EDGE,"E10.4.7.0"),sQuery(id+"F0.wireOp",EDGE,"E10.4.7.1"),sQuery(id+"F0.wireOp",EDGE,"E10.4.7.2"),sQuery(id+"F0.wireOp",EDGE,"E10.4.7.3"),sQuery(id+"F0.wireOp",EDGE,"E10.4.7.4"),sQuery(id+"F0.wireOp",EDGE,"E10.4.7.5"),sQuery(id+"F0.wireOp",EDGE,"E10.4.7.6"),sQuery(id+"F0.wireOp",EDGE,"E10.4.7.7"),sQuery(id+"F0.wireOp",EDGE,"E10.5.0.0"),sQuery(id+"F0.wireOp",EDGE,"E10.5.0.1"),sQuery(id+"F0.wireOp",EDGE,"E10.5.0.2"),sQuery(id+"F0.wireOp",EDGE,"E10.5.0.3"),sQuery(id+"F0.wireOp",EDGE,"E10.5.0.4"),sQuery(id+"F0.wireOp",EDGE,"E10.5.0.5"),sQuery(id+"F0.wireOp",EDGE,"E10.5.0.6"),sQuery(id+"F0.wireOp",EDGE,"E10.5.0.7"),sQuery(id+"F0.wireOp",EDGE,"E10.5.1.0"),sQuery(id+"F0.wireOp",EDGE,"E10.5.1.1"),sQuery(id+"F0.wireOp",EDGE,"E10.5.1.2"),sQuery(id+"F0.wireOp",EDGE,"E10.5.1.3"),sQuery(id+"F0.wireOp",EDGE,"E10.5.1.4"),sQuery(id+"F0.wireOp",EDGE,"E10.5.1.5"),sQuery(id+"F0.wireOp",EDGE,"E10.5.1.6"),sQuery(id+"F0.wireOp",EDGE,"E10.5.1.7"),sQuery(id+"F0.wireOp",EDGE,"E10.5.2.0"),sQuery(id+"F0.wireOp",EDGE,"E10.5.2.1"),sQuery(id+"F0.wireOp",EDGE,"E10.5.2.2"),sQuery(id+"F0.wireOp",EDGE,"E10.5.2.3"),sQuery(id+"F0.wireOp",EDGE,"E10.5.2.4"),sQuery(id+"F0.wireOp",EDGE,"E10.5.2.5"),sQuery(id+"F0.wireOp",EDGE,"E10.5.2.6"),sQuery(id+"F0.wireOp",EDGE,"E10.5.2.7"),sQuery(id+"F0.wireOp",EDGE,"E10.5.3.0"),sQuery(id+"F0.wireOp",EDGE,"E10.5.3.1"),sQuery(id+"F0.wireOp",EDGE,"E10.5.3.2"),sQuery(id+"F0.wireOp",EDGE,"E10.5.3.3"),sQuery(id+"F0.wireOp",EDGE,"E10.5.3.4"),sQuery(id+"F0.wireOp",EDGE,"E10.5.3.5"),sQuery(id+"F0.wireOp",EDGE,"E10.5.3.6"),sQuery(id+"F0.wireOp",EDGE,"E10.5.3.7"),sQuery(id+"F0.wireOp",EDGE,"E10.5.4.0"),sQuery(id+"F0.wireOp",EDGE,"E10.5.4.1"),sQuery(id+"F0.wireOp",EDGE,"E10.5.4.2"),sQuery(id+"F0.wireOp",EDGE,"E10.5.4.3"),sQuery(id+"F0.wireOp",EDGE,"E10.5.4.4"),sQuery(id+"F0.wireOp",EDGE,"E10.5.4.5"),sQuery(id+"F0.wireOp",EDGE,"E10.5.4.6"),sQuery(id+"F0.wireOp",EDGE,"E10.5.4.7"),sQuery(id+"F0.wireOp",EDGE,"E10.5.5.0"),sQuery(id+"F0.wireOp",EDGE,"E10.5.5.1"),sQuery(id+"F0.wireOp",EDGE,"E10.5.5.2"),sQuery(id+"F0.wireOp",EDGE,"E10.5.5.3"),sQuery(id+"F0.wireOp",EDGE,"E10.5.5.4"),sQuery(id+"F0.wireOp",EDGE,"E10.5.5.5"),sQuery(id+"F0.wireOp",EDGE,"E10.5.5.6"),sQuery(id+"F0.wireOp",EDGE,"E10.5.5.7"),sQuery(id+"F0.wireOp",EDGE,"E10.5.6.0"),sQuery(id+"F0.wireOp",EDGE,"E10.5.6.1"),sQuery(id+"F0.wireOp",EDGE,"E10.5.6.2"),sQuery(id+"F0.wireOp",EDGE,"E10.5.6.3"),sQuery(id+"F0.wireOp",EDGE,"E10.5.6.4"),sQuery(id+"F0.wireOp",EDGE,"E10.5.6.5"),sQuery(id+"F0.wireOp",EDGE,"E10.5.6.6"),sQuery(id+"F0.wireOp",EDGE,"E10.5.6.7"),sQuery(id+"F0.wireOp",EDGE,"E10.5.7.0"),sQuery(id+"F0.wireOp",EDGE,"E10.5.7.1"),sQuery(id+"F0.wireOp",EDGE,"E10.5.7.2"),sQuery(id+"F0.wireOp",EDGE,"E10.5.7.3"),sQuery(id+"F0.wireOp",EDGE,"E10.5.7.4"),sQuery(id+"F0.wireOp",EDGE,"E10.5.7.5"),sQuery(id+"F0.wireOp",EDGE,"E10.5.7.6"),sQuery(id+"F0.wireOp",EDGE,"E10.5.7.7"),sQuery(id+"F0.wireOp",EDGE,"E10.6.0.0"),sQuery(id+"F0.wireOp",EDGE,"E10.6.0.1"),sQuery(id+"F0.wireOp",EDGE,"E10.6.0.2"),sQuery(id+"F0.wireOp",EDGE,"E10.6.0.3"),sQuery(id+"F0.wireOp",EDGE,"E10.6.0.4"),sQuery(id+"F0.wireOp",EDGE,"E10.6.0.5"),sQuery(id+"F0.wireOp",EDGE,"E10.6.0.6"),sQuery(id+"F0.wireOp",EDGE,"E10.6.0.7"),sQuery(id+"F0.wireOp",EDGE,"E10.6.1.0"),sQuery(id+"F0.wireOp",EDGE,"E10.6.1.1"),sQuery(id+"F0.wireOp",EDGE,"E10.6.1.2"),sQuery(id+"F0.wireOp",EDGE,"E10.6.1.3"),sQuery(id+"F0.wireOp",EDGE,"E10.6.1.4"),sQuery(id+"F0.wireOp",EDGE,"E10.6.1.5"),sQuery(id+"F0.wireOp",EDGE,"E10.6.1.6"),sQuery(id+"F0.wireOp",EDGE,"E10.6.1.7"),sQuery(id+"F0.wireOp",EDGE,"E10.6.2.0"),sQuery(id+"F0.wireOp",EDGE,"E10.6.2.1"),sQuery(id+"F0.wireOp",EDGE,"E10.6.2.2"),sQuery(id+"F0.wireOp",EDGE,"E10.6.2.3"),sQuery(id+"F0.wireOp",EDGE,"E10.6.2.4"),sQuery(id+"F0.wireOp",EDGE,"E10.6.2.5"),sQuery(id+"F0.wireOp",EDGE,"E10.6.2.6"),sQuery(id+"F0.wireOp",EDGE,"E10.6.2.7"),sQuery(id+"F0.wireOp",EDGE,"E10.6.3.0"),sQuery(id+"F0.wireOp",EDGE,"E10.6.3.1"),sQuery(id+"F0.wireOp",EDGE,"E10.6.3.2"),sQuery(id+"F0.wireOp",EDGE,"E10.6.3.3"),sQuery(id+"F0.wireOp",EDGE,"E10.6.3.4"),sQuery(id+"F0.wireOp",EDGE,"E10.6.3.5"),sQuery(id+"F0.wireOp",EDGE,"E10.6.3.6"),sQuery(id+"F0.wireOp",EDGE,"E10.6.3.7"),sQuery(id+"F0.wireOp",EDGE,"E10.6.4.0"),sQuery(id+"F0.wireOp",EDGE,"E10.6.4.1"),sQuery(id+"F0.wireOp",EDGE,"E10.6.4.2"),sQuery(id+"F0.wireOp",EDGE,"E10.6.4.3"),sQuery(id+"F0.wireOp",EDGE,"E10.6.4.4"),sQuery(id+"F0.wireOp",EDGE,"E10.6.4.5"),sQuery(id+"F0.wireOp",EDGE,"E10.6.4.6"),sQuery(id+"F0.wireOp",EDGE,"E10.6.4.7"),sQuery(id+"F0.wireOp",EDGE,"E10.6.5.0"),sQuery(id+"F0.wireOp",EDGE,"E10.6.5.1"),sQuery(id+"F0.wireOp",EDGE,"E10.6.5.2"),sQuery(id+"F0.wireOp",EDGE,"E10.6.5.3"),sQuery(id+"F0.wireOp",EDGE,"E10.6.5.4"),sQuery(id+"F0.wireOp",EDGE,"E10.6.5.5"),sQuery(id+"F0.wireOp",EDGE,"E10.6.5.6"),sQuery(id+"F0.wireOp",EDGE,"E10.6.5.7"),sQuery(id+"F0.wireOp",EDGE,"E10.6.6.0"),sQuery(id+"F0.wireOp",EDGE,"E10.6.6.1"),sQuery(id+"F0.wireOp",EDGE,"E10.6.6.2"),sQuery(id+"F0.wireOp",EDGE,"E10.6.6.3"),sQuery(id+"F0.wireOp",EDGE,"E10.6.6.4"),sQuery(id+"F0.wireOp",EDGE,"E10.6.6.5"),sQuery(id+"F0.wireOp",EDGE,"E10.6.6.6"),sQuery(id+"F0.wireOp",EDGE,"E10.6.6.7"),sQuery(id+"F0.wireOp",EDGE,"E10.6.7.0"),sQuery(id+"F0.wireOp",EDGE,"E10.6.7.1"),sQuery(id+"F0.wireOp",EDGE,"E10.6.7.2"),sQuery(id+"F0.wireOp",EDGE,"E10.6.7.3"),sQuery(id+"F0.wireOp",EDGE,"E10.6.7.4"),sQuery(id+"F0.wireOp",EDGE,"E10.6.7.5"),sQuery(id+"F0.wireOp",EDGE,"E10.6.7.6"),sQuery(id+"F0.wireOp",EDGE,"E10.6.7.7"),sQuery(id+"F0.wireOp",EDGE,"E10.7.0.0"),sQuery(id+"F0.wireOp",EDGE,"E10.7.0.1"),sQuery(id+"F0.wireOp",EDGE,"E10.7.0.2"),sQuery(id+"F0.wireOp",EDGE,"E10.7.0.3"),sQuery(id+"F0.wireOp",EDGE,"E10.7.0.4"),sQuery(id+"F0.wireOp",EDGE,"E10.7.0.5"),sQuery(id+"F0.wireOp",EDGE,"E10.7.0.6"),sQuery(id+"F0.wireOp",EDGE,"E10.7.0.7"),sQuery(id+"F0.wireOp",EDGE,"E10.7.1.0"),sQuery(id+"F0.wireOp",EDGE,"E10.7.1.1"),sQuery(id+"F0.wireOp",EDGE,"E10.7.1.2"),sQuery(id+"F0.wireOp",EDGE,"E10.7.1.3"),sQuery(id+"F0.wireOp",EDGE,"E10.7.1.4"),sQuery(id+"F0.wireOp",EDGE,"E10.7.1.5"),sQuery(id+"F0.wireOp",EDGE,"E10.7.1.6"),sQuery(id+"F0.wireOp",EDGE,"E10.7.1.7"),sQuery(id+"F0.wireOp",EDGE,"E10.7.2.0"),sQuery(id+"F0.wireOp",EDGE,"E10.7.2.1"),sQuery(id+"F0.wireOp",EDGE,"E10.7.2.2"),sQuery(id+"F0.wireOp",EDGE,"E10.7.2.3"),sQuery(id+"F0.wireOp",EDGE,"E10.7.2.4"),sQuery(id+"F0.wireOp",EDGE,"E10.7.2.5"),sQuery(id+"F0.wireOp",EDGE,"E10.7.2.6"),sQuery(id+"F0.wireOp",EDGE,"E10.7.2.7"),sQuery(id+"F0.wireOp",EDGE,"E10.7.3.0"),sQuery(id+"F0.wireOp",EDGE,"E10.7.3.1"),sQuery(id+"F0.wireOp",EDGE,"E10.7.3.2"),sQuery(id+"F0.wireOp",EDGE,"E10.7.3.3"),sQuery(id+"F0.wireOp",EDGE,"E10.7.3.4"),sQuery(id+"F0.wireOp",EDGE,"E10.7.3.5"),sQuery(id+"F0.wireOp",EDGE,"E10.7.3.6"),sQuery(id+"F0.wireOp",EDGE,"E10.7.3.7"),sQuery(id+"F0.wireOp",EDGE,"E10.7.4.0"),sQuery(id+"F0.wireOp",EDGE,"E10.7.4.1"),sQuery(id+"F0.wireOp",EDGE,"E10.7.4.2"),sQuery(id+"F0.wireOp",EDGE,"E10.7.4.3"),sQuery(id+"F0.wireOp",EDGE,"E10.7.4.4"),sQuery(id+"F0.wireOp",EDGE,"E10.7.4.5"),sQuery(id+"F0.wireOp",EDGE,"E10.7.4.6"),sQuery(id+"F0.wireOp",EDGE,"E10.7.4.7"),sQuery(id+"F0.wireOp",EDGE,"E10.7.5.0"),sQuery(id+"F0.wireOp",EDGE,"E10.7.5.1"),sQuery(id+"F0.wireOp",EDGE,"E10.7.5.2"),sQuery(id+"F0.wireOp",EDGE,"E10.7.5.3"),sQuery(id+"F0.wireOp",EDGE,"E10.7.5.4"),sQuery(id+"F0.wireOp",EDGE,"E10.7.5.5"),sQuery(id+"F0.wireOp",EDGE,"E10.7.5.6"),sQuery(id+"F0.wireOp",EDGE,"E10.7.5.7"),sQuery(id+"F0.wireOp",EDGE,"E10.7.6.0"),sQuery(id+"F0.wireOp",EDGE,"E10.7.6.1"),sQuery(id+"F0.wireOp",EDGE,"E10.7.6.2"),sQuery(id+"F0.wireOp",EDGE,"E10.7.6.3"),sQuery(id+"F0.wireOp",EDGE,"E10.7.6.4"),sQuery(id+"F0.wireOp",EDGE,"E10.7.6.5"),sQuery(id+"F0.wireOp",EDGE,"E10.7.6.6"),sQuery(id+"F0.wireOp",EDGE,"E10.7.6.7"),sQuery(id+"F0.wireOp",EDGE,"E10.7.7.0"),sQuery(id+"F0.wireOp",EDGE,"E10.7.7.1"),sQuery(id+"F0.wireOp",EDGE,"E10.7.7.2"),sQuery(id+"F0.wireOp",EDGE,"E10.7.7.3"),sQuery(id+"F0.wireOp",EDGE,"E10.7.7.4"),sQuery(id+"F0.wireOp",EDGE,"E10.7.7.5"),sQuery(id+"F0.wireOp",EDGE,"E10.7.7.6"),sQuery(id+"F0.wireOp",EDGE,"E10.7.7.7")])],"isStart":true});
            var sketch = newSketch(context, id + "F3", { "sketchPlane" : qUnion([Q0])});
            skLineSegment(sketch, "E11.0", {"start": v(82.55, -85.1) * mm, "end": v(-82.55, -85.1) * mm});
            skArc(sketch, "E12.0", {"start": v(85.1, -82.55) * mm, "mid": v(84.35, -84.35) * mm, "end": v(82.55, -85.09) * mm});
            skLineSegment(sketch, "E13.0", {"start": v(85.1, -82.55) * mm, "end": v(85.09, 82.55) * mm});
            skLineSegment(sketch, "E14.0.0", {"start": v(82.55, 85.1) * mm, "end": v(-82.55, 85.1) * mm});
            skArc(sketch, "E14.0.1", {"start": v(-82.55, 85.1) * mm, "mid": v(-84.35, 84.35) * mm, "end": v(-85.1, 82.55) * mm});
            skLineSegment(sketch, "E14.0.2", {"start": v(-85.1, 82.55) * mm, "end": v(-85.1, -82.55) * mm});
            skArc(sketch, "E14.0.3", {"start": v(-85.1, -82.55) * mm, "mid": v(-84.35, -84.35) * mm, "end": v(-82.55, -85.1) * mm});
            skLineSegment(sketch, "E14.0.4", {"start": v(-82.55, -85.1) * mm, "end": v(82.55, -85.1) * mm});
            skArc(sketch, "E14.0.5", {"start": v(82.55, -85.09) * mm, "mid": v(84.35, -84.35) * mm, "end": v(85.1, -82.55) * mm});
            skArc(sketch, "E14.0.7", {"start": v(85.09, 82.55) * mm, "mid": v(84.35, 84.35) * mm, "end": v(82.55, 85.1) * mm});
            skLineSegment(sketch, "E15.bottom", {"start": v(82.55, 82.55) * mm, "end": v(-82.55, 82.55) * mm});
            skLineSegment(sketch, "E15.top", {"start": v(82.55, -82.55) * mm, "end": v(-82.55, -82.55) * mm});
            skLineSegment(sketch, "E15.left", {"start": v(82.55, 82.55) * mm, "end": v(82.55, -82.55) * mm});
            skLineSegment(sketch, "E15.right", {"start": v(-82.55, 82.55) * mm, "end": v(-82.55, -82.55) * mm});
            skPoint(sketch, "E15.middle", {"position": v(0, 0) * mm});
            skSolve(sketch);
        }
        {
            var Q0;
            Q0 = qSketchRegion(id + "F3", true);
            extrude(context, id + "F4", {"entities" : qUnion([Q0]), "operationType" : NewBodyOperationType.ADD, "depth" : 38.1 * mm, "offsetDistance" : 25.4 * mm});
        }
        {
            var Q0;
            Q0=makeQuery(id+"F4.opExtrude","CAP_EDGE",EDGE,{"disambiguationData":[OSD([sQuery(id+"F3.wireOp",EDGE,"E14.0.2")])],"isStart":false});
            fillet(context, id + "F5", {"entities" : qUnion([Q0]), "radius" : 0.25 * mm, "tangentPropagation" : true, "allowEdgeOverflow" : false});
        }
        {
            var Q0;
            Q0=makeQuery(id+"F1.opExtrude","CAP_FACE",FACE,{"disambiguationData":[OSD([sQuery(id+"F0.wireOp",EDGE,"E0.bottom"),sQuery(id+"F0.wireOp",EDGE,"E0.top"),sQuery(id+"F0.wireOp",EDGE,"E0.left"),sQuery(id+"F0.wireOp",EDGE,"E0.right"),sQuery(id+"F0.wireOp",EDGE,"E1.filletArc"),sQuery(id+"F0.wireOp",EDGE,"E2.filletArc"),sQuery(id+"F0.wireOp",EDGE,"E3.filletArc"),sQuery(id+"F0.wireOp",EDGE,"E4.filletArc"),sQuery(id+"F0.wireOp",EDGE,"E5.bottom"),sQuery(id+"F0.wireOp",EDGE,"E5.top"),sQuery(id+"F0.wireOp",EDGE,"E5.left"),sQuery(id+"F0.wireOp",EDGE,"E5.right"),sQuery(id+"F0.wireOp",EDGE,"E6.filletArc"),sQuery(id+"F0.wireOp",EDGE,"E7.filletArc"),sQuery(id+"F0.wireOp",EDGE,"E8.filletArc"),sQuery(id+"F0.wireOp",EDGE,"E9.filletArc"),sQuery(id+"F0.wireOp",EDGE,"E10.0.1.0"),sQuery(id+"F0.wireOp",EDGE,"E10.0.1.1"),sQuery(id+"F0.wireOp",EDGE,"E10.0.1.2"),sQuery(id+"F0.wireOp",EDGE,"E10.0.1.3"),sQuery(id+"F0.wireOp",EDGE,"E10.0.1.4"),sQuery(id+"F0.wireOp",EDGE,"E10.0.1.5"),sQuery(id+"F0.wireOp",EDGE,"E10.0.1.6"),sQuery(id+"F0.wireOp",EDGE,"E10.0.1.7"),sQuery(id+"F0.wireOp",EDGE,"E10.0.2.0"),sQuery(id+"F0.wireOp",EDGE,"E10.0.2.1"),sQuery(id+"F0.wireOp",EDGE,"E10.0.2.2"),sQuery(id+"F0.wireOp",EDGE,"E10.0.2.3"),sQuery(id+"F0.wireOp",EDGE,"E10.0.2.4"),sQuery(id+"F0.wireOp",EDGE,"E10.0.2.5"),sQuery(id+"F0.wireOp",EDGE,"E10.0.2.6"),sQuery(id+"F0.wireOp",EDGE,"E10.0.2.7"),sQuery(id+"F0.wireOp",EDGE,"E10.0.3.0"),sQuery(id+"F0.wireOp",EDGE,"E10.0.3.1"),sQuery(id+"F0.wireOp",EDGE,"E10.0.3.2"),sQuery(id+"F0.wireOp",EDGE,"E10.0.3.3"),sQuery(id+"F0.wireOp",EDGE,"E10.0.3.4"),sQuery(id+"F0.wireOp",EDGE,"E10.0.3.5"),sQuery(id+"F0.wireOp",EDGE,"E10.0.3.6"),sQuery(id+"F0.wireOp",EDGE,"E10.0.3.7"),sQuery(id+"F0.wireOp",EDGE,"E10.0.4.0"),sQuery(id+"F0.wireOp",EDGE,"E10.0.4.1"),sQuery(id+"F0.wireOp",EDGE,"E10.0.4.2"),sQuery(id+"F0.wireOp",EDGE,"E10.0.4.3"),sQuery(id+"F0.wireOp",EDGE,"E10.0.4.4"),sQuery(id+"F0.wireOp",EDGE,"E10.0.4.5"),sQuery(id+"F0.wireOp",EDGE,"E10.0.4.6"),sQuery(id+"F0.wireOp",EDGE,"E10.0.4.7"),sQuery(id+"F0.wireOp",EDGE,"E10.0.5.0"),sQuery(id+"F0.wireOp",EDGE,"E10.0.5.1"),sQuery(id+"F0.wireOp",EDGE,"E10.0.5.2"),sQuery(id+"F0.wireOp",EDGE,"E10.0.5.3"),sQuery(id+"F0.wireOp",EDGE,"E10.0.5.4"),sQuery(id+"F0.wireOp",EDGE,"E10.0.5.5"),sQuery(id+"F0.wireOp",EDGE,"E10.0.5.6"),sQuery(id+"F0.wireOp",EDGE,"E10.0.5.7"),sQuery(id+"F0.wireOp",EDGE,"E10.0.6.0"),sQuery(id+"F0.wireOp",EDGE,"E10.0.6.1"),sQuery(id+"F0.wireOp",EDGE,"E10.0.6.2"),sQuery(id+"F0.wireOp",EDGE,"E10.0.6.3"),sQuery(id+"F0.wireOp",EDGE,"E10.0.6.4"),sQuery(id+"F0.wireOp",EDGE,"E10.0.6.5"),sQuery(id+"F0.wireOp",EDGE,"E10.0.6.6"),sQuery(id+"F0.wireOp",EDGE,"E10.0.6.7"),sQuery(id+"F0.wireOp",EDGE,"E10.0.7.0"),sQuery(id+"F0.wireOp",EDGE,"E10.0.7.1"),sQuery(id+"F0.wireOp",EDGE,"E10.0.7.2"),sQuery(id+"F0.wireOp",EDGE,"E10.0.7.3"),sQuery(id+"F0.wireOp",EDGE,"E10.0.7.4"),sQuery(id+"F0.wireOp",EDGE,"E10.0.7.5"),sQuery(id+"F0.wireOp",EDGE,"E10.0.7.6"),sQuery(id+"F0.wireOp",EDGE,"E10.0.7.7"),sQuery(id+"F0.wireOp",EDGE,"E10.1.0.0"),sQuery(id+"F0.wireOp",EDGE,"E10.1.0.1"),sQuery(id+"F0.wireOp",EDGE,"E10.1.0.2"),sQuery(id+"F0.wireOp",EDGE,"E10.1.0.3"),sQuery(id+"F0.wireOp",EDGE,"E10.1.0.4"),sQuery(id+"F0.wireOp",EDGE,"E10.1.0.5"),sQuery(id+"F0.wireOp",EDGE,"E10.1.0.6"),sQuery(id+"F0.wireOp",EDGE,"E10.1.0.7"),sQuery(id+"F0.wireOp",EDGE,"E10.1.1.0"),sQuery(id+"F0.wireOp",EDGE,"E10.1.1.1"),sQuery(id+"F0.wireOp",EDGE,"E10.1.1.2"),sQuery(id+"F0.wireOp",EDGE,"E10.1.1.3"),sQuery(id+"F0.wireOp",EDGE,"E10.1.1.4"),sQuery(id+"F0.wireOp",EDGE,"E10.1.1.5"),sQuery(id+"F0.wireOp",EDGE,"E10.1.1.6"),sQuery(id+"F0.wireOp",EDGE,"E10.1.1.7"),sQuery(id+"F0.wireOp",EDGE,"E10.1.2.0"),sQuery(id+"F0.wireOp",EDGE,"E10.1.2.1"),sQuery(id+"F0.wireOp",EDGE,"E10.1.2.2"),sQuery(id+"F0.wireOp",EDGE,"E10.1.2.3"),sQuery(id+"F0.wireOp",EDGE,"E10.1.2.4"),sQuery(id+"F0.wireOp",EDGE,"E10.1.2.5"),sQuery(id+"F0.wireOp",EDGE,"E10.1.2.6"),sQuery(id+"F0.wireOp",EDGE,"E10.1.2.7"),sQuery(id+"F0.wireOp",EDGE,"E10.1.3.0"),sQuery(id+"F0.wireOp",EDGE,"E10.1.3.1"),sQuery(id+"F0.wireOp",EDGE,"E10.1.3.2"),sQuery(id+"F0.wireOp",EDGE,"E10.1.3.3"),sQuery(id+"F0.wireOp",EDGE,"E10.1.3.4"),sQuery(id+"F0.wireOp",EDGE,"E10.1.3.5"),sQuery(id+"F0.wireOp",EDGE,"E10.1.3.6"),sQuery(id+"F0.wireOp",EDGE,"E10.1.3.7"),sQuery(id+"F0.wireOp",EDGE,"E10.1.4.0"),sQuery(id+"F0.wireOp",EDGE,"E10.1.4.1"),sQuery(id+"F0.wireOp",EDGE,"E10.1.4.2"),sQuery(id+"F0.wireOp",EDGE,"E10.1.4.3"),sQuery(id+"F0.wireOp",EDGE,"E10.1.4.4"),sQuery(id+"F0.wireOp",EDGE,"E10.1.4.5"),sQuery(id+"F0.wireOp",EDGE,"E10.1.4.6"),sQuery(id+"F0.wireOp",EDGE,"E10.1.4.7"),sQuery(id+"F0.wireOp",EDGE,"E10.1.5.0"),sQuery(id+"F0.wireOp",EDGE,"E10.1.5.1"),sQuery(id+"F0.wireOp",EDGE,"E10.1.5.2"),sQuery(id+"F0.wireOp",EDGE,"E10.1.5.3"),sQuery(id+"F0.wireOp",EDGE,"E10.1.5.4"),sQuery(id+"F0.wireOp",EDGE,"E10.1.5.5"),sQuery(id+"F0.wireOp",EDGE,"E10.1.5.6"),sQuery(id+"F0.wireOp",EDGE,"E10.1.5.7"),sQuery(id+"F0.wireOp",EDGE,"E10.1.6.0"),sQuery(id+"F0.wireOp",EDGE,"E10.1.6.1"),sQuery(id+"F0.wireOp",EDGE,"E10.1.6.2"),sQuery(id+"F0.wireOp",EDGE,"E10.1.6.3"),sQuery(id+"F0.wireOp",EDGE,"E10.1.6.4"),sQuery(id+"F0.wireOp",EDGE,"E10.1.6.5"),sQuery(id+"F0.wireOp",EDGE,"E10.1.6.6"),sQuery(id+"F0.wireOp",EDGE,"E10.1.6.7"),sQuery(id+"F0.wireOp",EDGE,"E10.1.7.0"),sQuery(id+"F0.wireOp",EDGE,"E10.1.7.1"),sQuery(id+"F0.wireOp",EDGE,"E10.1.7.2"),sQuery(id+"F0.wireOp",EDGE,"E10.1.7.3"),sQuery(id+"F0.wireOp",EDGE,"E10.1.7.4"),sQuery(id+"F0.wireOp",EDGE,"E10.1.7.5"),sQuery(id+"F0.wireOp",EDGE,"E10.1.7.6"),sQuery(id+"F0.wireOp",EDGE,"E10.1.7.7"),sQuery(id+"F0.wireOp",EDGE,"E10.2.0.0"),sQuery(id+"F0.wireOp",EDGE,"E10.2.0.1"),sQuery(id+"F0.wireOp",EDGE,"E10.2.0.2"),sQuery(id+"F0.wireOp",EDGE,"E10.2.0.3"),sQuery(id+"F0.wireOp",EDGE,"E10.2.0.4"),sQuery(id+"F0.wireOp",EDGE,"E10.2.0.5"),sQuery(id+"F0.wireOp",EDGE,"E10.2.0.6"),sQuery(id+"F0.wireOp",EDGE,"E10.2.0.7"),sQuery(id+"F0.wireOp",EDGE,"E10.2.1.0"),sQuery(id+"F0.wireOp",EDGE,"E10.2.1.1"),sQuery(id+"F0.wireOp",EDGE,"E10.2.1.2"),sQuery(id+"F0.wireOp",EDGE,"E10.2.1.3"),sQuery(id+"F0.wireOp",EDGE,"E10.2.1.4"),sQuery(id+"F0.wireOp",EDGE,"E10.2.1.5"),sQuery(id+"F0.wireOp",EDGE,"E10.2.1.6"),sQuery(id+"F0.wireOp",EDGE,"E10.2.1.7"),sQuery(id+"F0.wireOp",EDGE,"E10.2.2.0"),sQuery(id+"F0.wireOp",EDGE,"E10.2.2.1"),sQuery(id+"F0.wireOp",EDGE,"E10.2.2.2"),sQuery(id+"F0.wireOp",EDGE,"E10.2.2.3"),sQuery(id+"F0.wireOp",EDGE,"E10.2.2.4"),sQuery(id+"F0.wireOp",EDGE,"E10.2.2.5"),sQuery(id+"F0.wireOp",EDGE,"E10.2.2.6"),sQuery(id+"F0.wireOp",EDGE,"E10.2.2.7"),sQuery(id+"F0.wireOp",EDGE,"E10.2.3.0"),sQuery(id+"F0.wireOp",EDGE,"E10.2.3.1"),sQuery(id+"F0.wireOp",EDGE,"E10.2.3.2"),sQuery(id+"F0.wireOp",EDGE,"E10.2.3.3"),sQuery(id+"F0.wireOp",EDGE,"E10.2.3.4"),sQuery(id+"F0.wireOp",EDGE,"E10.2.3.5"),sQuery(id+"F0.wireOp",EDGE,"E10.2.3.6"),sQuery(id+"F0.wireOp",EDGE,"E10.2.3.7"),sQuery(id+"F0.wireOp",EDGE,"E10.2.4.0"),sQuery(id+"F0.wireOp",EDGE,"E10.2.4.1"),sQuery(id+"F0.wireOp",EDGE,"E10.2.4.2"),sQuery(id+"F0.wireOp",EDGE,"E10.2.4.3"),sQuery(id+"F0.wireOp",EDGE,"E10.2.4.4"),sQuery(id+"F0.wireOp",EDGE,"E10.2.4.5"),sQuery(id+"F0.wireOp",EDGE,"E10.2.4.6"),sQuery(id+"F0.wireOp",EDGE,"E10.2.4.7"),sQuery(id+"F0.wireOp",EDGE,"E10.2.5.0"),sQuery(id+"F0.wireOp",EDGE,"E10.2.5.1"),sQuery(id+"F0.wireOp",EDGE,"E10.2.5.2"),sQuery(id+"F0.wireOp",EDGE,"E10.2.5.3"),sQuery(id+"F0.wireOp",EDGE,"E10.2.5.4"),sQuery(id+"F0.wireOp",EDGE,"E10.2.5.5"),sQuery(id+"F0.wireOp",EDGE,"E10.2.5.6"),sQuery(id+"F0.wireOp",EDGE,"E10.2.5.7"),sQuery(id+"F0.wireOp",EDGE,"E10.2.6.0"),sQuery(id+"F0.wireOp",EDGE,"E10.2.6.1"),sQuery(id+"F0.wireOp",EDGE,"E10.2.6.2"),sQuery(id+"F0.wireOp",EDGE,"E10.2.6.3"),sQuery(id+"F0.wireOp",EDGE,"E10.2.6.4"),sQuery(id+"F0.wireOp",EDGE,"E10.2.6.5"),sQuery(id+"F0.wireOp",EDGE,"E10.2.6.6"),sQuery(id+"F0.wireOp",EDGE,"E10.2.6.7"),sQuery(id+"F0.wireOp",EDGE,"E10.2.7.0"),sQuery(id+"F0.wireOp",EDGE,"E10.2.7.1"),sQuery(id+"F0.wireOp",EDGE,"E10.2.7.2"),sQuery(id+"F0.wireOp",EDGE,"E10.2.7.3"),sQuery(id+"F0.wireOp",EDGE,"E10.2.7.4"),sQuery(id+"F0.wireOp",EDGE,"E10.2.7.5"),sQuery(id+"F0.wireOp",EDGE,"E10.2.7.6"),sQuery(id+"F0.wireOp",EDGE,"E10.2.7.7"),sQuery(id+"F0.wireOp",EDGE,"E10.3.0.0"),sQuery(id+"F0.wireOp",EDGE,"E10.3.0.1"),sQuery(id+"F0.wireOp",EDGE,"E10.3.0.2"),sQuery(id+"F0.wireOp",EDGE,"E10.3.0.3"),sQuery(id+"F0.wireOp",EDGE,"E10.3.0.4"),sQuery(id+"F0.wireOp",EDGE,"E10.3.0.5"),sQuery(id+"F0.wireOp",EDGE,"E10.3.0.6"),sQuery(id+"F0.wireOp",EDGE,"E10.3.0.7"),sQuery(id+"F0.wireOp",EDGE,"E10.3.1.0"),sQuery(id+"F0.wireOp",EDGE,"E10.3.1.1"),sQuery(id+"F0.wireOp",EDGE,"E10.3.1.2"),sQuery(id+"F0.wireOp",EDGE,"E10.3.1.3"),sQuery(id+"F0.wireOp",EDGE,"E10.3.1.4"),sQuery(id+"F0.wireOp",EDGE,"E10.3.1.5"),sQuery(id+"F0.wireOp",EDGE,"E10.3.1.6"),sQuery(id+"F0.wireOp",EDGE,"E10.3.1.7"),sQuery(id+"F0.wireOp",EDGE,"E10.3.2.0"),sQuery(id+"F0.wireOp",EDGE,"E10.3.2.1"),sQuery(id+"F0.wireOp",EDGE,"E10.3.2.2"),sQuery(id+"F0.wireOp",EDGE,"E10.3.2.3"),sQuery(id+"F0.wireOp",EDGE,"E10.3.2.4"),sQuery(id+"F0.wireOp",EDGE,"E10.3.2.5"),sQuery(id+"F0.wireOp",EDGE,"E10.3.2.6"),sQuery(id+"F0.wireOp",EDGE,"E10.3.2.7"),sQuery(id+"F0.wireOp",EDGE,"E10.3.3.0"),sQuery(id+"F0.wireOp",EDGE,"E10.3.3.1"),sQuery(id+"F0.wireOp",EDGE,"E10.3.3.2"),sQuery(id+"F0.wireOp",EDGE,"E10.3.3.3"),sQuery(id+"F0.wireOp",EDGE,"E10.3.3.4"),sQuery(id+"F0.wireOp",EDGE,"E10.3.3.5"),sQuery(id+"F0.wireOp",EDGE,"E10.3.3.6"),sQuery(id+"F0.wireOp",EDGE,"E10.3.3.7"),sQuery(id+"F0.wireOp",EDGE,"E10.3.4.0"),sQuery(id+"F0.wireOp",EDGE,"E10.3.4.1"),sQuery(id+"F0.wireOp",EDGE,"E10.3.4.2"),sQuery(id+"F0.wireOp",EDGE,"E10.3.4.3"),sQuery(id+"F0.wireOp",EDGE,"E10.3.4.4"),sQuery(id+"F0.wireOp",EDGE,"E10.3.4.5"),sQuery(id+"F0.wireOp",EDGE,"E10.3.4.6"),sQuery(id+"F0.wireOp",EDGE,"E10.3.4.7"),sQuery(id+"F0.wireOp",EDGE,"E10.3.5.0"),sQuery(id+"F0.wireOp",EDGE,"E10.3.5.1"),sQuery(id+"F0.wireOp",EDGE,"E10.3.5.2"),sQuery(id+"F0.wireOp",EDGE,"E10.3.5.3"),sQuery(id+"F0.wireOp",EDGE,"E10.3.5.4"),sQuery(id+"F0.wireOp",EDGE,"E10.3.5.5"),sQuery(id+"F0.wireOp",EDGE,"E10.3.5.6"),sQuery(id+"F0.wireOp",EDGE,"E10.3.5.7"),sQuery(id+"F0.wireOp",EDGE,"E10.3.6.0"),sQuery(id+"F0.wireOp",EDGE,"E10.3.6.1"),sQuery(id+"F0.wireOp",EDGE,"E10.3.6.2"),sQuery(id+"F0.wireOp",EDGE,"E10.3.6.3"),sQuery(id+"F0.wireOp",EDGE,"E10.3.6.4"),sQuery(id+"F0.wireOp",EDGE,"E10.3.6.5"),sQuery(id+"F0.wireOp",EDGE,"E10.3.6.6"),sQuery(id+"F0.wireOp",EDGE,"E10.3.6.7"),sQuery(id+"F0.wireOp",EDGE,"E10.3.7.0"),sQuery(id+"F0.wireOp",EDGE,"E10.3.7.1"),sQuery(id+"F0.wireOp",EDGE,"E10.3.7.2"),sQuery(id+"F0.wireOp",EDGE,"E10.3.7.3"),sQuery(id+"F0.wireOp",EDGE,"E10.3.7.4"),sQuery(id+"F0.wireOp",EDGE,"E10.3.7.5"),sQuery(id+"F0.wireOp",EDGE,"E10.3.7.6"),sQuery(id+"F0.wireOp",EDGE,"E10.3.7.7"),sQuery(id+"F0.wireOp",EDGE,"E10.4.0.0"),sQuery(id+"F0.wireOp",EDGE,"E10.4.0.1"),sQuery(id+"F0.wireOp",EDGE,"E10.4.0.2"),sQuery(id+"F0.wireOp",EDGE,"E10.4.0.3"),sQuery(id+"F0.wireOp",EDGE,"E10.4.0.4"),sQuery(id+"F0.wireOp",EDGE,"E10.4.0.5"),sQuery(id+"F0.wireOp",EDGE,"E10.4.0.6"),sQuery(id+"F0.wireOp",EDGE,"E10.4.0.7"),sQuery(id+"F0.wireOp",EDGE,"E10.4.1.0"),sQuery(id+"F0.wireOp",EDGE,"E10.4.1.1"),sQuery(id+"F0.wireOp",EDGE,"E10.4.1.2"),sQuery(id+"F0.wireOp",EDGE,"E10.4.1.3"),sQuery(id+"F0.wireOp",EDGE,"E10.4.1.4"),sQuery(id+"F0.wireOp",EDGE,"E10.4.1.5"),sQuery(id+"F0.wireOp",EDGE,"E10.4.1.6"),sQuery(id+"F0.wireOp",EDGE,"E10.4.1.7"),sQuery(id+"F0.wireOp",EDGE,"E10.4.2.0"),sQuery(id+"F0.wireOp",EDGE,"E10.4.2.1"),sQuery(id+"F0.wireOp",EDGE,"E10.4.2.2"),sQuery(id+"F0.wireOp",EDGE,"E10.4.2.3"),sQuery(id+"F0.wireOp",EDGE,"E10.4.2.4"),sQuery(id+"F0.wireOp",EDGE,"E10.4.2.5"),sQuery(id+"F0.wireOp",EDGE,"E10.4.2.6"),sQuery(id+"F0.wireOp",EDGE,"E10.4.2.7"),sQuery(id+"F0.wireOp",EDGE,"E10.4.3.0"),sQuery(id+"F0.wireOp",EDGE,"E10.4.3.1"),sQuery(id+"F0.wireOp",EDGE,"E10.4.3.2"),sQuery(id+"F0.wireOp",EDGE,"E10.4.3.3"),sQuery(id+"F0.wireOp",EDGE,"E10.4.3.4"),sQuery(id+"F0.wireOp",EDGE,"E10.4.3.5"),sQuery(id+"F0.wireOp",EDGE,"E10.4.3.6"),sQuery(id+"F0.wireOp",EDGE,"E10.4.3.7"),sQuery(id+"F0.wireOp",EDGE,"E10.4.4.0"),sQuery(id+"F0.wireOp",EDGE,"E10.4.4.1"),sQuery(id+"F0.wireOp",EDGE,"E10.4.4.2"),sQuery(id+"F0.wireOp",EDGE,"E10.4.4.3"),sQuery(id+"F0.wireOp",EDGE,"E10.4.4.4"),sQuery(id+"F0.wireOp",EDGE,"E10.4.4.5"),sQuery(id+"F0.wireOp",EDGE,"E10.4.4.6"),sQuery(id+"F0.wireOp",EDGE,"E10.4.4.7"),sQuery(id+"F0.wireOp",EDGE,"E10.4.5.0"),sQuery(id+"F0.wireOp",EDGE,"E10.4.5.1"),sQuery(id+"F0.wireOp",EDGE,"E10.4.5.2"),sQuery(id+"F0.wireOp",EDGE,"E10.4.5.3"),sQuery(id+"F0.wireOp",EDGE,"E10.4.5.4"),sQuery(id+"F0.wireOp",EDGE,"E10.4.5.5"),sQuery(id+"F0.wireOp",EDGE,"E10.4.5.6"),sQuery(id+"F0.wireOp",EDGE,"E10.4.5.7"),sQuery(id+"F0.wireOp",EDGE,"E10.4.6.0"),sQuery(id+"F0.wireOp",EDGE,"E10.4.6.1"),sQuery(id+"F0.wireOp",EDGE,"E10.4.6.2"),sQuery(id+"F0.wireOp",EDGE,"E10.4.6.3"),sQuery(id+"F0.wireOp",EDGE,"E10.4.6.4"),sQuery(id+"F0.wireOp",EDGE,"E10.4.6.5"),sQuery(id+"F0.wireOp",EDGE,"E10.4.6.6"),sQuery(id+"F0.wireOp",EDGE,"E10.4.6.7"),sQuery(id+"F0.wireOp",EDGE,"E10.4.7.0"),sQuery(id+"F0.wireOp",EDGE,"E10.4.7.1"),sQuery(id+"F0.wireOp",EDGE,"E10.4.7.2"),sQuery(id+"F0.wireOp",EDGE,"E10.4.7.3"),sQuery(id+"F0.wireOp",EDGE,"E10.4.7.4"),sQuery(id+"F0.wireOp",EDGE,"E10.4.7.5"),sQuery(id+"F0.wireOp",EDGE,"E10.4.7.6"),sQuery(id+"F0.wireOp",EDGE,"E10.4.7.7"),sQuery(id+"F0.wireOp",EDGE,"E10.5.0.0"),sQuery(id+"F0.wireOp",EDGE,"E10.5.0.1"),sQuery(id+"F0.wireOp",EDGE,"E10.5.0.2"),sQuery(id+"F0.wireOp",EDGE,"E10.5.0.3"),sQuery(id+"F0.wireOp",EDGE,"E10.5.0.4"),sQuery(id+"F0.wireOp",EDGE,"E10.5.0.5"),sQuery(id+"F0.wireOp",EDGE,"E10.5.0.6"),sQuery(id+"F0.wireOp",EDGE,"E10.5.0.7"),sQuery(id+"F0.wireOp",EDGE,"E10.5.1.0"),sQuery(id+"F0.wireOp",EDGE,"E10.5.1.1"),sQuery(id+"F0.wireOp",EDGE,"E10.5.1.2"),sQuery(id+"F0.wireOp",EDGE,"E10.5.1.3"),sQuery(id+"F0.wireOp",EDGE,"E10.5.1.4"),sQuery(id+"F0.wireOp",EDGE,"E10.5.1.5"),sQuery(id+"F0.wireOp",EDGE,"E10.5.1.6"),sQuery(id+"F0.wireOp",EDGE,"E10.5.1.7"),sQuery(id+"F0.wireOp",EDGE,"E10.5.2.0"),sQuery(id+"F0.wireOp",EDGE,"E10.5.2.1"),sQuery(id+"F0.wireOp",EDGE,"E10.5.2.2"),sQuery(id+"F0.wireOp",EDGE,"E10.5.2.3"),sQuery(id+"F0.wireOp",EDGE,"E10.5.2.4"),sQuery(id+"F0.wireOp",EDGE,"E10.5.2.5"),sQuery(id+"F0.wireOp",EDGE,"E10.5.2.6"),sQuery(id+"F0.wireOp",EDGE,"E10.5.2.7"),sQuery(id+"F0.wireOp",EDGE,"E10.5.3.0"),sQuery(id+"F0.wireOp",EDGE,"E10.5.3.1"),sQuery(id+"F0.wireOp",EDGE,"E10.5.3.2"),sQuery(id+"F0.wireOp",EDGE,"E10.5.3.3"),sQuery(id+"F0.wireOp",EDGE,"E10.5.3.4"),sQuery(id+"F0.wireOp",EDGE,"E10.5.3.5"),sQuery(id+"F0.wireOp",EDGE,"E10.5.3.6"),sQuery(id+"F0.wireOp",EDGE,"E10.5.3.7"),sQuery(id+"F0.wireOp",EDGE,"E10.5.4.0"),sQuery(id+"F0.wireOp",EDGE,"E10.5.4.1"),sQuery(id+"F0.wireOp",EDGE,"E10.5.4.2"),sQuery(id+"F0.wireOp",EDGE,"E10.5.4.3"),sQuery(id+"F0.wireOp",EDGE,"E10.5.4.4"),sQuery(id+"F0.wireOp",EDGE,"E10.5.4.5"),sQuery(id+"F0.wireOp",EDGE,"E10.5.4.6"),sQuery(id+"F0.wireOp",EDGE,"E10.5.4.7"),sQuery(id+"F0.wireOp",EDGE,"E10.5.5.0"),sQuery(id+"F0.wireOp",EDGE,"E10.5.5.1"),sQuery(id+"F0.wireOp",EDGE,"E10.5.5.2"),sQuery(id+"F0.wireOp",EDGE,"E10.5.5.3"),sQuery(id+"F0.wireOp",EDGE,"E10.5.5.4"),sQuery(id+"F0.wireOp",EDGE,"E10.5.5.5"),sQuery(id+"F0.wireOp",EDGE,"E10.5.5.6"),sQuery(id+"F0.wireOp",EDGE,"E10.5.5.7"),sQuery(id+"F0.wireOp",EDGE,"E10.5.6.0"),sQuery(id+"F0.wireOp",EDGE,"E10.5.6.1"),sQuery(id+"F0.wireOp",EDGE,"E10.5.6.2"),sQuery(id+"F0.wireOp",EDGE,"E10.5.6.3"),sQuery(id+"F0.wireOp",EDGE,"E10.5.6.4"),sQuery(id+"F0.wireOp",EDGE,"E10.5.6.5"),sQuery(id+"F0.wireOp",EDGE,"E10.5.6.6"),sQuery(id+"F0.wireOp",EDGE,"E10.5.6.7"),sQuery(id+"F0.wireOp",EDGE,"E10.5.7.0"),sQuery(id+"F0.wireOp",EDGE,"E10.5.7.1"),sQuery(id+"F0.wireOp",EDGE,"E10.5.7.2"),sQuery(id+"F0.wireOp",EDGE,"E10.5.7.3"),sQuery(id+"F0.wireOp",EDGE,"E10.5.7.4"),sQuery(id+"F0.wireOp",EDGE,"E10.5.7.5"),sQuery(id+"F0.wireOp",EDGE,"E10.5.7.6"),sQuery(id+"F0.wireOp",EDGE,"E10.5.7.7"),sQuery(id+"F0.wireOp",EDGE,"E10.6.0.0"),sQuery(id+"F0.wireOp",EDGE,"E10.6.0.1"),sQuery(id+"F0.wireOp",EDGE,"E10.6.0.2"),sQuery(id+"F0.wireOp",EDGE,"E10.6.0.3"),sQuery(id+"F0.wireOp",EDGE,"E10.6.0.4"),sQuery(id+"F0.wireOp",EDGE,"E10.6.0.5"),sQuery(id+"F0.wireOp",EDGE,"E10.6.0.6"),sQuery(id+"F0.wireOp",EDGE,"E10.6.0.7"),sQuery(id+"F0.wireOp",EDGE,"E10.6.1.0"),sQuery(id+"F0.wireOp",EDGE,"E10.6.1.1"),sQuery(id+"F0.wireOp",EDGE,"E10.6.1.2"),sQuery(id+"F0.wireOp",EDGE,"E10.6.1.3"),sQuery(id+"F0.wireOp",EDGE,"E10.6.1.4"),sQuery(id+"F0.wireOp",EDGE,"E10.6.1.5"),sQuery(id+"F0.wireOp",EDGE,"E10.6.1.6"),sQuery(id+"F0.wireOp",EDGE,"E10.6.1.7"),sQuery(id+"F0.wireOp",EDGE,"E10.6.2.0"),sQuery(id+"F0.wireOp",EDGE,"E10.6.2.1"),sQuery(id+"F0.wireOp",EDGE,"E10.6.2.2"),sQuery(id+"F0.wireOp",EDGE,"E10.6.2.3"),sQuery(id+"F0.wireOp",EDGE,"E10.6.2.4"),sQuery(id+"F0.wireOp",EDGE,"E10.6.2.5"),sQuery(id+"F0.wireOp",EDGE,"E10.6.2.6"),sQuery(id+"F0.wireOp",EDGE,"E10.6.2.7"),sQuery(id+"F0.wireOp",EDGE,"E10.6.3.0"),sQuery(id+"F0.wireOp",EDGE,"E10.6.3.1"),sQuery(id+"F0.wireOp",EDGE,"E10.6.3.2"),sQuery(id+"F0.wireOp",EDGE,"E10.6.3.3"),sQuery(id+"F0.wireOp",EDGE,"E10.6.3.4"),sQuery(id+"F0.wireOp",EDGE,"E10.6.3.5"),sQuery(id+"F0.wireOp",EDGE,"E10.6.3.6"),sQuery(id+"F0.wireOp",EDGE,"E10.6.3.7"),sQuery(id+"F0.wireOp",EDGE,"E10.6.4.0"),sQuery(id+"F0.wireOp",EDGE,"E10.6.4.1"),sQuery(id+"F0.wireOp",EDGE,"E10.6.4.2"),sQuery(id+"F0.wireOp",EDGE,"E10.6.4.3"),sQuery(id+"F0.wireOp",EDGE,"E10.6.4.4"),sQuery(id+"F0.wireOp",EDGE,"E10.6.4.5"),sQuery(id+"F0.wireOp",EDGE,"E10.6.4.6"),sQuery(id+"F0.wireOp",EDGE,"E10.6.4.7"),sQuery(id+"F0.wireOp",EDGE,"E10.6.5.0"),sQuery(id+"F0.wireOp",EDGE,"E10.6.5.1"),sQuery(id+"F0.wireOp",EDGE,"E10.6.5.2"),sQuery(id+"F0.wireOp",EDGE,"E10.6.5.3"),sQuery(id+"F0.wireOp",EDGE,"E10.6.5.4"),sQuery(id+"F0.wireOp",EDGE,"E10.6.5.5"),sQuery(id+"F0.wireOp",EDGE,"E10.6.5.6"),sQuery(id+"F0.wireOp",EDGE,"E10.6.5.7"),sQuery(id+"F0.wireOp",EDGE,"E10.6.6.0"),sQuery(id+"F0.wireOp",EDGE,"E10.6.6.1"),sQuery(id+"F0.wireOp",EDGE,"E10.6.6.2"),sQuery(id+"F0.wireOp",EDGE,"E10.6.6.3"),sQuery(id+"F0.wireOp",EDGE,"E10.6.6.4"),sQuery(id+"F0.wireOp",EDGE,"E10.6.6.5"),sQuery(id+"F0.wireOp",EDGE,"E10.6.6.6"),sQuery(id+"F0.wireOp",EDGE,"E10.6.6.7"),sQuery(id+"F0.wireOp",EDGE,"E10.6.7.0"),sQuery(id+"F0.wireOp",EDGE,"E10.6.7.1"),sQuery(id+"F0.wireOp",EDGE,"E10.6.7.2"),sQuery(id+"F0.wireOp",EDGE,"E10.6.7.3"),sQuery(id+"F0.wireOp",EDGE,"E10.6.7.4"),sQuery(id+"F0.wireOp",EDGE,"E10.6.7.5"),sQuery(id+"F0.wireOp",EDGE,"E10.6.7.6"),sQuery(id+"F0.wireOp",EDGE,"E10.6.7.7"),sQuery(id+"F0.wireOp",EDGE,"E10.7.0.0"),sQuery(id+"F0.wireOp",EDGE,"E10.7.0.1"),sQuery(id+"F0.wireOp",EDGE,"E10.7.0.2"),sQuery(id+"F0.wireOp",EDGE,"E10.7.0.3"),sQuery(id+"F0.wireOp",EDGE,"E10.7.0.4"),sQuery(id+"F0.wireOp",EDGE,"E10.7.0.5"),sQuery(id+"F0.wireOp",EDGE,"E10.7.0.6"),sQuery(id+"F0.wireOp",EDGE,"E10.7.0.7"),sQuery(id+"F0.wireOp",EDGE,"E10.7.1.0"),sQuery(id+"F0.wireOp",EDGE,"E10.7.1.1"),sQuery(id+"F0.wireOp",EDGE,"E10.7.1.2"),sQuery(id+"F0.wireOp",EDGE,"E10.7.1.3"),sQuery(id+"F0.wireOp",EDGE,"E10.7.1.4"),sQuery(id+"F0.wireOp",EDGE,"E10.7.1.5"),sQuery(id+"F0.wireOp",EDGE,"E10.7.1.6"),sQuery(id+"F0.wireOp",EDGE,"E10.7.1.7"),sQuery(id+"F0.wireOp",EDGE,"E10.7.2.0"),sQuery(id+"F0.wireOp",EDGE,"E10.7.2.1"),sQuery(id+"F0.wireOp",EDGE,"E10.7.2.2"),sQuery(id+"F0.wireOp",EDGE,"E10.7.2.3"),sQuery(id+"F0.wireOp",EDGE,"E10.7.2.4"),sQuery(id+"F0.wireOp",EDGE,"E10.7.2.5"),sQuery(id+"F0.wireOp",EDGE,"E10.7.2.6"),sQuery(id+"F0.wireOp",EDGE,"E10.7.2.7"),sQuery(id+"F0.wireOp",EDGE,"E10.7.3.0"),sQuery(id+"F0.wireOp",EDGE,"E10.7.3.1"),sQuery(id+"F0.wireOp",EDGE,"E10.7.3.2"),sQuery(id+"F0.wireOp",EDGE,"E10.7.3.3"),sQuery(id+"F0.wireOp",EDGE,"E10.7.3.4"),sQuery(id+"F0.wireOp",EDGE,"E10.7.3.5"),sQuery(id+"F0.wireOp",EDGE,"E10.7.3.6"),sQuery(id+"F0.wireOp",EDGE,"E10.7.3.7"),sQuery(id+"F0.wireOp",EDGE,"E10.7.4.0"),sQuery(id+"F0.wireOp",EDGE,"E10.7.4.1"),sQuery(id+"F0.wireOp",EDGE,"E10.7.4.2"),sQuery(id+"F0.wireOp",EDGE,"E10.7.4.3"),sQuery(id+"F0.wireOp",EDGE,"E10.7.4.4"),sQuery(id+"F0.wireOp",EDGE,"E10.7.4.5"),sQuery(id+"F0.wireOp",EDGE,"E10.7.4.6"),sQuery(id+"F0.wireOp",EDGE,"E10.7.4.7"),sQuery(id+"F0.wireOp",EDGE,"E10.7.5.0"),sQuery(id+"F0.wireOp",EDGE,"E10.7.5.1"),sQuery(id+"F0.wireOp",EDGE,"E10.7.5.2"),sQuery(id+"F0.wireOp",EDGE,"E10.7.5.3"),sQuery(id+"F0.wireOp",EDGE,"E10.7.5.4"),sQuery(id+"F0.wireOp",EDGE,"E10.7.5.5"),sQuery(id+"F0.wireOp",EDGE,"E10.7.5.6"),sQuery(id+"F0.wireOp",EDGE,"E10.7.5.7"),sQuery(id+"F0.wireOp",EDGE,"E10.7.6.0"),sQuery(id+"F0.wireOp",EDGE,"E10.7.6.1"),sQuery(id+"F0.wireOp",EDGE,"E10.7.6.2"),sQuery(id+"F0.wireOp",EDGE,"E10.7.6.3"),sQuery(id+"F0.wireOp",EDGE,"E10.7.6.4"),sQuery(id+"F0.wireOp",EDGE,"E10.7.6.5"),sQuery(id+"F0.wireOp",EDGE,"E10.7.6.6"),sQuery(id+"F0.wireOp",EDGE,"E10.7.6.7"),sQuery(id+"F0.wireOp",EDGE,"E10.7.7.0"),sQuery(id+"F0.wireOp",EDGE,"E10.7.7.1"),sQuery(id+"F0.wireOp",EDGE,"E10.7.7.2"),sQuery(id+"F0.wireOp",EDGE,"E10.7.7.3"),sQuery(id+"F0.wireOp",EDGE,"E10.7.7.4"),sQuery(id+"F0.wireOp",EDGE,"E10.7.7.5"),sQuery(id+"F0.wireOp",EDGE,"E10.7.7.6"),sQuery(id+"F0.wireOp",EDGE,"E10.7.7.7")])],"isStart":false});
            var sketch = newSketch(context, id + "F6", { "sketchPlane" : qUnion([Q0])});
            skLineSegment(sketch, "E16.bottom", {"start": v(-69.87, 72.35) * mm, "end": v(-59.07, 72.35) * mm});
            skLineSegment(sketch, "E16.top", {"start": v(-69.87, 56.48) * mm, "end": v(-59.07, 56.48) * mm});
            skLineSegment(sketch, "E16.left", {"start": v(-72.4, 69.81) * mm, "end": v(-72.4, 59.02) * mm});
            skLineSegment(sketch, "E16.right", {"start": v(-56.53, 69.81) * mm, "end": v(-56.53, 59.02) * mm});
            skPoint(sketch, "E17.visualSharp", {"position": v(-72.4, 72.35) * mm});
            skArc(sketch, "E17.filletArc", {"start": v(-69.87, 72.35) * mm, "mid": v(-71.66, 71.6) * mm, "end": v(-72.4, 69.81) * mm});
            skPoint(sketch, "E18.visualSharp", {"position": v(-56.53, 56.48) * mm});
            skArc(sketch, "E18.filletArc", {"start": v(-59.07, 56.48) * mm, "mid": v(-57.28, 57.22) * mm, "end": v(-56.53, 59.02) * mm});
            skPoint(sketch, "E19.visualSharp", {"position": v(-72.4, 56.48) * mm});
            skArc(sketch, "E19.filletArc", {"start": v(-72.4, 59.02) * mm, "mid": v(-71.66, 57.22) * mm, "end": v(-69.87, 56.48) * mm});
            skPoint(sketch, "E20.visualSharp", {"position": v(-56.53, 72.35) * mm});
            skArc(sketch, "E20.filletArc", {"start": v(-56.53, 69.81) * mm, "mid": v(-57.28, 71.6) * mm, "end": v(-59.07, 72.35) * mm});
            skLineSegment(sketch, "E21.0.1.0", {"start": v(-69.87, 53.94) * mm, "end": v(-59.07, 53.94) * mm});
            skArc(sketch, "E21.0.1.1", {"start": v(-56.53, 51.4) * mm, "mid": v(-57.28, 53.2) * mm, "end": v(-59.07, 53.94) * mm});
            skLineSegment(sketch, "E21.0.1.2", {"start": v(-56.53, 51.4) * mm, "end": v(-56.53, 40.6) * mm});
            skArc(sketch, "E21.0.1.3", {"start": v(-59.07, 38.06) * mm, "mid": v(-57.28, 38.8) * mm, "end": v(-56.53, 40.6) * mm});
            skLineSegment(sketch, "E21.0.1.4", {"start": v(-69.87, 38.06) * mm, "end": v(-59.07, 38.06) * mm});
            skArc(sketch, "E21.0.1.5", {"start": v(-72.4, 40.6) * mm, "mid": v(-71.66, 38.8) * mm, "end": v(-69.87, 38.06) * mm});
            skLineSegment(sketch, "E21.0.1.6", {"start": v(-72.4, 51.4) * mm, "end": v(-72.4, 40.6) * mm});
            skArc(sketch, "E21.0.1.7", {"start": v(-69.87, 53.94) * mm, "mid": v(-71.66, 53.2) * mm, "end": v(-72.4, 51.4) * mm});
            skLineSegment(sketch, "E21.0.2.0", {"start": v(-69.87, 35.52) * mm, "end": v(-59.07, 35.52) * mm});
            skArc(sketch, "E21.0.2.1", {"start": v(-56.53, 32.98) * mm, "mid": v(-57.28, 34.78) * mm, "end": v(-59.07, 35.52) * mm});
            skLineSegment(sketch, "E21.0.2.2", {"start": v(-56.53, 32.98) * mm, "end": v(-56.53, 22.19) * mm});
            skArc(sketch, "E21.0.2.3", {"start": v(-59.07, 19.65) * mm, "mid": v(-57.28, 20.4) * mm, "end": v(-56.53, 22.19) * mm});
            skLineSegment(sketch, "E21.0.2.4", {"start": v(-69.87, 19.65) * mm, "end": v(-59.07, 19.65) * mm});
            skArc(sketch, "E21.0.2.5", {"start": v(-72.4, 22.19) * mm, "mid": v(-71.66, 20.4) * mm, "end": v(-69.87, 19.65) * mm});
            skLineSegment(sketch, "E21.0.2.6", {"start": v(-72.4, 32.98) * mm, "end": v(-72.4, 22.19) * mm});
            skArc(sketch, "E21.0.2.7", {"start": v(-69.87, 35.52) * mm, "mid": v(-71.66, 34.78) * mm, "end": v(-72.4, 32.98) * mm});
            skLineSegment(sketch, "E21.0.3.0", {"start": v(-69.87, 17.1) * mm, "end": v(-59.07, 17.1) * mm});
            skArc(sketch, "E21.0.3.1", {"start": v(-56.53, 14.57) * mm, "mid": v(-57.28, 16.36) * mm, "end": v(-59.07, 17.1) * mm});
            skLineSegment(sketch, "E21.0.3.2", {"start": v(-56.53, 14.57) * mm, "end": v(-56.53, 3.77) * mm});
            skArc(sketch, "E21.0.3.3", {"start": v(-59.07, 1.23) * mm, "mid": v(-57.28, 1.98) * mm, "end": v(-56.53, 3.77) * mm});
            skLineSegment(sketch, "E21.0.3.4", {"start": v(-69.87, 1.23) * mm, "end": v(-59.07, 1.23) * mm});
            skArc(sketch, "E21.0.3.5", {"start": v(-72.4, 3.77) * mm, "mid": v(-71.66, 1.98) * mm, "end": v(-69.87, 1.23) * mm});
            skLineSegment(sketch, "E21.0.3.6", {"start": v(-72.4, 14.57) * mm, "end": v(-72.4, 3.77) * mm});
            skArc(sketch, "E21.0.3.7", {"start": v(-69.87, 17.1) * mm, "mid": v(-71.66, 16.36) * mm, "end": v(-72.4, 14.57) * mm});
            skLineSegment(sketch, "E21.0.4.0", {"start": v(-69.87, -1.3) * mm, "end": v(-59.07, -1.3) * mm});
            skArc(sketch, "E21.0.4.1", {"start": v(-56.53, -3.85) * mm, "mid": v(-57.28, -2.05) * mm, "end": v(-59.07, -1.3) * mm});
            skLineSegment(sketch, "E21.0.4.2", {"start": v(-56.53, -3.85) * mm, "end": v(-56.53, -14.64) * mm});
            skArc(sketch, "E21.0.4.3", {"start": v(-59.07, -17.18) * mm, "mid": v(-57.28, -16.44) * mm, "end": v(-56.53, -14.64) * mm});
            skLineSegment(sketch, "E21.0.4.4", {"start": v(-69.87, -17.18) * mm, "end": v(-59.07, -17.18) * mm});
            skArc(sketch, "E21.0.4.5", {"start": v(-72.4, -14.64) * mm, "mid": v(-71.66, -16.44) * mm, "end": v(-69.87, -17.18) * mm});
            skLineSegment(sketch, "E21.0.4.6", {"start": v(-72.4, -3.85) * mm, "end": v(-72.4, -14.64) * mm});
            skArc(sketch, "E21.0.4.7", {"start": v(-69.87, -1.3) * mm, "mid": v(-71.66, -2.05) * mm, "end": v(-72.4, -3.85) * mm});
            skLineSegment(sketch, "E21.0.5.0", {"start": v(-69.87, -19.72) * mm, "end": v(-59.07, -19.72) * mm});
            skArc(sketch, "E21.0.5.1", {"start": v(-56.53, -22.26) * mm, "mid": v(-57.28, -20.47) * mm, "end": v(-59.07, -19.72) * mm});
            skLineSegment(sketch, "E21.0.5.2", {"start": v(-56.53, -22.26) * mm, "end": v(-56.53, -33.06) * mm});
            skArc(sketch, "E21.0.5.3", {"start": v(-59.07, -35.6) * mm, "mid": v(-57.28, -34.85) * mm, "end": v(-56.53, -33.06) * mm});
            skLineSegment(sketch, "E21.0.5.4", {"start": v(-69.87, -35.6) * mm, "end": v(-59.07, -35.6) * mm});
            skArc(sketch, "E21.0.5.5", {"start": v(-72.4, -33.06) * mm, "mid": v(-71.66, -34.85) * mm, "end": v(-69.87, -35.6) * mm});
            skLineSegment(sketch, "E21.0.5.6", {"start": v(-72.4, -22.26) * mm, "end": v(-72.4, -33.06) * mm});
            skArc(sketch, "E21.0.5.7", {"start": v(-69.87, -19.72) * mm, "mid": v(-71.66, -20.47) * mm, "end": v(-72.4, -22.26) * mm});
            skLineSegment(sketch, "E21.0.6.0", {"start": v(-69.87, -38.14) * mm, "end": v(-59.07, -38.14) * mm});
            skArc(sketch, "E21.0.6.1", {"start": v(-56.53, -40.68) * mm, "mid": v(-57.28, -38.88) * mm, "end": v(-59.07, -38.14) * mm});
            skLineSegment(sketch, "E21.0.6.2", {"start": v(-56.53, -40.68) * mm, "end": v(-56.53, -51.47) * mm});
            skArc(sketch, "E21.0.6.3", {"start": v(-59.07, -54.01) * mm, "mid": v(-57.28, -53.27) * mm, "end": v(-56.53, -51.47) * mm});
            skLineSegment(sketch, "E21.0.6.4", {"start": v(-69.87, -54.01) * mm, "end": v(-59.07, -54.01) * mm});
            skArc(sketch, "E21.0.6.5", {"start": v(-72.4, -51.47) * mm, "mid": v(-71.66, -53.27) * mm, "end": v(-69.87, -54.01) * mm});
            skLineSegment(sketch, "E21.0.6.6", {"start": v(-72.4, -40.68) * mm, "end": v(-72.4, -51.47) * mm});
            skArc(sketch, "E21.0.6.7", {"start": v(-69.87, -38.14) * mm, "mid": v(-71.66, -38.88) * mm, "end": v(-72.4, -40.68) * mm});
            skLineSegment(sketch, "E21.0.7.0", {"start": v(-69.87, -56.55) * mm, "end": v(-59.07, -56.55) * mm});
            skArc(sketch, "E21.0.7.1", {"start": v(-56.53, -59.1) * mm, "mid": v(-57.28, -57.3) * mm, "end": v(-59.07, -56.55) * mm});
            skLineSegment(sketch, "E21.0.7.2", {"start": v(-56.53, -59.1) * mm, "end": v(-56.53, -69.89) * mm});
            skArc(sketch, "E21.0.7.3", {"start": v(-59.07, -72.43) * mm, "mid": v(-57.28, -71.68) * mm, "end": v(-56.53, -69.89) * mm});
            skLineSegment(sketch, "E21.0.7.4", {"start": v(-69.87, -72.43) * mm, "end": v(-59.07, -72.43) * mm});
            skArc(sketch, "E21.0.7.5", {"start": v(-72.4, -69.89) * mm, "mid": v(-71.66, -71.68) * mm, "end": v(-69.87, -72.43) * mm});
            skLineSegment(sketch, "E21.0.7.6", {"start": v(-72.4, -59.1) * mm, "end": v(-72.4, -69.89) * mm});
            skArc(sketch, "E21.0.7.7", {"start": v(-69.87, -56.55) * mm, "mid": v(-71.66, -57.3) * mm, "end": v(-72.4, -59.1) * mm});
            skLineSegment(sketch, "E21.1.0.0", {"start": v(-51.45, 72.35) * mm, "end": v(-40.66, 72.35) * mm});
            skArc(sketch, "E21.1.0.1", {"start": v(-38.12, 69.81) * mm, "mid": v(-38.86, 71.6) * mm, "end": v(-40.66, 72.35) * mm});
            skLineSegment(sketch, "E21.1.0.2", {"start": v(-38.12, 69.81) * mm, "end": v(-38.12, 59.02) * mm});
            skArc(sketch, "E21.1.0.3", {"start": v(-40.66, 56.48) * mm, "mid": v(-38.86, 57.22) * mm, "end": v(-38.12, 59.02) * mm});
            skLineSegment(sketch, "E21.1.0.4", {"start": v(-51.45, 56.48) * mm, "end": v(-40.66, 56.48) * mm});
            skArc(sketch, "E21.1.0.5", {"start": v(-54, 59.02) * mm, "mid": v(-53.25, 57.22) * mm, "end": v(-51.45, 56.48) * mm});
            skLineSegment(sketch, "E21.1.0.6", {"start": v(-54, 69.81) * mm, "end": v(-54, 59.02) * mm});
            skArc(sketch, "E21.1.0.7", {"start": v(-51.45, 72.35) * mm, "mid": v(-53.25, 71.6) * mm, "end": v(-54, 69.81) * mm});
            skLineSegment(sketch, "E21.1.1.0", {"start": v(-51.45, 53.94) * mm, "end": v(-40.66, 53.94) * mm});
            skArc(sketch, "E21.1.1.1", {"start": v(-38.12, 51.4) * mm, "mid": v(-38.86, 53.2) * mm, "end": v(-40.66, 53.94) * mm});
            skLineSegment(sketch, "E21.1.1.2", {"start": v(-38.12, 51.4) * mm, "end": v(-38.12, 40.6) * mm});
            skArc(sketch, "E21.1.1.3", {"start": v(-40.66, 38.06) * mm, "mid": v(-38.86, 38.8) * mm, "end": v(-38.12, 40.6) * mm});
            skLineSegment(sketch, "E21.1.1.4", {"start": v(-51.45, 38.06) * mm, "end": v(-40.66, 38.06) * mm});
            skArc(sketch, "E21.1.1.5", {"start": v(-54, 40.6) * mm, "mid": v(-53.25, 38.8) * mm, "end": v(-51.45, 38.06) * mm});
            skLineSegment(sketch, "E21.1.1.6", {"start": v(-54, 51.4) * mm, "end": v(-54, 40.6) * mm});
            skArc(sketch, "E21.1.1.7", {"start": v(-51.45, 53.94) * mm, "mid": v(-53.25, 53.2) * mm, "end": v(-54, 51.4) * mm});
            skLineSegment(sketch, "E21.1.2.0", {"start": v(-51.45, 35.52) * mm, "end": v(-40.66, 35.52) * mm});
            skArc(sketch, "E21.1.2.1", {"start": v(-38.12, 32.98) * mm, "mid": v(-38.86, 34.78) * mm, "end": v(-40.66, 35.52) * mm});
            skLineSegment(sketch, "E21.1.2.2", {"start": v(-38.12, 32.98) * mm, "end": v(-38.12, 22.19) * mm});
            skArc(sketch, "E21.1.2.3", {"start": v(-40.66, 19.65) * mm, "mid": v(-38.86, 20.4) * mm, "end": v(-38.12, 22.19) * mm});
            skLineSegment(sketch, "E21.1.2.4", {"start": v(-51.45, 19.65) * mm, "end": v(-40.66, 19.65) * mm});
            skArc(sketch, "E21.1.2.5", {"start": v(-54, 22.19) * mm, "mid": v(-53.25, 20.4) * mm, "end": v(-51.45, 19.65) * mm});
            skLineSegment(sketch, "E21.1.2.6", {"start": v(-54, 32.98) * mm, "end": v(-54, 22.19) * mm});
            skArc(sketch, "E21.1.2.7", {"start": v(-51.45, 35.52) * mm, "mid": v(-53.25, 34.78) * mm, "end": v(-54, 32.98) * mm});
            skLineSegment(sketch, "E21.1.3.0", {"start": v(-51.45, 17.1) * mm, "end": v(-40.66, 17.1) * mm});
            skArc(sketch, "E21.1.3.1", {"start": v(-38.12, 14.57) * mm, "mid": v(-38.86, 16.36) * mm, "end": v(-40.66, 17.1) * mm});
            skLineSegment(sketch, "E21.1.3.2", {"start": v(-38.12, 14.57) * mm, "end": v(-38.12, 3.77) * mm});
            skArc(sketch, "E21.1.3.3", {"start": v(-40.66, 1.23) * mm, "mid": v(-38.86, 1.98) * mm, "end": v(-38.12, 3.77) * mm});
            skLineSegment(sketch, "E21.1.3.4", {"start": v(-51.45, 1.23) * mm, "end": v(-40.66, 1.23) * mm});
            skArc(sketch, "E21.1.3.5", {"start": v(-54, 3.77) * mm, "mid": v(-53.25, 1.98) * mm, "end": v(-51.45, 1.23) * mm});
            skLineSegment(sketch, "E21.1.3.6", {"start": v(-54, 14.57) * mm, "end": v(-54, 3.77) * mm});
            skArc(sketch, "E21.1.3.7", {"start": v(-51.45, 17.1) * mm, "mid": v(-53.25, 16.36) * mm, "end": v(-54, 14.57) * mm});
            skLineSegment(sketch, "E21.1.4.0", {"start": v(-51.45, -1.3) * mm, "end": v(-40.66, -1.3) * mm});
            skArc(sketch, "E21.1.4.1", {"start": v(-38.12, -3.85) * mm, "mid": v(-38.86, -2.05) * mm, "end": v(-40.66, -1.3) * mm});
            skLineSegment(sketch, "E21.1.4.2", {"start": v(-38.12, -3.85) * mm, "end": v(-38.12, -14.64) * mm});
            skArc(sketch, "E21.1.4.3", {"start": v(-40.66, -17.18) * mm, "mid": v(-38.86, -16.44) * mm, "end": v(-38.12, -14.64) * mm});
            skLineSegment(sketch, "E21.1.4.4", {"start": v(-51.45, -17.18) * mm, "end": v(-40.66, -17.18) * mm});
            skArc(sketch, "E21.1.4.5", {"start": v(-54, -14.64) * mm, "mid": v(-53.25, -16.44) * mm, "end": v(-51.45, -17.18) * mm});
            skLineSegment(sketch, "E21.1.4.6", {"start": v(-54, -3.85) * mm, "end": v(-54, -14.64) * mm});
            skArc(sketch, "E21.1.4.7", {"start": v(-51.45, -1.3) * mm, "mid": v(-53.25, -2.05) * mm, "end": v(-54, -3.85) * mm});
            skLineSegment(sketch, "E21.1.5.0", {"start": v(-51.45, -19.72) * mm, "end": v(-40.66, -19.72) * mm});
            skArc(sketch, "E21.1.5.1", {"start": v(-38.12, -22.26) * mm, "mid": v(-38.86, -20.47) * mm, "end": v(-40.66, -19.72) * mm});
            skLineSegment(sketch, "E21.1.5.2", {"start": v(-38.12, -22.26) * mm, "end": v(-38.12, -33.06) * mm});
            skArc(sketch, "E21.1.5.3", {"start": v(-40.66, -35.6) * mm, "mid": v(-38.86, -34.85) * mm, "end": v(-38.12, -33.06) * mm});
            skLineSegment(sketch, "E21.1.5.4", {"start": v(-51.45, -35.6) * mm, "end": v(-40.66, -35.6) * mm});
            skArc(sketch, "E21.1.5.5", {"start": v(-54, -33.06) * mm, "mid": v(-53.25, -34.85) * mm, "end": v(-51.45, -35.6) * mm});
            skLineSegment(sketch, "E21.1.5.6", {"start": v(-54, -22.26) * mm, "end": v(-54, -33.06) * mm});
            skArc(sketch, "E21.1.5.7", {"start": v(-51.45, -19.72) * mm, "mid": v(-53.25, -20.47) * mm, "end": v(-54, -22.26) * mm});
            skLineSegment(sketch, "E21.1.6.0", {"start": v(-51.45, -38.14) * mm, "end": v(-40.66, -38.14) * mm});
            skArc(sketch, "E21.1.6.1", {"start": v(-38.12, -40.68) * mm, "mid": v(-38.86, -38.88) * mm, "end": v(-40.66, -38.14) * mm});
            skLineSegment(sketch, "E21.1.6.2", {"start": v(-38.12, -40.68) * mm, "end": v(-38.12, -51.47) * mm});
            skArc(sketch, "E21.1.6.3", {"start": v(-40.66, -54.01) * mm, "mid": v(-38.86, -53.27) * mm, "end": v(-38.12, -51.47) * mm});
            skLineSegment(sketch, "E21.1.6.4", {"start": v(-51.45, -54.01) * mm, "end": v(-40.66, -54.01) * mm});
            skArc(sketch, "E21.1.6.5", {"start": v(-54, -51.47) * mm, "mid": v(-53.25, -53.27) * mm, "end": v(-51.45, -54.01) * mm});
            skLineSegment(sketch, "E21.1.6.6", {"start": v(-54, -40.68) * mm, "end": v(-54, -51.47) * mm});
            skArc(sketch, "E21.1.6.7", {"start": v(-51.45, -38.14) * mm, "mid": v(-53.25, -38.88) * mm, "end": v(-54, -40.68) * mm});
            skLineSegment(sketch, "E21.1.7.0", {"start": v(-51.45, -56.55) * mm, "end": v(-40.66, -56.55) * mm});
            skArc(sketch, "E21.1.7.1", {"start": v(-38.12, -59.1) * mm, "mid": v(-38.86, -57.3) * mm, "end": v(-40.66, -56.55) * mm});
            skLineSegment(sketch, "E21.1.7.2", {"start": v(-38.12, -59.1) * mm, "end": v(-38.12, -69.89) * mm});
            skArc(sketch, "E21.1.7.3", {"start": v(-40.66, -72.43) * mm, "mid": v(-38.86, -71.68) * mm, "end": v(-38.12, -69.89) * mm});
            skLineSegment(sketch, "E21.1.7.4", {"start": v(-51.45, -72.43) * mm, "end": v(-40.66, -72.43) * mm});
            skArc(sketch, "E21.1.7.5", {"start": v(-54, -69.89) * mm, "mid": v(-53.25, -71.68) * mm, "end": v(-51.45, -72.43) * mm});
            skLineSegment(sketch, "E21.1.7.6", {"start": v(-54, -59.1) * mm, "end": v(-54, -69.89) * mm});
            skArc(sketch, "E21.1.7.7", {"start": v(-51.45, -56.55) * mm, "mid": v(-53.25, -57.3) * mm, "end": v(-54, -59.1) * mm});
            skLineSegment(sketch, "E21.2.0.0", {"start": v(-33.04, 72.35) * mm, "end": v(-22.24, 72.35) * mm});
            skArc(sketch, "E21.2.0.1", {"start": v(-19.7, 69.81) * mm, "mid": v(-20.45, 71.6) * mm, "end": v(-22.24, 72.35) * mm});
            skLineSegment(sketch, "E21.2.0.2", {"start": v(-19.7, 69.81) * mm, "end": v(-19.7, 59.02) * mm});
            skArc(sketch, "E21.2.0.3", {"start": v(-22.24, 56.48) * mm, "mid": v(-20.45, 57.22) * mm, "end": v(-19.7, 59.02) * mm});
            skLineSegment(sketch, "E21.2.0.4", {"start": v(-33.04, 56.48) * mm, "end": v(-22.24, 56.48) * mm});
            skArc(sketch, "E21.2.0.5", {"start": v(-35.58, 59.02) * mm, "mid": v(-34.83, 57.22) * mm, "end": v(-33.04, 56.48) * mm});
            skLineSegment(sketch, "E21.2.0.6", {"start": v(-35.58, 69.81) * mm, "end": v(-35.58, 59.02) * mm});
            skArc(sketch, "E21.2.0.7", {"start": v(-33.04, 72.35) * mm, "mid": v(-34.83, 71.6) * mm, "end": v(-35.58, 69.81) * mm});
            skLineSegment(sketch, "E21.2.1.0", {"start": v(-33.04, 53.94) * mm, "end": v(-22.24, 53.94) * mm});
            skArc(sketch, "E21.2.1.1", {"start": v(-19.7, 51.4) * mm, "mid": v(-20.45, 53.2) * mm, "end": v(-22.24, 53.94) * mm});
            skLineSegment(sketch, "E21.2.1.2", {"start": v(-19.7, 51.4) * mm, "end": v(-19.7, 40.6) * mm});
            skArc(sketch, "E21.2.1.3", {"start": v(-22.24, 38.06) * mm, "mid": v(-20.45, 38.8) * mm, "end": v(-19.7, 40.6) * mm});
            skLineSegment(sketch, "E21.2.1.4", {"start": v(-33.04, 38.06) * mm, "end": v(-22.24, 38.06) * mm});
            skArc(sketch, "E21.2.1.5", {"start": v(-35.58, 40.6) * mm, "mid": v(-34.83, 38.8) * mm, "end": v(-33.04, 38.06) * mm});
            skLineSegment(sketch, "E21.2.1.6", {"start": v(-35.58, 51.4) * mm, "end": v(-35.58, 40.6) * mm});
            skArc(sketch, "E21.2.1.7", {"start": v(-33.04, 53.94) * mm, "mid": v(-34.83, 53.2) * mm, "end": v(-35.58, 51.4) * mm});
            skLineSegment(sketch, "E21.2.2.0", {"start": v(-33.04, 35.52) * mm, "end": v(-22.24, 35.52) * mm});
            skArc(sketch, "E21.2.2.1", {"start": v(-19.7, 32.98) * mm, "mid": v(-20.45, 34.78) * mm, "end": v(-22.24, 35.52) * mm});
            skLineSegment(sketch, "E21.2.2.2", {"start": v(-19.7, 32.98) * mm, "end": v(-19.7, 22.19) * mm});
            skArc(sketch, "E21.2.2.3", {"start": v(-22.24, 19.65) * mm, "mid": v(-20.45, 20.4) * mm, "end": v(-19.7, 22.19) * mm});
            skLineSegment(sketch, "E21.2.2.4", {"start": v(-33.04, 19.65) * mm, "end": v(-22.24, 19.65) * mm});
            skArc(sketch, "E21.2.2.5", {"start": v(-35.58, 22.19) * mm, "mid": v(-34.83, 20.4) * mm, "end": v(-33.04, 19.65) * mm});
            skLineSegment(sketch, "E21.2.2.6", {"start": v(-35.58, 32.98) * mm, "end": v(-35.58, 22.19) * mm});
            skArc(sketch, "E21.2.2.7", {"start": v(-33.04, 35.52) * mm, "mid": v(-34.83, 34.78) * mm, "end": v(-35.58, 32.98) * mm});
            skLineSegment(sketch, "E21.2.3.0", {"start": v(-33.04, 17.1) * mm, "end": v(-22.24, 17.1) * mm});
            skArc(sketch, "E21.2.3.1", {"start": v(-19.7, 14.57) * mm, "mid": v(-20.45, 16.36) * mm, "end": v(-22.24, 17.1) * mm});
            skLineSegment(sketch, "E21.2.3.2", {"start": v(-19.7, 14.57) * mm, "end": v(-19.7, 3.77) * mm});
            skArc(sketch, "E21.2.3.3", {"start": v(-22.24, 1.23) * mm, "mid": v(-20.45, 1.98) * mm, "end": v(-19.7, 3.77) * mm});
            skLineSegment(sketch, "E21.2.3.4", {"start": v(-33.04, 1.23) * mm, "end": v(-22.24, 1.23) * mm});
            skArc(sketch, "E21.2.3.5", {"start": v(-35.58, 3.77) * mm, "mid": v(-34.83, 1.98) * mm, "end": v(-33.04, 1.23) * mm});
            skLineSegment(sketch, "E21.2.3.6", {"start": v(-35.58, 14.57) * mm, "end": v(-35.58, 3.77) * mm});
            skArc(sketch, "E21.2.3.7", {"start": v(-33.04, 17.1) * mm, "mid": v(-34.83, 16.36) * mm, "end": v(-35.58, 14.57) * mm});
            skLineSegment(sketch, "E21.2.4.0", {"start": v(-33.04, -1.3) * mm, "end": v(-22.24, -1.3) * mm});
            skArc(sketch, "E21.2.4.1", {"start": v(-19.7, -3.85) * mm, "mid": v(-20.45, -2.05) * mm, "end": v(-22.24, -1.3) * mm});
            skLineSegment(sketch, "E21.2.4.2", {"start": v(-19.7, -3.85) * mm, "end": v(-19.7, -14.64) * mm});
            skArc(sketch, "E21.2.4.3", {"start": v(-22.24, -17.18) * mm, "mid": v(-20.45, -16.44) * mm, "end": v(-19.7, -14.64) * mm});
            skLineSegment(sketch, "E21.2.4.4", {"start": v(-33.04, -17.18) * mm, "end": v(-22.24, -17.18) * mm});
            skArc(sketch, "E21.2.4.5", {"start": v(-35.58, -14.64) * mm, "mid": v(-34.83, -16.44) * mm, "end": v(-33.04, -17.18) * mm});
            skLineSegment(sketch, "E21.2.4.6", {"start": v(-35.58, -3.85) * mm, "end": v(-35.58, -14.64) * mm});
            skArc(sketch, "E21.2.4.7", {"start": v(-33.04, -1.3) * mm, "mid": v(-34.83, -2.05) * mm, "end": v(-35.58, -3.85) * mm});
            skLineSegment(sketch, "E21.2.5.0", {"start": v(-33.04, -19.72) * mm, "end": v(-22.24, -19.72) * mm});
            skArc(sketch, "E21.2.5.1", {"start": v(-19.7, -22.26) * mm, "mid": v(-20.45, -20.47) * mm, "end": v(-22.24, -19.72) * mm});
            skLineSegment(sketch, "E21.2.5.2", {"start": v(-19.7, -22.26) * mm, "end": v(-19.7, -33.06) * mm});
            skArc(sketch, "E21.2.5.3", {"start": v(-22.24, -35.6) * mm, "mid": v(-20.45, -34.85) * mm, "end": v(-19.7, -33.06) * mm});
            skLineSegment(sketch, "E21.2.5.4", {"start": v(-33.04, -35.6) * mm, "end": v(-22.24, -35.6) * mm});
            skArc(sketch, "E21.2.5.5", {"start": v(-35.58, -33.06) * mm, "mid": v(-34.83, -34.85) * mm, "end": v(-33.04, -35.6) * mm});
            skLineSegment(sketch, "E21.2.5.6", {"start": v(-35.58, -22.26) * mm, "end": v(-35.58, -33.06) * mm});
            skArc(sketch, "E21.2.5.7", {"start": v(-33.04, -19.72) * mm, "mid": v(-34.83, -20.47) * mm, "end": v(-35.58, -22.26) * mm});
            skLineSegment(sketch, "E21.2.6.0", {"start": v(-33.04, -38.14) * mm, "end": v(-22.24, -38.14) * mm});
            skArc(sketch, "E21.2.6.1", {"start": v(-19.7, -40.68) * mm, "mid": v(-20.45, -38.88) * mm, "end": v(-22.24, -38.14) * mm});
            skLineSegment(sketch, "E21.2.6.2", {"start": v(-19.7, -40.68) * mm, "end": v(-19.7, -51.47) * mm});
            skArc(sketch, "E21.2.6.3", {"start": v(-22.24, -54.01) * mm, "mid": v(-20.45, -53.27) * mm, "end": v(-19.7, -51.47) * mm});
            skLineSegment(sketch, "E21.2.6.4", {"start": v(-33.04, -54.01) * mm, "end": v(-22.24, -54.01) * mm});
            skArc(sketch, "E21.2.6.5", {"start": v(-35.58, -51.47) * mm, "mid": v(-34.83, -53.27) * mm, "end": v(-33.04, -54.01) * mm});
            skLineSegment(sketch, "E21.2.6.6", {"start": v(-35.58, -40.68) * mm, "end": v(-35.58, -51.47) * mm});
            skArc(sketch, "E21.2.6.7", {"start": v(-33.04, -38.14) * mm, "mid": v(-34.83, -38.88) * mm, "end": v(-35.58, -40.68) * mm});
            skLineSegment(sketch, "E21.2.7.0", {"start": v(-33.04, -56.55) * mm, "end": v(-22.24, -56.55) * mm});
            skArc(sketch, "E21.2.7.1", {"start": v(-19.7, -59.1) * mm, "mid": v(-20.45, -57.3) * mm, "end": v(-22.24, -56.55) * mm});
            skLineSegment(sketch, "E21.2.7.2", {"start": v(-19.7, -59.1) * mm, "end": v(-19.7, -69.89) * mm});
            skArc(sketch, "E21.2.7.3", {"start": v(-22.24, -72.43) * mm, "mid": v(-20.45, -71.68) * mm, "end": v(-19.7, -69.89) * mm});
            skLineSegment(sketch, "E21.2.7.4", {"start": v(-33.04, -72.43) * mm, "end": v(-22.24, -72.43) * mm});
            skArc(sketch, "E21.2.7.5", {"start": v(-35.58, -69.89) * mm, "mid": v(-34.83, -71.68) * mm, "end": v(-33.04, -72.43) * mm});
            skLineSegment(sketch, "E21.2.7.6", {"start": v(-35.58, -59.1) * mm, "end": v(-35.58, -69.89) * mm});
            skArc(sketch, "E21.2.7.7", {"start": v(-33.04, -56.55) * mm, "mid": v(-34.83, -57.3) * mm, "end": v(-35.58, -59.1) * mm});
            skLineSegment(sketch, "E21.3.0.0", {"start": v(-14.62, 72.35) * mm, "end": v(-3.83, 72.35) * mm});
            skArc(sketch, "E21.3.0.1", {"start": v(-1.29, 69.81) * mm, "mid": v(-2.03, 71.6) * mm, "end": v(-3.83, 72.35) * mm});
            skLineSegment(sketch, "E21.3.0.2", {"start": v(-1.29, 69.81) * mm, "end": v(-1.29, 59.02) * mm});
            skArc(sketch, "E21.3.0.3", {"start": v(-3.83, 56.48) * mm, "mid": v(-2.03, 57.22) * mm, "end": v(-1.29, 59.02) * mm});
            skLineSegment(sketch, "E21.3.0.4", {"start": v(-14.62, 56.48) * mm, "end": v(-3.83, 56.48) * mm});
            skArc(sketch, "E21.3.0.5", {"start": v(-17.16, 59.02) * mm, "mid": v(-16.42, 57.22) * mm, "end": v(-14.62, 56.48) * mm});
            skLineSegment(sketch, "E21.3.0.6", {"start": v(-17.16, 69.81) * mm, "end": v(-17.16, 59.02) * mm});
            skArc(sketch, "E21.3.0.7", {"start": v(-14.62, 72.35) * mm, "mid": v(-16.42, 71.6) * mm, "end": v(-17.16, 69.81) * mm});
            skLineSegment(sketch, "E21.3.1.0", {"start": v(-14.62, 53.94) * mm, "end": v(-3.83, 53.94) * mm});
            skArc(sketch, "E21.3.1.1", {"start": v(-1.29, 51.4) * mm, "mid": v(-2.03, 53.2) * mm, "end": v(-3.83, 53.94) * mm});
            skLineSegment(sketch, "E21.3.1.2", {"start": v(-1.29, 51.4) * mm, "end": v(-1.29, 40.6) * mm});
            skArc(sketch, "E21.3.1.3", {"start": v(-3.83, 38.06) * mm, "mid": v(-2.03, 38.8) * mm, "end": v(-1.29, 40.6) * mm});
            skLineSegment(sketch, "E21.3.1.4", {"start": v(-14.62, 38.06) * mm, "end": v(-3.83, 38.06) * mm});
            skArc(sketch, "E21.3.1.5", {"start": v(-17.16, 40.6) * mm, "mid": v(-16.42, 38.8) * mm, "end": v(-14.62, 38.06) * mm});
            skLineSegment(sketch, "E21.3.1.6", {"start": v(-17.16, 51.4) * mm, "end": v(-17.16, 40.6) * mm});
            skArc(sketch, "E21.3.1.7", {"start": v(-14.62, 53.94) * mm, "mid": v(-16.42, 53.2) * mm, "end": v(-17.16, 51.4) * mm});
            skLineSegment(sketch, "E21.3.2.0", {"start": v(-14.62, 35.52) * mm, "end": v(-3.83, 35.52) * mm});
            skArc(sketch, "E21.3.2.1", {"start": v(-1.29, 32.98) * mm, "mid": v(-2.03, 34.78) * mm, "end": v(-3.83, 35.52) * mm});
            skLineSegment(sketch, "E21.3.2.2", {"start": v(-1.29, 32.98) * mm, "end": v(-1.29, 22.19) * mm});
            skArc(sketch, "E21.3.2.3", {"start": v(-3.83, 19.65) * mm, "mid": v(-2.03, 20.4) * mm, "end": v(-1.29, 22.19) * mm});
            skLineSegment(sketch, "E21.3.2.4", {"start": v(-14.62, 19.65) * mm, "end": v(-3.83, 19.65) * mm});
            skArc(sketch, "E21.3.2.5", {"start": v(-17.16, 22.19) * mm, "mid": v(-16.42, 20.4) * mm, "end": v(-14.62, 19.65) * mm});
            skLineSegment(sketch, "E21.3.2.6", {"start": v(-17.16, 32.98) * mm, "end": v(-17.16, 22.19) * mm});
            skArc(sketch, "E21.3.2.7", {"start": v(-14.62, 35.52) * mm, "mid": v(-16.42, 34.78) * mm, "end": v(-17.16, 32.98) * mm});
            skLineSegment(sketch, "E21.3.3.0", {"start": v(-14.62, 17.1) * mm, "end": v(-3.83, 17.1) * mm});
            skArc(sketch, "E21.3.3.1", {"start": v(-1.29, 14.57) * mm, "mid": v(-2.03, 16.36) * mm, "end": v(-3.83, 17.1) * mm});
            skLineSegment(sketch, "E21.3.3.2", {"start": v(-1.29, 14.57) * mm, "end": v(-1.29, 3.77) * mm});
            skArc(sketch, "E21.3.3.3", {"start": v(-3.83, 1.23) * mm, "mid": v(-2.03, 1.98) * mm, "end": v(-1.29, 3.77) * mm});
            skLineSegment(sketch, "E21.3.3.4", {"start": v(-14.62, 1.23) * mm, "end": v(-3.83, 1.23) * mm});
            skArc(sketch, "E21.3.3.5", {"start": v(-17.16, 3.77) * mm, "mid": v(-16.42, 1.98) * mm, "end": v(-14.62, 1.23) * mm});
            skLineSegment(sketch, "E21.3.3.6", {"start": v(-17.16, 14.57) * mm, "end": v(-17.16, 3.77) * mm});
            skArc(sketch, "E21.3.3.7", {"start": v(-14.62, 17.1) * mm, "mid": v(-16.42, 16.36) * mm, "end": v(-17.16, 14.57) * mm});
            skLineSegment(sketch, "E21.3.4.0", {"start": v(-14.62, -1.3) * mm, "end": v(-3.83, -1.3) * mm});
            skArc(sketch, "E21.3.4.1", {"start": v(-1.29, -3.85) * mm, "mid": v(-2.03, -2.05) * mm, "end": v(-3.83, -1.3) * mm});
            skLineSegment(sketch, "E21.3.4.2", {"start": v(-1.29, -3.85) * mm, "end": v(-1.29, -14.64) * mm});
            skArc(sketch, "E21.3.4.3", {"start": v(-3.83, -17.18) * mm, "mid": v(-2.03, -16.44) * mm, "end": v(-1.29, -14.64) * mm});
            skLineSegment(sketch, "E21.3.4.4", {"start": v(-14.62, -17.18) * mm, "end": v(-3.83, -17.18) * mm});
            skArc(sketch, "E21.3.4.5", {"start": v(-17.16, -14.64) * mm, "mid": v(-16.42, -16.44) * mm, "end": v(-14.62, -17.18) * mm});
            skLineSegment(sketch, "E21.3.4.6", {"start": v(-17.16, -3.85) * mm, "end": v(-17.16, -14.64) * mm});
            skArc(sketch, "E21.3.4.7", {"start": v(-14.62, -1.3) * mm, "mid": v(-16.42, -2.05) * mm, "end": v(-17.16, -3.85) * mm});
            skLineSegment(sketch, "E21.3.5.0", {"start": v(-14.62, -19.72) * mm, "end": v(-3.83, -19.72) * mm});
            skArc(sketch, "E21.3.5.1", {"start": v(-1.29, -22.26) * mm, "mid": v(-2.03, -20.47) * mm, "end": v(-3.83, -19.72) * mm});
            skLineSegment(sketch, "E21.3.5.2", {"start": v(-1.29, -22.26) * mm, "end": v(-1.29, -33.06) * mm});
            skArc(sketch, "E21.3.5.3", {"start": v(-3.83, -35.6) * mm, "mid": v(-2.03, -34.85) * mm, "end": v(-1.29, -33.06) * mm});
            skLineSegment(sketch, "E21.3.5.4", {"start": v(-14.62, -35.6) * mm, "end": v(-3.83, -35.6) * mm});
            skArc(sketch, "E21.3.5.5", {"start": v(-17.16, -33.06) * mm, "mid": v(-16.42, -34.85) * mm, "end": v(-14.62, -35.6) * mm});
            skLineSegment(sketch, "E21.3.5.6", {"start": v(-17.16, -22.26) * mm, "end": v(-17.16, -33.06) * mm});
            skArc(sketch, "E21.3.5.7", {"start": v(-14.62, -19.72) * mm, "mid": v(-16.42, -20.47) * mm, "end": v(-17.16, -22.26) * mm});
            skLineSegment(sketch, "E21.3.6.0", {"start": v(-14.62, -38.14) * mm, "end": v(-3.83, -38.14) * mm});
            skArc(sketch, "E21.3.6.1", {"start": v(-1.29, -40.68) * mm, "mid": v(-2.03, -38.88) * mm, "end": v(-3.83, -38.14) * mm});
            skLineSegment(sketch, "E21.3.6.2", {"start": v(-1.29, -40.68) * mm, "end": v(-1.29, -51.47) * mm});
            skArc(sketch, "E21.3.6.3", {"start": v(-3.83, -54.01) * mm, "mid": v(-2.03, -53.27) * mm, "end": v(-1.29, -51.47) * mm});
            skLineSegment(sketch, "E21.3.6.4", {"start": v(-14.62, -54.01) * mm, "end": v(-3.83, -54.01) * mm});
            skArc(sketch, "E21.3.6.5", {"start": v(-17.16, -51.47) * mm, "mid": v(-16.42, -53.27) * mm, "end": v(-14.62, -54.01) * mm});
            skLineSegment(sketch, "E21.3.6.6", {"start": v(-17.16, -40.68) * mm, "end": v(-17.16, -51.47) * mm});
            skArc(sketch, "E21.3.6.7", {"start": v(-14.62, -38.14) * mm, "mid": v(-16.42, -38.88) * mm, "end": v(-17.16, -40.68) * mm});
            skLineSegment(sketch, "E21.3.7.0", {"start": v(-14.62, -56.55) * mm, "end": v(-3.83, -56.55) * mm});
            skArc(sketch, "E21.3.7.1", {"start": v(-1.29, -59.1) * mm, "mid": v(-2.03, -57.3) * mm, "end": v(-3.83, -56.55) * mm});
            skLineSegment(sketch, "E21.3.7.2", {"start": v(-1.29, -59.1) * mm, "end": v(-1.29, -69.89) * mm});
            skArc(sketch, "E21.3.7.3", {"start": v(-3.83, -72.43) * mm, "mid": v(-2.03, -71.68) * mm, "end": v(-1.29, -69.89) * mm});
            skLineSegment(sketch, "E21.3.7.4", {"start": v(-14.62, -72.43) * mm, "end": v(-3.83, -72.43) * mm});
            skArc(sketch, "E21.3.7.5", {"start": v(-17.16, -69.89) * mm, "mid": v(-16.42, -71.68) * mm, "end": v(-14.62, -72.43) * mm});
            skLineSegment(sketch, "E21.3.7.6", {"start": v(-17.16, -59.1) * mm, "end": v(-17.16, -69.89) * mm});
            skArc(sketch, "E21.3.7.7", {"start": v(-14.62, -56.55) * mm, "mid": v(-16.42, -57.3) * mm, "end": v(-17.16, -59.1) * mm});
            skLineSegment(sketch, "E21.4.0.0", {"start": v(3.8, 72.35) * mm, "end": v(14.59, 72.35) * mm});
            skArc(sketch, "E21.4.0.1", {"start": v(17.13, 69.81) * mm, "mid": v(16.38, 71.6) * mm, "end": v(14.59, 72.35) * mm});
            skLineSegment(sketch, "E21.4.0.2", {"start": v(17.13, 69.81) * mm, "end": v(17.13, 59.02) * mm});
            skArc(sketch, "E21.4.0.3", {"start": v(14.59, 56.48) * mm, "mid": v(16.38, 57.22) * mm, "end": v(17.13, 59.02) * mm});
            skLineSegment(sketch, "E21.4.0.4", {"start": v(3.8, 56.48) * mm, "end": v(14.59, 56.48) * mm});
            skArc(sketch, "E21.4.0.5", {"start": v(1.25, 59.02) * mm, "mid": v(2, 57.22) * mm, "end": v(3.8, 56.48) * mm});
            skLineSegment(sketch, "E21.4.0.6", {"start": v(1.25, 69.81) * mm, "end": v(1.25, 59.02) * mm});
            skArc(sketch, "E21.4.0.7", {"start": v(3.8, 72.35) * mm, "mid": v(2, 71.6) * mm, "end": v(1.25, 69.81) * mm});
            skLineSegment(sketch, "E21.4.1.0", {"start": v(3.8, 53.94) * mm, "end": v(14.59, 53.94) * mm});
            skArc(sketch, "E21.4.1.1", {"start": v(17.13, 51.4) * mm, "mid": v(16.38, 53.2) * mm, "end": v(14.59, 53.94) * mm});
            skLineSegment(sketch, "E21.4.1.2", {"start": v(17.13, 51.4) * mm, "end": v(17.13, 40.6) * mm});
            skArc(sketch, "E21.4.1.3", {"start": v(14.59, 38.06) * mm, "mid": v(16.38, 38.8) * mm, "end": v(17.13, 40.6) * mm});
            skLineSegment(sketch, "E21.4.1.4", {"start": v(3.8, 38.06) * mm, "end": v(14.59, 38.06) * mm});
            skArc(sketch, "E21.4.1.5", {"start": v(1.25, 40.6) * mm, "mid": v(2, 38.8) * mm, "end": v(3.8, 38.06) * mm});
            skLineSegment(sketch, "E21.4.1.6", {"start": v(1.25, 51.4) * mm, "end": v(1.25, 40.6) * mm});
            skArc(sketch, "E21.4.1.7", {"start": v(3.8, 53.94) * mm, "mid": v(2, 53.2) * mm, "end": v(1.25, 51.4) * mm});
            skLineSegment(sketch, "E21.4.2.0", {"start": v(3.8, 35.52) * mm, "end": v(14.59, 35.52) * mm});
            skArc(sketch, "E21.4.2.1", {"start": v(17.13, 32.98) * mm, "mid": v(16.38, 34.78) * mm, "end": v(14.59, 35.52) * mm});
            skLineSegment(sketch, "E21.4.2.2", {"start": v(17.13, 32.98) * mm, "end": v(17.13, 22.19) * mm});
            skArc(sketch, "E21.4.2.3", {"start": v(14.59, 19.65) * mm, "mid": v(16.38, 20.4) * mm, "end": v(17.13, 22.19) * mm});
            skLineSegment(sketch, "E21.4.2.4", {"start": v(3.8, 19.65) * mm, "end": v(14.59, 19.65) * mm});
            skArc(sketch, "E21.4.2.5", {"start": v(1.25, 22.19) * mm, "mid": v(2, 20.4) * mm, "end": v(3.8, 19.65) * mm});
            skLineSegment(sketch, "E21.4.2.6", {"start": v(1.25, 32.98) * mm, "end": v(1.25, 22.19) * mm});
            skArc(sketch, "E21.4.2.7", {"start": v(3.8, 35.52) * mm, "mid": v(2, 34.78) * mm, "end": v(1.25, 32.98) * mm});
            skLineSegment(sketch, "E21.4.3.0", {"start": v(3.8, 17.1) * mm, "end": v(14.59, 17.1) * mm});
            skArc(sketch, "E21.4.3.1", {"start": v(17.13, 14.57) * mm, "mid": v(16.38, 16.36) * mm, "end": v(14.59, 17.1) * mm});
            skLineSegment(sketch, "E21.4.3.2", {"start": v(17.13, 14.57) * mm, "end": v(17.13, 3.77) * mm});
            skArc(sketch, "E21.4.3.3", {"start": v(14.59, 1.23) * mm, "mid": v(16.38, 1.98) * mm, "end": v(17.13, 3.77) * mm});
            skLineSegment(sketch, "E21.4.3.4", {"start": v(3.8, 1.23) * mm, "end": v(14.59, 1.23) * mm});
            skArc(sketch, "E21.4.3.5", {"start": v(1.25, 3.77) * mm, "mid": v(2, 1.98) * mm, "end": v(3.8, 1.23) * mm});
            skLineSegment(sketch, "E21.4.3.6", {"start": v(1.25, 14.57) * mm, "end": v(1.25, 3.77) * mm});
            skArc(sketch, "E21.4.3.7", {"start": v(3.8, 17.1) * mm, "mid": v(2, 16.36) * mm, "end": v(1.25, 14.57) * mm});
            skLineSegment(sketch, "E21.4.4.0", {"start": v(3.8, -1.3) * mm, "end": v(14.59, -1.3) * mm});
            skArc(sketch, "E21.4.4.1", {"start": v(17.13, -3.85) * mm, "mid": v(16.38, -2.05) * mm, "end": v(14.59, -1.3) * mm});
            skLineSegment(sketch, "E21.4.4.2", {"start": v(17.13, -3.85) * mm, "end": v(17.13, -14.64) * mm});
            skArc(sketch, "E21.4.4.3", {"start": v(14.59, -17.18) * mm, "mid": v(16.38, -16.44) * mm, "end": v(17.13, -14.64) * mm});
            skLineSegment(sketch, "E21.4.4.4", {"start": v(3.8, -17.18) * mm, "end": v(14.59, -17.18) * mm});
            skArc(sketch, "E21.4.4.5", {"start": v(1.25, -14.64) * mm, "mid": v(2, -16.44) * mm, "end": v(3.8, -17.18) * mm});
            skLineSegment(sketch, "E21.4.4.6", {"start": v(1.25, -3.85) * mm, "end": v(1.25, -14.64) * mm});
            skArc(sketch, "E21.4.4.7", {"start": v(3.8, -1.3) * mm, "mid": v(2, -2.05) * mm, "end": v(1.25, -3.85) * mm});
            skLineSegment(sketch, "E21.4.5.0", {"start": v(3.8, -19.72) * mm, "end": v(14.59, -19.72) * mm});
            skArc(sketch, "E21.4.5.1", {"start": v(17.13, -22.26) * mm, "mid": v(16.38, -20.47) * mm, "end": v(14.59, -19.72) * mm});
            skLineSegment(sketch, "E21.4.5.2", {"start": v(17.13, -22.26) * mm, "end": v(17.13, -33.06) * mm});
            skArc(sketch, "E21.4.5.3", {"start": v(14.59, -35.6) * mm, "mid": v(16.38, -34.85) * mm, "end": v(17.13, -33.06) * mm});
            skLineSegment(sketch, "E21.4.5.4", {"start": v(3.8, -35.6) * mm, "end": v(14.59, -35.6) * mm});
            skArc(sketch, "E21.4.5.5", {"start": v(1.25, -33.06) * mm, "mid": v(2, -34.85) * mm, "end": v(3.8, -35.6) * mm});
            skLineSegment(sketch, "E21.4.5.6", {"start": v(1.25, -22.26) * mm, "end": v(1.25, -33.06) * mm});
            skArc(sketch, "E21.4.5.7", {"start": v(3.8, -19.72) * mm, "mid": v(2, -20.47) * mm, "end": v(1.25, -22.26) * mm});
            skLineSegment(sketch, "E21.4.6.0", {"start": v(3.8, -38.14) * mm, "end": v(14.59, -38.14) * mm});
            skArc(sketch, "E21.4.6.1", {"start": v(17.13, -40.68) * mm, "mid": v(16.38, -38.88) * mm, "end": v(14.59, -38.14) * mm});
            skLineSegment(sketch, "E21.4.6.2", {"start": v(17.13, -40.68) * mm, "end": v(17.13, -51.47) * mm});
            skArc(sketch, "E21.4.6.3", {"start": v(14.59, -54.01) * mm, "mid": v(16.38, -53.27) * mm, "end": v(17.13, -51.47) * mm});
            skLineSegment(sketch, "E21.4.6.4", {"start": v(3.8, -54.01) * mm, "end": v(14.59, -54.01) * mm});
            skArc(sketch, "E21.4.6.5", {"start": v(1.25, -51.47) * mm, "mid": v(2, -53.27) * mm, "end": v(3.8, -54.01) * mm});
            skLineSegment(sketch, "E21.4.6.6", {"start": v(1.25, -40.68) * mm, "end": v(1.25, -51.47) * mm});
            skArc(sketch, "E21.4.6.7", {"start": v(3.8, -38.14) * mm, "mid": v(2, -38.88) * mm, "end": v(1.25, -40.68) * mm});
            skLineSegment(sketch, "E21.4.7.0", {"start": v(3.8, -56.55) * mm, "end": v(14.59, -56.55) * mm});
            skArc(sketch, "E21.4.7.1", {"start": v(17.13, -59.1) * mm, "mid": v(16.38, -57.3) * mm, "end": v(14.59, -56.55) * mm});
            skLineSegment(sketch, "E21.4.7.2", {"start": v(17.13, -59.1) * mm, "end": v(17.13, -69.89) * mm});
            skArc(sketch, "E21.4.7.3", {"start": v(14.59, -72.43) * mm, "mid": v(16.38, -71.68) * mm, "end": v(17.13, -69.89) * mm});
            skLineSegment(sketch, "E21.4.7.4", {"start": v(3.8, -72.43) * mm, "end": v(14.59, -72.43) * mm});
            skArc(sketch, "E21.4.7.5", {"start": v(1.25, -69.89) * mm, "mid": v(2, -71.68) * mm, "end": v(3.8, -72.43) * mm});
            skLineSegment(sketch, "E21.4.7.6", {"start": v(1.25, -59.1) * mm, "end": v(1.25, -69.89) * mm});
            skArc(sketch, "E21.4.7.7", {"start": v(3.8, -56.55) * mm, "mid": v(2, -57.3) * mm, "end": v(1.25, -59.1) * mm});
            skLineSegment(sketch, "E21.5.0.0", {"start": v(22.2, 72.35) * mm, "end": v(33, 72.35) * mm});
            skArc(sketch, "E21.5.0.1", {"start": v(35.54, 69.81) * mm, "mid": v(34.8, 71.6) * mm, "end": v(33, 72.35) * mm});
            skLineSegment(sketch, "E21.5.0.2", {"start": v(35.54, 69.81) * mm, "end": v(35.54, 59.02) * mm});
            skArc(sketch, "E21.5.0.3", {"start": v(33, 56.48) * mm, "mid": v(34.8, 57.22) * mm, "end": v(35.54, 59.02) * mm});
            skLineSegment(sketch, "E21.5.0.4", {"start": v(22.2, 56.48) * mm, "end": v(33, 56.48) * mm});
            skArc(sketch, "E21.5.0.5", {"start": v(19.67, 59.02) * mm, "mid": v(20.41, 57.22) * mm, "end": v(22.2, 56.48) * mm});
            skLineSegment(sketch, "E21.5.0.6", {"start": v(19.67, 69.81) * mm, "end": v(19.67, 59.02) * mm});
            skArc(sketch, "E21.5.0.7", {"start": v(22.2, 72.35) * mm, "mid": v(20.41, 71.6) * mm, "end": v(19.67, 69.81) * mm});
            skLineSegment(sketch, "E21.5.1.0", {"start": v(22.2, 53.94) * mm, "end": v(33, 53.94) * mm});
            skArc(sketch, "E21.5.1.1", {"start": v(35.54, 51.4) * mm, "mid": v(34.8, 53.2) * mm, "end": v(33, 53.94) * mm});
            skLineSegment(sketch, "E21.5.1.2", {"start": v(35.54, 51.4) * mm, "end": v(35.54, 40.6) * mm});
            skArc(sketch, "E21.5.1.3", {"start": v(33, 38.06) * mm, "mid": v(34.8, 38.8) * mm, "end": v(35.54, 40.6) * mm});
            skLineSegment(sketch, "E21.5.1.4", {"start": v(22.2, 38.06) * mm, "end": v(33, 38.06) * mm});
            skArc(sketch, "E21.5.1.5", {"start": v(19.67, 40.6) * mm, "mid": v(20.41, 38.8) * mm, "end": v(22.2, 38.06) * mm});
            skLineSegment(sketch, "E21.5.1.6", {"start": v(19.67, 51.4) * mm, "end": v(19.67, 40.6) * mm});
            skArc(sketch, "E21.5.1.7", {"start": v(22.2, 53.94) * mm, "mid": v(20.41, 53.2) * mm, "end": v(19.67, 51.4) * mm});
            skLineSegment(sketch, "E21.5.2.0", {"start": v(22.2, 35.52) * mm, "end": v(33, 35.52) * mm});
            skArc(sketch, "E21.5.2.1", {"start": v(35.54, 32.98) * mm, "mid": v(34.8, 34.78) * mm, "end": v(33, 35.52) * mm});
            skLineSegment(sketch, "E21.5.2.2", {"start": v(35.54, 32.98) * mm, "end": v(35.54, 22.19) * mm});
            skArc(sketch, "E21.5.2.3", {"start": v(33, 19.65) * mm, "mid": v(34.8, 20.4) * mm, "end": v(35.54, 22.19) * mm});
            skLineSegment(sketch, "E21.5.2.4", {"start": v(22.2, 19.65) * mm, "end": v(33, 19.65) * mm});
            skArc(sketch, "E21.5.2.5", {"start": v(19.67, 22.19) * mm, "mid": v(20.41, 20.4) * mm, "end": v(22.2, 19.65) * mm});
            skLineSegment(sketch, "E21.5.2.6", {"start": v(19.67, 32.98) * mm, "end": v(19.67, 22.19) * mm});
            skArc(sketch, "E21.5.2.7", {"start": v(22.2, 35.52) * mm, "mid": v(20.41, 34.78) * mm, "end": v(19.67, 32.98) * mm});
            skLineSegment(sketch, "E21.5.3.0", {"start": v(22.2, 17.1) * mm, "end": v(33, 17.1) * mm});
            skArc(sketch, "E21.5.3.1", {"start": v(35.54, 14.57) * mm, "mid": v(34.8, 16.36) * mm, "end": v(33, 17.1) * mm});
            skLineSegment(sketch, "E21.5.3.2", {"start": v(35.54, 14.57) * mm, "end": v(35.54, 3.77) * mm});
            skArc(sketch, "E21.5.3.3", {"start": v(33, 1.23) * mm, "mid": v(34.8, 1.98) * mm, "end": v(35.54, 3.77) * mm});
            skLineSegment(sketch, "E21.5.3.4", {"start": v(22.2, 1.23) * mm, "end": v(33, 1.23) * mm});
            skArc(sketch, "E21.5.3.5", {"start": v(19.67, 3.77) * mm, "mid": v(20.41, 1.98) * mm, "end": v(22.2, 1.23) * mm});
            skLineSegment(sketch, "E21.5.3.6", {"start": v(19.67, 14.57) * mm, "end": v(19.67, 3.77) * mm});
            skArc(sketch, "E21.5.3.7", {"start": v(22.2, 17.1) * mm, "mid": v(20.41, 16.36) * mm, "end": v(19.67, 14.57) * mm});
            skLineSegment(sketch, "E21.5.4.0", {"start": v(22.2, -1.3) * mm, "end": v(33, -1.3) * mm});
            skArc(sketch, "E21.5.4.1", {"start": v(35.54, -3.85) * mm, "mid": v(34.8, -2.05) * mm, "end": v(33, -1.3) * mm});
            skLineSegment(sketch, "E21.5.4.2", {"start": v(35.54, -3.85) * mm, "end": v(35.54, -14.64) * mm});
            skArc(sketch, "E21.5.4.3", {"start": v(33, -17.18) * mm, "mid": v(34.8, -16.44) * mm, "end": v(35.54, -14.64) * mm});
            skLineSegment(sketch, "E21.5.4.4", {"start": v(22.2, -17.18) * mm, "end": v(33, -17.18) * mm});
            skArc(sketch, "E21.5.4.5", {"start": v(19.67, -14.64) * mm, "mid": v(20.41, -16.44) * mm, "end": v(22.2, -17.18) * mm});
            skLineSegment(sketch, "E21.5.4.6", {"start": v(19.67, -3.85) * mm, "end": v(19.67, -14.64) * mm});
            skArc(sketch, "E21.5.4.7", {"start": v(22.2, -1.3) * mm, "mid": v(20.41, -2.05) * mm, "end": v(19.67, -3.85) * mm});
            skLineSegment(sketch, "E21.5.5.0", {"start": v(22.2, -19.72) * mm, "end": v(33, -19.72) * mm});
            skArc(sketch, "E21.5.5.1", {"start": v(35.54, -22.26) * mm, "mid": v(34.8, -20.47) * mm, "end": v(33, -19.72) * mm});
            skLineSegment(sketch, "E21.5.5.2", {"start": v(35.54, -22.26) * mm, "end": v(35.54, -33.06) * mm});
            skArc(sketch, "E21.5.5.3", {"start": v(33, -35.6) * mm, "mid": v(34.8, -34.85) * mm, "end": v(35.54, -33.06) * mm});
            skLineSegment(sketch, "E21.5.5.4", {"start": v(22.2, -35.6) * mm, "end": v(33, -35.6) * mm});
            skArc(sketch, "E21.5.5.5", {"start": v(19.67, -33.06) * mm, "mid": v(20.41, -34.85) * mm, "end": v(22.2, -35.6) * mm});
            skLineSegment(sketch, "E21.5.5.6", {"start": v(19.67, -22.26) * mm, "end": v(19.67, -33.06) * mm});
            skArc(sketch, "E21.5.5.7", {"start": v(22.2, -19.72) * mm, "mid": v(20.41, -20.47) * mm, "end": v(19.67, -22.26) * mm});
            skLineSegment(sketch, "E21.5.6.0", {"start": v(22.2, -38.14) * mm, "end": v(33, -38.14) * mm});
            skArc(sketch, "E21.5.6.1", {"start": v(35.54, -40.68) * mm, "mid": v(34.8, -38.88) * mm, "end": v(33, -38.14) * mm});
            skLineSegment(sketch, "E21.5.6.2", {"start": v(35.54, -40.68) * mm, "end": v(35.54, -51.47) * mm});
            skArc(sketch, "E21.5.6.3", {"start": v(33, -54.01) * mm, "mid": v(34.8, -53.27) * mm, "end": v(35.54, -51.47) * mm});
            skLineSegment(sketch, "E21.5.6.4", {"start": v(22.2, -54.01) * mm, "end": v(33, -54.01) * mm});
            skArc(sketch, "E21.5.6.5", {"start": v(19.67, -51.47) * mm, "mid": v(20.41, -53.27) * mm, "end": v(22.2, -54.01) * mm});
            skLineSegment(sketch, "E21.5.6.6", {"start": v(19.67, -40.68) * mm, "end": v(19.67, -51.47) * mm});
            skArc(sketch, "E21.5.6.7", {"start": v(22.2, -38.14) * mm, "mid": v(20.41, -38.88) * mm, "end": v(19.67, -40.68) * mm});
            skLineSegment(sketch, "E21.5.7.0", {"start": v(22.2, -56.55) * mm, "end": v(33, -56.55) * mm});
            skArc(sketch, "E21.5.7.1", {"start": v(35.54, -59.1) * mm, "mid": v(34.8, -57.3) * mm, "end": v(33, -56.55) * mm});
            skLineSegment(sketch, "E21.5.7.2", {"start": v(35.54, -59.1) * mm, "end": v(35.54, -69.89) * mm});
            skArc(sketch, "E21.5.7.3", {"start": v(33, -72.43) * mm, "mid": v(34.8, -71.68) * mm, "end": v(35.54, -69.89) * mm});
            skLineSegment(sketch, "E21.5.7.4", {"start": v(22.2, -72.43) * mm, "end": v(33, -72.43) * mm});
            skArc(sketch, "E21.5.7.5", {"start": v(19.67, -69.89) * mm, "mid": v(20.41, -71.68) * mm, "end": v(22.2, -72.43) * mm});
            skLineSegment(sketch, "E21.5.7.6", {"start": v(19.67, -59.1) * mm, "end": v(19.67, -69.89) * mm});
            skArc(sketch, "E21.5.7.7", {"start": v(22.2, -56.55) * mm, "mid": v(20.41, -57.3) * mm, "end": v(19.67, -59.1) * mm});
            skLineSegment(sketch, "E21.6.0.0", {"start": v(40.62, 72.35) * mm, "end": v(51.42, 72.35) * mm});
            skArc(sketch, "E21.6.0.1", {"start": v(53.96, 69.81) * mm, "mid": v(53.21, 71.6) * mm, "end": v(51.42, 72.35) * mm});
            skLineSegment(sketch, "E21.6.0.2", {"start": v(53.96, 69.81) * mm, "end": v(53.96, 59.02) * mm});
            skArc(sketch, "E21.6.0.3", {"start": v(51.42, 56.48) * mm, "mid": v(53.21, 57.22) * mm, "end": v(53.96, 59.02) * mm});
            skLineSegment(sketch, "E21.6.0.4", {"start": v(40.62, 56.48) * mm, "end": v(51.42, 56.48) * mm});
            skArc(sketch, "E21.6.0.5", {"start": v(38.08, 59.02) * mm, "mid": v(38.83, 57.22) * mm, "end": v(40.62, 56.48) * mm});
            skLineSegment(sketch, "E21.6.0.6", {"start": v(38.08, 69.81) * mm, "end": v(38.08, 59.02) * mm});
            skArc(sketch, "E21.6.0.7", {"start": v(40.62, 72.35) * mm, "mid": v(38.83, 71.6) * mm, "end": v(38.08, 69.81) * mm});
            skLineSegment(sketch, "E21.6.1.0", {"start": v(40.62, 53.94) * mm, "end": v(51.42, 53.94) * mm});
            skArc(sketch, "E21.6.1.1", {"start": v(53.96, 51.4) * mm, "mid": v(53.21, 53.2) * mm, "end": v(51.42, 53.94) * mm});
            skLineSegment(sketch, "E21.6.1.2", {"start": v(53.96, 51.4) * mm, "end": v(53.96, 40.6) * mm});
            skArc(sketch, "E21.6.1.3", {"start": v(51.42, 38.06) * mm, "mid": v(53.21, 38.8) * mm, "end": v(53.96, 40.6) * mm});
            skLineSegment(sketch, "E21.6.1.4", {"start": v(40.62, 38.06) * mm, "end": v(51.42, 38.06) * mm});
            skArc(sketch, "E21.6.1.5", {"start": v(38.08, 40.6) * mm, "mid": v(38.83, 38.8) * mm, "end": v(40.62, 38.06) * mm});
            skLineSegment(sketch, "E21.6.1.6", {"start": v(38.08, 51.4) * mm, "end": v(38.08, 40.6) * mm});
            skArc(sketch, "E21.6.1.7", {"start": v(40.62, 53.94) * mm, "mid": v(38.83, 53.2) * mm, "end": v(38.08, 51.4) * mm});
            skLineSegment(sketch, "E21.6.2.0", {"start": v(40.62, 35.52) * mm, "end": v(51.42, 35.52) * mm});
            skArc(sketch, "E21.6.2.1", {"start": v(53.96, 32.98) * mm, "mid": v(53.21, 34.78) * mm, "end": v(51.42, 35.52) * mm});
            skLineSegment(sketch, "E21.6.2.2", {"start": v(53.96, 32.98) * mm, "end": v(53.96, 22.19) * mm});
            skArc(sketch, "E21.6.2.3", {"start": v(51.42, 19.65) * mm, "mid": v(53.21, 20.4) * mm, "end": v(53.96, 22.19) * mm});
            skLineSegment(sketch, "E21.6.2.4", {"start": v(40.62, 19.65) * mm, "end": v(51.42, 19.65) * mm});
            skArc(sketch, "E21.6.2.5", {"start": v(38.08, 22.19) * mm, "mid": v(38.83, 20.4) * mm, "end": v(40.62, 19.65) * mm});
            skLineSegment(sketch, "E21.6.2.6", {"start": v(38.08, 32.98) * mm, "end": v(38.08, 22.19) * mm});
            skArc(sketch, "E21.6.2.7", {"start": v(40.62, 35.52) * mm, "mid": v(38.83, 34.78) * mm, "end": v(38.08, 32.98) * mm});
            skLineSegment(sketch, "E21.6.3.0", {"start": v(40.62, 17.1) * mm, "end": v(51.42, 17.1) * mm});
            skArc(sketch, "E21.6.3.1", {"start": v(53.96, 14.57) * mm, "mid": v(53.21, 16.36) * mm, "end": v(51.42, 17.1) * mm});
            skLineSegment(sketch, "E21.6.3.2", {"start": v(53.96, 14.57) * mm, "end": v(53.96, 3.77) * mm});
            skArc(sketch, "E21.6.3.3", {"start": v(51.42, 1.23) * mm, "mid": v(53.21, 1.98) * mm, "end": v(53.96, 3.77) * mm});
            skLineSegment(sketch, "E21.6.3.4", {"start": v(40.62, 1.23) * mm, "end": v(51.42, 1.23) * mm});
            skArc(sketch, "E21.6.3.5", {"start": v(38.08, 3.77) * mm, "mid": v(38.83, 1.98) * mm, "end": v(40.62, 1.23) * mm});
            skLineSegment(sketch, "E21.6.3.6", {"start": v(38.08, 14.57) * mm, "end": v(38.08, 3.77) * mm});
            skArc(sketch, "E21.6.3.7", {"start": v(40.62, 17.1) * mm, "mid": v(38.83, 16.36) * mm, "end": v(38.08, 14.57) * mm});
            skLineSegment(sketch, "E21.6.4.0", {"start": v(40.62, -1.3) * mm, "end": v(51.42, -1.3) * mm});
            skArc(sketch, "E21.6.4.1", {"start": v(53.96, -3.85) * mm, "mid": v(53.21, -2.05) * mm, "end": v(51.42, -1.3) * mm});
            skLineSegment(sketch, "E21.6.4.2", {"start": v(53.96, -3.85) * mm, "end": v(53.96, -14.64) * mm});
            skArc(sketch, "E21.6.4.3", {"start": v(51.42, -17.18) * mm, "mid": v(53.21, -16.44) * mm, "end": v(53.96, -14.64) * mm});
            skLineSegment(sketch, "E21.6.4.4", {"start": v(40.62, -17.18) * mm, "end": v(51.42, -17.18) * mm});
            skArc(sketch, "E21.6.4.5", {"start": v(38.08, -14.64) * mm, "mid": v(38.83, -16.44) * mm, "end": v(40.62, -17.18) * mm});
            skLineSegment(sketch, "E21.6.4.6", {"start": v(38.08, -3.85) * mm, "end": v(38.08, -14.64) * mm});
            skArc(sketch, "E21.6.4.7", {"start": v(40.62, -1.3) * mm, "mid": v(38.83, -2.05) * mm, "end": v(38.08, -3.85) * mm});
            skLineSegment(sketch, "E21.6.5.0", {"start": v(40.62, -19.72) * mm, "end": v(51.42, -19.72) * mm});
            skArc(sketch, "E21.6.5.1", {"start": v(53.96, -22.26) * mm, "mid": v(53.21, -20.47) * mm, "end": v(51.42, -19.72) * mm});
            skLineSegment(sketch, "E21.6.5.2", {"start": v(53.96, -22.26) * mm, "end": v(53.96, -33.06) * mm});
            skArc(sketch, "E21.6.5.3", {"start": v(51.42, -35.6) * mm, "mid": v(53.21, -34.85) * mm, "end": v(53.96, -33.06) * mm});
            skLineSegment(sketch, "E21.6.5.4", {"start": v(40.62, -35.6) * mm, "end": v(51.42, -35.6) * mm});
            skArc(sketch, "E21.6.5.5", {"start": v(38.08, -33.06) * mm, "mid": v(38.83, -34.85) * mm, "end": v(40.62, -35.6) * mm});
            skLineSegment(sketch, "E21.6.5.6", {"start": v(38.08, -22.26) * mm, "end": v(38.08, -33.06) * mm});
            skArc(sketch, "E21.6.5.7", {"start": v(40.62, -19.72) * mm, "mid": v(38.83, -20.47) * mm, "end": v(38.08, -22.26) * mm});
            skLineSegment(sketch, "E21.6.6.0", {"start": v(40.62, -38.14) * mm, "end": v(51.42, -38.14) * mm});
            skArc(sketch, "E21.6.6.1", {"start": v(53.96, -40.68) * mm, "mid": v(53.21, -38.88) * mm, "end": v(51.42, -38.14) * mm});
            skLineSegment(sketch, "E21.6.6.2", {"start": v(53.96, -40.68) * mm, "end": v(53.96, -51.47) * mm});
            skArc(sketch, "E21.6.6.3", {"start": v(51.42, -54.01) * mm, "mid": v(53.21, -53.27) * mm, "end": v(53.96, -51.47) * mm});
            skLineSegment(sketch, "E21.6.6.4", {"start": v(40.62, -54.01) * mm, "end": v(51.42, -54.01) * mm});
            skArc(sketch, "E21.6.6.5", {"start": v(38.08, -51.47) * mm, "mid": v(38.83, -53.27) * mm, "end": v(40.62, -54.01) * mm});
            skLineSegment(sketch, "E21.6.6.6", {"start": v(38.08, -40.68) * mm, "end": v(38.08, -51.47) * mm});
            skArc(sketch, "E21.6.6.7", {"start": v(40.62, -38.14) * mm, "mid": v(38.83, -38.88) * mm, "end": v(38.08, -40.68) * mm});
            skLineSegment(sketch, "E21.6.7.0", {"start": v(40.62, -56.55) * mm, "end": v(51.42, -56.55) * mm});
            skArc(sketch, "E21.6.7.1", {"start": v(53.96, -59.1) * mm, "mid": v(53.21, -57.3) * mm, "end": v(51.42, -56.55) * mm});
            skLineSegment(sketch, "E21.6.7.2", {"start": v(53.96, -59.1) * mm, "end": v(53.96, -69.89) * mm});
            skArc(sketch, "E21.6.7.3", {"start": v(51.42, -72.43) * mm, "mid": v(53.21, -71.68) * mm, "end": v(53.96, -69.89) * mm});
            skLineSegment(sketch, "E21.6.7.4", {"start": v(40.62, -72.43) * mm, "end": v(51.42, -72.43) * mm});
            skArc(sketch, "E21.6.7.5", {"start": v(38.08, -69.89) * mm, "mid": v(38.83, -71.68) * mm, "end": v(40.62, -72.43) * mm});
            skLineSegment(sketch, "E21.6.7.6", {"start": v(38.08, -59.1) * mm, "end": v(38.08, -69.89) * mm});
            skArc(sketch, "E21.6.7.7", {"start": v(40.62, -56.55) * mm, "mid": v(38.83, -57.3) * mm, "end": v(38.08, -59.1) * mm});
            skLineSegment(sketch, "E21.7.0.0", {"start": v(59.04, 72.35) * mm, "end": v(69.83, 72.35) * mm});
            skArc(sketch, "E21.7.0.1", {"start": v(72.37, 69.81) * mm, "mid": v(71.63, 71.6) * mm, "end": v(69.83, 72.35) * mm});
            skLineSegment(sketch, "E21.7.0.2", {"start": v(72.37, 69.81) * mm, "end": v(72.37, 59.02) * mm});
            skArc(sketch, "E21.7.0.3", {"start": v(69.83, 56.48) * mm, "mid": v(71.63, 57.22) * mm, "end": v(72.37, 59.02) * mm});
            skLineSegment(sketch, "E21.7.0.4", {"start": v(59.04, 56.48) * mm, "end": v(69.83, 56.48) * mm});
            skArc(sketch, "E21.7.0.5", {"start": v(56.5, 59.02) * mm, "mid": v(57.24, 57.22) * mm, "end": v(59.04, 56.48) * mm});
            skLineSegment(sketch, "E21.7.0.6", {"start": v(56.5, 69.81) * mm, "end": v(56.5, 59.02) * mm});
            skArc(sketch, "E21.7.0.7", {"start": v(59.04, 72.35) * mm, "mid": v(57.24, 71.6) * mm, "end": v(56.5, 69.81) * mm});
            skLineSegment(sketch, "E21.7.1.0", {"start": v(59.04, 53.94) * mm, "end": v(69.83, 53.94) * mm});
            skArc(sketch, "E21.7.1.1", {"start": v(72.37, 51.4) * mm, "mid": v(71.63, 53.2) * mm, "end": v(69.83, 53.94) * mm});
            skLineSegment(sketch, "E21.7.1.2", {"start": v(72.37, 51.4) * mm, "end": v(72.37, 40.6) * mm});
            skArc(sketch, "E21.7.1.3", {"start": v(69.83, 38.06) * mm, "mid": v(71.63, 38.8) * mm, "end": v(72.37, 40.6) * mm});
            skLineSegment(sketch, "E21.7.1.4", {"start": v(59.04, 38.06) * mm, "end": v(69.83, 38.06) * mm});
            skArc(sketch, "E21.7.1.5", {"start": v(56.5, 40.6) * mm, "mid": v(57.24, 38.8) * mm, "end": v(59.04, 38.06) * mm});
            skLineSegment(sketch, "E21.7.1.6", {"start": v(56.5, 51.4) * mm, "end": v(56.5, 40.6) * mm});
            skArc(sketch, "E21.7.1.7", {"start": v(59.04, 53.94) * mm, "mid": v(57.24, 53.2) * mm, "end": v(56.5, 51.4) * mm});
            skLineSegment(sketch, "E21.7.2.0", {"start": v(59.04, 35.52) * mm, "end": v(69.83, 35.52) * mm});
            skArc(sketch, "E21.7.2.1", {"start": v(72.37, 32.98) * mm, "mid": v(71.63, 34.78) * mm, "end": v(69.83, 35.52) * mm});
            skLineSegment(sketch, "E21.7.2.2", {"start": v(72.37, 32.98) * mm, "end": v(72.37, 22.19) * mm});
            skArc(sketch, "E21.7.2.3", {"start": v(69.83, 19.65) * mm, "mid": v(71.63, 20.4) * mm, "end": v(72.37, 22.19) * mm});
            skLineSegment(sketch, "E21.7.2.4", {"start": v(59.04, 19.65) * mm, "end": v(69.83, 19.65) * mm});
            skArc(sketch, "E21.7.2.5", {"start": v(56.5, 22.19) * mm, "mid": v(57.24, 20.4) * mm, "end": v(59.04, 19.65) * mm});
            skLineSegment(sketch, "E21.7.2.6", {"start": v(56.5, 32.98) * mm, "end": v(56.5, 22.19) * mm});
            skArc(sketch, "E21.7.2.7", {"start": v(59.04, 35.52) * mm, "mid": v(57.24, 34.78) * mm, "end": v(56.5, 32.98) * mm});
            skLineSegment(sketch, "E21.7.3.0", {"start": v(59.04, 17.1) * mm, "end": v(69.83, 17.1) * mm});
            skArc(sketch, "E21.7.3.1", {"start": v(72.37, 14.57) * mm, "mid": v(71.63, 16.36) * mm, "end": v(69.83, 17.1) * mm});
            skLineSegment(sketch, "E21.7.3.2", {"start": v(72.37, 14.57) * mm, "end": v(72.37, 3.77) * mm});
            skArc(sketch, "E21.7.3.3", {"start": v(69.83, 1.23) * mm, "mid": v(71.63, 1.98) * mm, "end": v(72.37, 3.77) * mm});
            skLineSegment(sketch, "E21.7.3.4", {"start": v(59.04, 1.23) * mm, "end": v(69.83, 1.23) * mm});
            skArc(sketch, "E21.7.3.5", {"start": v(56.5, 3.77) * mm, "mid": v(57.24, 1.98) * mm, "end": v(59.04, 1.23) * mm});
            skLineSegment(sketch, "E21.7.3.6", {"start": v(56.5, 14.57) * mm, "end": v(56.5, 3.77) * mm});
            skArc(sketch, "E21.7.3.7", {"start": v(59.04, 17.1) * mm, "mid": v(57.24, 16.36) * mm, "end": v(56.5, 14.57) * mm});
            skLineSegment(sketch, "E21.7.4.0", {"start": v(59.04, -1.3) * mm, "end": v(69.83, -1.3) * mm});
            skArc(sketch, "E21.7.4.1", {"start": v(72.37, -3.85) * mm, "mid": v(71.63, -2.05) * mm, "end": v(69.83, -1.3) * mm});
            skLineSegment(sketch, "E21.7.4.2", {"start": v(72.37, -3.85) * mm, "end": v(72.37, -14.64) * mm});
            skArc(sketch, "E21.7.4.3", {"start": v(69.83, -17.18) * mm, "mid": v(71.63, -16.44) * mm, "end": v(72.37, -14.64) * mm});
            skLineSegment(sketch, "E21.7.4.4", {"start": v(59.04, -17.18) * mm, "end": v(69.83, -17.18) * mm});
            skArc(sketch, "E21.7.4.5", {"start": v(56.5, -14.64) * mm, "mid": v(57.24, -16.44) * mm, "end": v(59.04, -17.18) * mm});
            skLineSegment(sketch, "E21.7.4.6", {"start": v(56.5, -3.85) * mm, "end": v(56.5, -14.64) * mm});
            skArc(sketch, "E21.7.4.7", {"start": v(59.04, -1.3) * mm, "mid": v(57.24, -2.05) * mm, "end": v(56.5, -3.85) * mm});
            skLineSegment(sketch, "E21.7.5.0", {"start": v(59.04, -19.72) * mm, "end": v(69.83, -19.72) * mm});
            skArc(sketch, "E21.7.5.1", {"start": v(72.37, -22.26) * mm, "mid": v(71.63, -20.47) * mm, "end": v(69.83, -19.72) * mm});
            skLineSegment(sketch, "E21.7.5.2", {"start": v(72.37, -22.26) * mm, "end": v(72.37, -33.06) * mm});
            skArc(sketch, "E21.7.5.3", {"start": v(69.83, -35.6) * mm, "mid": v(71.63, -34.85) * mm, "end": v(72.37, -33.06) * mm});
            skLineSegment(sketch, "E21.7.5.4", {"start": v(59.04, -35.6) * mm, "end": v(69.83, -35.6) * mm});
            skArc(sketch, "E21.7.5.5", {"start": v(56.5, -33.06) * mm, "mid": v(57.24, -34.85) * mm, "end": v(59.04, -35.6) * mm});
            skLineSegment(sketch, "E21.7.5.6", {"start": v(56.5, -22.26) * mm, "end": v(56.5, -33.06) * mm});
            skArc(sketch, "E21.7.5.7", {"start": v(59.04, -19.72) * mm, "mid": v(57.24, -20.47) * mm, "end": v(56.5, -22.26) * mm});
            skLineSegment(sketch, "E21.7.6.0", {"start": v(59.04, -38.14) * mm, "end": v(69.83, -38.14) * mm});
            skArc(sketch, "E21.7.6.1", {"start": v(72.37, -40.68) * mm, "mid": v(71.63, -38.88) * mm, "end": v(69.83, -38.14) * mm});
            skLineSegment(sketch, "E21.7.6.2", {"start": v(72.37, -40.68) * mm, "end": v(72.37, -51.47) * mm});
            skArc(sketch, "E21.7.6.3", {"start": v(69.83, -54.01) * mm, "mid": v(71.63, -53.27) * mm, "end": v(72.37, -51.47) * mm});
            skLineSegment(sketch, "E21.7.6.4", {"start": v(59.04, -54.01) * mm, "end": v(69.83, -54.01) * mm});
            skArc(sketch, "E21.7.6.5", {"start": v(56.5, -51.47) * mm, "mid": v(57.24, -53.27) * mm, "end": v(59.04, -54.01) * mm});
            skLineSegment(sketch, "E21.7.6.6", {"start": v(56.5, -40.68) * mm, "end": v(56.5, -51.47) * mm});
            skArc(sketch, "E21.7.6.7", {"start": v(59.04, -38.14) * mm, "mid": v(57.24, -38.88) * mm, "end": v(56.5, -40.68) * mm});
            skLineSegment(sketch, "E21.7.7.0", {"start": v(59.04, -56.55) * mm, "end": v(69.83, -56.55) * mm});
            skArc(sketch, "E21.7.7.1", {"start": v(72.37, -59.1) * mm, "mid": v(71.63, -57.3) * mm, "end": v(69.83, -56.55) * mm});
            skLineSegment(sketch, "E21.7.7.2", {"start": v(72.37, -59.1) * mm, "end": v(72.37, -69.89) * mm});
            skArc(sketch, "E21.7.7.3", {"start": v(69.83, -72.43) * mm, "mid": v(71.63, -71.68) * mm, "end": v(72.37, -69.89) * mm});
            skLineSegment(sketch, "E21.7.7.4", {"start": v(59.04, -72.43) * mm, "end": v(69.83, -72.43) * mm});
            skArc(sketch, "E21.7.7.5", {"start": v(56.5, -69.89) * mm, "mid": v(57.24, -71.68) * mm, "end": v(59.04, -72.43) * mm});
            skLineSegment(sketch, "E21.7.7.6", {"start": v(56.5, -59.1) * mm, "end": v(56.5, -69.89) * mm});
            skArc(sketch, "E21.7.7.7", {"start": v(59.04, -56.55) * mm, "mid": v(57.24, -57.3) * mm, "end": v(56.5, -59.1) * mm});
            skLineSegment(sketch, "E21.direction1", {"start": v(-69.87, 72.35) * mm, "end": v(-51.45, 72.35) * mm, "construction": true});
            skLineSegment(sketch, "E21.direction2", {"start": v(-69.87, 72.35) * mm, "end": v(-69.87, 53.94) * mm, "construction": true});
            skSolve(sketch);
        }
        {
            var Q0;
            Q0 = qSketchRegion(id + "F6", true);
            var Q1;
            Q1 = qConstructionFilter(qBodyType(qCreatedBy(id + "F6" ,EDGE), BodyType.WIRE), ConstructionObject.NO);
            extrude(context, id + "F7", {"entities" : qUnion([Q0]), "surfaceEntities" : qUnion([Q1]), "endBound" : BoundingType.SYMMETRIC, "oppositeDirection" : true, "depth" : 6.35 * mm, "offsetDistance" : 25.4 * mm});
        }
        {
            var Q0;
            Q0=makeQuery(id+"F7.opExtrude","CAP_FACE",FACE,{"disambiguationData":[OSD([sQuery(id+"F6.wireOp",EDGE,"E16.bottom"),sQuery(id+"F6.wireOp",EDGE,"E16.top"),sQuery(id+"F6.wireOp",EDGE,"E16.left"),sQuery(id+"F6.wireOp",EDGE,"E16.right"),sQuery(id+"F6.wireOp",EDGE,"E17.filletArc"),sQuery(id+"F6.wireOp",EDGE,"E18.filletArc"),sQuery(id+"F6.wireOp",EDGE,"E19.filletArc"),sQuery(id+"F6.wireOp",EDGE,"E20.filletArc")])],"isStart":true});
            var Q1;
            Q1=makeQuery(id+"F7.opExtrude","CAP_FACE",FACE,{"disambiguationData":[OSD([sQuery(id+"F6.wireOp",EDGE,"E21.1.0.0"),sQuery(id+"F6.wireOp",EDGE,"E21.1.0.1"),sQuery(id+"F6.wireOp",EDGE,"E21.1.0.2"),sQuery(id+"F6.wireOp",EDGE,"E21.1.0.3"),sQuery(id+"F6.wireOp",EDGE,"E21.1.0.4"),sQuery(id+"F6.wireOp",EDGE,"E21.1.0.5"),sQuery(id+"F6.wireOp",EDGE,"E21.1.0.6"),sQuery(id+"F6.wireOp",EDGE,"E21.1.0.7")])],"isStart":true});
            var Q2;
            Q2=makeQuery(id+"F7.opExtrude","CAP_FACE",FACE,{"disambiguationData":[OSD([sQuery(id+"F6.wireOp",EDGE,"E21.2.0.0"),sQuery(id+"F6.wireOp",EDGE,"E21.2.0.1"),sQuery(id+"F6.wireOp",EDGE,"E21.2.0.2"),sQuery(id+"F6.wireOp",EDGE,"E21.2.0.3"),sQuery(id+"F6.wireOp",EDGE,"E21.2.0.4"),sQuery(id+"F6.wireOp",EDGE,"E21.2.0.5"),sQuery(id+"F6.wireOp",EDGE,"E21.2.0.6"),sQuery(id+"F6.wireOp",EDGE,"E21.2.0.7")])],"isStart":true});
            var Q3;
            Q3=makeQuery(id+"F7.opExtrude","CAP_FACE",FACE,{"disambiguationData":[OSD([sQuery(id+"F6.wireOp",EDGE,"E21.3.0.0"),sQuery(id+"F6.wireOp",EDGE,"E21.3.0.1"),sQuery(id+"F6.wireOp",EDGE,"E21.3.0.2"),sQuery(id+"F6.wireOp",EDGE,"E21.3.0.3"),sQuery(id+"F6.wireOp",EDGE,"E21.3.0.4"),sQuery(id+"F6.wireOp",EDGE,"E21.3.0.5"),sQuery(id+"F6.wireOp",EDGE,"E21.3.0.6"),sQuery(id+"F6.wireOp",EDGE,"E21.3.0.7")])],"isStart":true});
            var Q4;
            Q4=makeQuery(id+"F7.opExtrude","CAP_FACE",FACE,{"disambiguationData":[OSD([sQuery(id+"F6.wireOp",EDGE,"E21.4.0.0"),sQuery(id+"F6.wireOp",EDGE,"E21.4.0.1"),sQuery(id+"F6.wireOp",EDGE,"E21.4.0.2"),sQuery(id+"F6.wireOp",EDGE,"E21.4.0.3"),sQuery(id+"F6.wireOp",EDGE,"E21.4.0.4"),sQuery(id+"F6.wireOp",EDGE,"E21.4.0.5"),sQuery(id+"F6.wireOp",EDGE,"E21.4.0.6"),sQuery(id+"F6.wireOp",EDGE,"E21.4.0.7")])],"isStart":true});
            var Q5;
            Q5=makeQuery(id+"F7.opExtrude","CAP_FACE",FACE,{"disambiguationData":[OSD([sQuery(id+"F6.wireOp",EDGE,"E21.5.0.0"),sQuery(id+"F6.wireOp",EDGE,"E21.5.0.1"),sQuery(id+"F6.wireOp",EDGE,"E21.5.0.2"),sQuery(id+"F6.wireOp",EDGE,"E21.5.0.3"),sQuery(id+"F6.wireOp",EDGE,"E21.5.0.4"),sQuery(id+"F6.wireOp",EDGE,"E21.5.0.5"),sQuery(id+"F6.wireOp",EDGE,"E21.5.0.6"),sQuery(id+"F6.wireOp",EDGE,"E21.5.0.7")])],"isStart":true});
            var Q6;
            Q6=makeQuery(id+"F7.opExtrude","CAP_FACE",FACE,{"disambiguationData":[OSD([sQuery(id+"F6.wireOp",EDGE,"E21.6.0.0"),sQuery(id+"F6.wireOp",EDGE,"E21.6.0.1"),sQuery(id+"F6.wireOp",EDGE,"E21.6.0.2"),sQuery(id+"F6.wireOp",EDGE,"E21.6.0.3"),sQuery(id+"F6.wireOp",EDGE,"E21.6.0.4"),sQuery(id+"F6.wireOp",EDGE,"E21.6.0.5"),sQuery(id+"F6.wireOp",EDGE,"E21.6.0.6"),sQuery(id+"F6.wireOp",EDGE,"E21.6.0.7")])],"isStart":true});
            var Q7;
            Q7=makeQuery(id+"F7.opExtrude","CAP_FACE",FACE,{"disambiguationData":[OSD([sQuery(id+"F6.wireOp",EDGE,"E21.7.0.0"),sQuery(id+"F6.wireOp",EDGE,"E21.7.0.1"),sQuery(id+"F6.wireOp",EDGE,"E21.7.0.2"),sQuery(id+"F6.wireOp",EDGE,"E21.7.0.3"),sQuery(id+"F6.wireOp",EDGE,"E21.7.0.4"),sQuery(id+"F6.wireOp",EDGE,"E21.7.0.5"),sQuery(id+"F6.wireOp",EDGE,"E21.7.0.6"),sQuery(id+"F6.wireOp",EDGE,"E21.7.0.7")])],"isStart":true});
            var Q8;
            Q8=makeQuery(id+"F7.opExtrude","CAP_FACE",FACE,{"disambiguationData":[OSD([sQuery(id+"F6.wireOp",EDGE,"E21.7.1.0"),sQuery(id+"F6.wireOp",EDGE,"E21.7.1.1"),sQuery(id+"F6.wireOp",EDGE,"E21.7.1.2"),sQuery(id+"F6.wireOp",EDGE,"E21.7.1.3"),sQuery(id+"F6.wireOp",EDGE,"E21.7.1.4"),sQuery(id+"F6.wireOp",EDGE,"E21.7.1.5"),sQuery(id+"F6.wireOp",EDGE,"E21.7.1.6"),sQuery(id+"F6.wireOp",EDGE,"E21.7.1.7")])],"isStart":true});
            var Q9;
            Q9=makeQuery(id+"F7.opExtrude","CAP_FACE",FACE,{"disambiguationData":[OSD([sQuery(id+"F6.wireOp",EDGE,"E21.6.1.0"),sQuery(id+"F6.wireOp",EDGE,"E21.6.1.1"),sQuery(id+"F6.wireOp",EDGE,"E21.6.1.2"),sQuery(id+"F6.wireOp",EDGE,"E21.6.1.3"),sQuery(id+"F6.wireOp",EDGE,"E21.6.1.4"),sQuery(id+"F6.wireOp",EDGE,"E21.6.1.5"),sQuery(id+"F6.wireOp",EDGE,"E21.6.1.6"),sQuery(id+"F6.wireOp",EDGE,"E21.6.1.7")])],"isStart":true});
            var Q10;
            Q10=makeQuery(id+"F7.opExtrude","CAP_FACE",FACE,{"disambiguationData":[OSD([sQuery(id+"F6.wireOp",EDGE,"E21.5.1.0"),sQuery(id+"F6.wireOp",EDGE,"E21.5.1.1"),sQuery(id+"F6.wireOp",EDGE,"E21.5.1.2"),sQuery(id+"F6.wireOp",EDGE,"E21.5.1.3"),sQuery(id+"F6.wireOp",EDGE,"E21.5.1.4"),sQuery(id+"F6.wireOp",EDGE,"E21.5.1.5"),sQuery(id+"F6.wireOp",EDGE,"E21.5.1.6"),sQuery(id+"F6.wireOp",EDGE,"E21.5.1.7")])],"isStart":true});
            var Q11;
            Q11=makeQuery(id+"F7.opExtrude","CAP_FACE",FACE,{"disambiguationData":[OSD([sQuery(id+"F6.wireOp",EDGE,"E21.4.1.0"),sQuery(id+"F6.wireOp",EDGE,"E21.4.1.1"),sQuery(id+"F6.wireOp",EDGE,"E21.4.1.2"),sQuery(id+"F6.wireOp",EDGE,"E21.4.1.3"),sQuery(id+"F6.wireOp",EDGE,"E21.4.1.4"),sQuery(id+"F6.wireOp",EDGE,"E21.4.1.5"),sQuery(id+"F6.wireOp",EDGE,"E21.4.1.6"),sQuery(id+"F6.wireOp",EDGE,"E21.4.1.7")])],"isStart":true});
            var Q12;
            Q12=makeQuery(id+"F7.opExtrude","CAP_FACE",FACE,{"disambiguationData":[OSD([sQuery(id+"F6.wireOp",EDGE,"E21.3.1.0"),sQuery(id+"F6.wireOp",EDGE,"E21.3.1.1"),sQuery(id+"F6.wireOp",EDGE,"E21.3.1.2"),sQuery(id+"F6.wireOp",EDGE,"E21.3.1.3"),sQuery(id+"F6.wireOp",EDGE,"E21.3.1.4"),sQuery(id+"F6.wireOp",EDGE,"E21.3.1.5"),sQuery(id+"F6.wireOp",EDGE,"E21.3.1.6"),sQuery(id+"F6.wireOp",EDGE,"E21.3.1.7")])],"isStart":true});
            var Q13;
            Q13=makeQuery(id+"F7.opExtrude","CAP_FACE",FACE,{"disambiguationData":[OSD([sQuery(id+"F6.wireOp",EDGE,"E21.2.1.0"),sQuery(id+"F6.wireOp",EDGE,"E21.2.1.1"),sQuery(id+"F6.wireOp",EDGE,"E21.2.1.2"),sQuery(id+"F6.wireOp",EDGE,"E21.2.1.3"),sQuery(id+"F6.wireOp",EDGE,"E21.2.1.4"),sQuery(id+"F6.wireOp",EDGE,"E21.2.1.5"),sQuery(id+"F6.wireOp",EDGE,"E21.2.1.6"),sQuery(id+"F6.wireOp",EDGE,"E21.2.1.7")])],"isStart":true});
            var Q14;
            Q14=makeQuery(id+"F7.opExtrude","CAP_FACE",FACE,{"disambiguationData":[OSD([sQuery(id+"F6.wireOp",EDGE,"E21.1.1.0"),sQuery(id+"F6.wireOp",EDGE,"E21.1.1.1"),sQuery(id+"F6.wireOp",EDGE,"E21.1.1.2"),sQuery(id+"F6.wireOp",EDGE,"E21.1.1.3"),sQuery(id+"F6.wireOp",EDGE,"E21.1.1.4"),sQuery(id+"F6.wireOp",EDGE,"E21.1.1.5"),sQuery(id+"F6.wireOp",EDGE,"E21.1.1.6"),sQuery(id+"F6.wireOp",EDGE,"E21.1.1.7")])],"isStart":true});
            var Q15;
            Q15=makeQuery(id+"F7.opExtrude","CAP_FACE",FACE,{"disambiguationData":[OSD([sQuery(id+"F6.wireOp",EDGE,"E21.0.1.0"),sQuery(id+"F6.wireOp",EDGE,"E21.0.1.1"),sQuery(id+"F6.wireOp",EDGE,"E21.0.1.2"),sQuery(id+"F6.wireOp",EDGE,"E21.0.1.3"),sQuery(id+"F6.wireOp",EDGE,"E21.0.1.4"),sQuery(id+"F6.wireOp",EDGE,"E21.0.1.5"),sQuery(id+"F6.wireOp",EDGE,"E21.0.1.6"),sQuery(id+"F6.wireOp",EDGE,"E21.0.1.7")])],"isStart":true});
            var Q16;
            Q16=makeQuery(id+"F7.opExtrude","CAP_FACE",FACE,{"disambiguationData":[OSD([sQuery(id+"F6.wireOp",EDGE,"E21.0.2.0"),sQuery(id+"F6.wireOp",EDGE,"E21.0.2.1"),sQuery(id+"F6.wireOp",EDGE,"E21.0.2.2"),sQuery(id+"F6.wireOp",EDGE,"E21.0.2.3"),sQuery(id+"F6.wireOp",EDGE,"E21.0.2.4"),sQuery(id+"F6.wireOp",EDGE,"E21.0.2.5"),sQuery(id+"F6.wireOp",EDGE,"E21.0.2.6"),sQuery(id+"F6.wireOp",EDGE,"E21.0.2.7")])],"isStart":true});
            var Q17;
            Q17=makeQuery(id+"F7.opExtrude","CAP_FACE",FACE,{"disambiguationData":[OSD([sQuery(id+"F6.wireOp",EDGE,"E21.1.2.0"),sQuery(id+"F6.wireOp",EDGE,"E21.1.2.1"),sQuery(id+"F6.wireOp",EDGE,"E21.1.2.2"),sQuery(id+"F6.wireOp",EDGE,"E21.1.2.3"),sQuery(id+"F6.wireOp",EDGE,"E21.1.2.4"),sQuery(id+"F6.wireOp",EDGE,"E21.1.2.5"),sQuery(id+"F6.wireOp",EDGE,"E21.1.2.6"),sQuery(id+"F6.wireOp",EDGE,"E21.1.2.7")])],"isStart":true});
            var Q18;
            Q18=makeQuery(id+"F7.opExtrude","CAP_FACE",FACE,{"disambiguationData":[OSD([sQuery(id+"F6.wireOp",EDGE,"E21.2.2.0"),sQuery(id+"F6.wireOp",EDGE,"E21.2.2.1"),sQuery(id+"F6.wireOp",EDGE,"E21.2.2.2"),sQuery(id+"F6.wireOp",EDGE,"E21.2.2.3"),sQuery(id+"F6.wireOp",EDGE,"E21.2.2.4"),sQuery(id+"F6.wireOp",EDGE,"E21.2.2.5"),sQuery(id+"F6.wireOp",EDGE,"E21.2.2.6"),sQuery(id+"F6.wireOp",EDGE,"E21.2.2.7")])],"isStart":true});
            var Q19;
            Q19=makeQuery(id+"F7.opExtrude","CAP_FACE",FACE,{"disambiguationData":[OSD([sQuery(id+"F6.wireOp",EDGE,"E21.3.2.0"),sQuery(id+"F6.wireOp",EDGE,"E21.3.2.1"),sQuery(id+"F6.wireOp",EDGE,"E21.3.2.2"),sQuery(id+"F6.wireOp",EDGE,"E21.3.2.3"),sQuery(id+"F6.wireOp",EDGE,"E21.3.2.4"),sQuery(id+"F6.wireOp",EDGE,"E21.3.2.5"),sQuery(id+"F6.wireOp",EDGE,"E21.3.2.6"),sQuery(id+"F6.wireOp",EDGE,"E21.3.2.7")])],"isStart":true});
            var Q20;
            Q20=makeQuery(id+"F7.opExtrude","CAP_FACE",FACE,{"disambiguationData":[OSD([sQuery(id+"F6.wireOp",EDGE,"E21.4.2.0"),sQuery(id+"F6.wireOp",EDGE,"E21.4.2.1"),sQuery(id+"F6.wireOp",EDGE,"E21.4.2.2"),sQuery(id+"F6.wireOp",EDGE,"E21.4.2.3"),sQuery(id+"F6.wireOp",EDGE,"E21.4.2.4"),sQuery(id+"F6.wireOp",EDGE,"E21.4.2.5"),sQuery(id+"F6.wireOp",EDGE,"E21.4.2.6"),sQuery(id+"F6.wireOp",EDGE,"E21.4.2.7")])],"isStart":true});
            var Q21;
            Q21=makeQuery(id+"F7.opExtrude","CAP_FACE",FACE,{"disambiguationData":[OSD([sQuery(id+"F6.wireOp",EDGE,"E21.5.2.0"),sQuery(id+"F6.wireOp",EDGE,"E21.5.2.1"),sQuery(id+"F6.wireOp",EDGE,"E21.5.2.2"),sQuery(id+"F6.wireOp",EDGE,"E21.5.2.3"),sQuery(id+"F6.wireOp",EDGE,"E21.5.2.4"),sQuery(id+"F6.wireOp",EDGE,"E21.5.2.5"),sQuery(id+"F6.wireOp",EDGE,"E21.5.2.6"),sQuery(id+"F6.wireOp",EDGE,"E21.5.2.7")])],"isStart":true});
            var Q22;
            Q22=makeQuery(id+"F7.opExtrude","CAP_FACE",FACE,{"disambiguationData":[OSD([sQuery(id+"F6.wireOp",EDGE,"E21.6.2.0"),sQuery(id+"F6.wireOp",EDGE,"E21.6.2.1"),sQuery(id+"F6.wireOp",EDGE,"E21.6.2.2"),sQuery(id+"F6.wireOp",EDGE,"E21.6.2.3"),sQuery(id+"F6.wireOp",EDGE,"E21.6.2.4"),sQuery(id+"F6.wireOp",EDGE,"E21.6.2.5"),sQuery(id+"F6.wireOp",EDGE,"E21.6.2.6"),sQuery(id+"F6.wireOp",EDGE,"E21.6.2.7")])],"isStart":true});
            var Q23;
            Q23=makeQuery(id+"F7.opExtrude","CAP_FACE",FACE,{"disambiguationData":[OSD([sQuery(id+"F6.wireOp",EDGE,"E21.7.2.0"),sQuery(id+"F6.wireOp",EDGE,"E21.7.2.1"),sQuery(id+"F6.wireOp",EDGE,"E21.7.2.2"),sQuery(id+"F6.wireOp",EDGE,"E21.7.2.3"),sQuery(id+"F6.wireOp",EDGE,"E21.7.2.4"),sQuery(id+"F6.wireOp",EDGE,"E21.7.2.5"),sQuery(id+"F6.wireOp",EDGE,"E21.7.2.6"),sQuery(id+"F6.wireOp",EDGE,"E21.7.2.7")])],"isStart":true});
            var Q24;
            Q24=makeQuery(id+"F7.opExtrude","CAP_FACE",FACE,{"disambiguationData":[OSD([sQuery(id+"F6.wireOp",EDGE,"E21.7.3.0"),sQuery(id+"F6.wireOp",EDGE,"E21.7.3.1"),sQuery(id+"F6.wireOp",EDGE,"E21.7.3.2"),sQuery(id+"F6.wireOp",EDGE,"E21.7.3.3"),sQuery(id+"F6.wireOp",EDGE,"E21.7.3.4"),sQuery(id+"F6.wireOp",EDGE,"E21.7.3.5"),sQuery(id+"F6.wireOp",EDGE,"E21.7.3.6"),sQuery(id+"F6.wireOp",EDGE,"E21.7.3.7")])],"isStart":true});
            var Q25;
            Q25=makeQuery(id+"F7.opExtrude","CAP_FACE",FACE,{"disambiguationData":[OSD([sQuery(id+"F6.wireOp",EDGE,"E21.6.3.0"),sQuery(id+"F6.wireOp",EDGE,"E21.6.3.1"),sQuery(id+"F6.wireOp",EDGE,"E21.6.3.2"),sQuery(id+"F6.wireOp",EDGE,"E21.6.3.3"),sQuery(id+"F6.wireOp",EDGE,"E21.6.3.4"),sQuery(id+"F6.wireOp",EDGE,"E21.6.3.5"),sQuery(id+"F6.wireOp",EDGE,"E21.6.3.6"),sQuery(id+"F6.wireOp",EDGE,"E21.6.3.7")])],"isStart":true});
            var Q26;
            Q26=makeQuery(id+"F7.opExtrude","CAP_FACE",FACE,{"disambiguationData":[OSD([sQuery(id+"F6.wireOp",EDGE,"E21.5.3.0"),sQuery(id+"F6.wireOp",EDGE,"E21.5.3.1"),sQuery(id+"F6.wireOp",EDGE,"E21.5.3.2"),sQuery(id+"F6.wireOp",EDGE,"E21.5.3.3"),sQuery(id+"F6.wireOp",EDGE,"E21.5.3.4"),sQuery(id+"F6.wireOp",EDGE,"E21.5.3.5"),sQuery(id+"F6.wireOp",EDGE,"E21.5.3.6"),sQuery(id+"F6.wireOp",EDGE,"E21.5.3.7")])],"isStart":true});
            var Q27;
            Q27=makeQuery(id+"F7.opExtrude","CAP_FACE",FACE,{"disambiguationData":[OSD([sQuery(id+"F6.wireOp",EDGE,"E21.4.3.0"),sQuery(id+"F6.wireOp",EDGE,"E21.4.3.1"),sQuery(id+"F6.wireOp",EDGE,"E21.4.3.2"),sQuery(id+"F6.wireOp",EDGE,"E21.4.3.3"),sQuery(id+"F6.wireOp",EDGE,"E21.4.3.4"),sQuery(id+"F6.wireOp",EDGE,"E21.4.3.5"),sQuery(id+"F6.wireOp",EDGE,"E21.4.3.6"),sQuery(id+"F6.wireOp",EDGE,"E21.4.3.7")])],"isStart":true});
            var Q28;
            Q28=makeQuery(id+"F7.opExtrude","CAP_FACE",FACE,{"disambiguationData":[OSD([sQuery(id+"F6.wireOp",EDGE,"E21.3.3.0"),sQuery(id+"F6.wireOp",EDGE,"E21.3.3.1"),sQuery(id+"F6.wireOp",EDGE,"E21.3.3.2"),sQuery(id+"F6.wireOp",EDGE,"E21.3.3.3"),sQuery(id+"F6.wireOp",EDGE,"E21.3.3.4"),sQuery(id+"F6.wireOp",EDGE,"E21.3.3.5"),sQuery(id+"F6.wireOp",EDGE,"E21.3.3.6"),sQuery(id+"F6.wireOp",EDGE,"E21.3.3.7")])],"isStart":true});
            var Q29;
            Q29=makeQuery(id+"F7.opExtrude","CAP_FACE",FACE,{"disambiguationData":[OSD([sQuery(id+"F6.wireOp",EDGE,"E21.2.3.0"),sQuery(id+"F6.wireOp",EDGE,"E21.2.3.1"),sQuery(id+"F6.wireOp",EDGE,"E21.2.3.2"),sQuery(id+"F6.wireOp",EDGE,"E21.2.3.3"),sQuery(id+"F6.wireOp",EDGE,"E21.2.3.4"),sQuery(id+"F6.wireOp",EDGE,"E21.2.3.5"),sQuery(id+"F6.wireOp",EDGE,"E21.2.3.6"),sQuery(id+"F6.wireOp",EDGE,"E21.2.3.7")])],"isStart":true});
            var Q30;
            Q30=makeQuery(id+"F7.opExtrude","CAP_FACE",FACE,{"disambiguationData":[OSD([sQuery(id+"F6.wireOp",EDGE,"E21.1.3.0"),sQuery(id+"F6.wireOp",EDGE,"E21.1.3.1"),sQuery(id+"F6.wireOp",EDGE,"E21.1.3.2"),sQuery(id+"F6.wireOp",EDGE,"E21.1.3.3"),sQuery(id+"F6.wireOp",EDGE,"E21.1.3.4"),sQuery(id+"F6.wireOp",EDGE,"E21.1.3.5"),sQuery(id+"F6.wireOp",EDGE,"E21.1.3.6"),sQuery(id+"F6.wireOp",EDGE,"E21.1.3.7")])],"isStart":true});
            var Q31;
            Q31=makeQuery(id+"F7.opExtrude","CAP_FACE",FACE,{"disambiguationData":[OSD([sQuery(id+"F6.wireOp",EDGE,"E21.0.3.0"),sQuery(id+"F6.wireOp",EDGE,"E21.0.3.1"),sQuery(id+"F6.wireOp",EDGE,"E21.0.3.2"),sQuery(id+"F6.wireOp",EDGE,"E21.0.3.3"),sQuery(id+"F6.wireOp",EDGE,"E21.0.3.4"),sQuery(id+"F6.wireOp",EDGE,"E21.0.3.5"),sQuery(id+"F6.wireOp",EDGE,"E21.0.3.6"),sQuery(id+"F6.wireOp",EDGE,"E21.0.3.7")])],"isStart":true});
            var Q32;
            Q32=makeQuery(id+"F7.opExtrude","CAP_FACE",FACE,{"disambiguationData":[OSD([sQuery(id+"F6.wireOp",EDGE,"E21.0.4.0"),sQuery(id+"F6.wireOp",EDGE,"E21.0.4.1"),sQuery(id+"F6.wireOp",EDGE,"E21.0.4.2"),sQuery(id+"F6.wireOp",EDGE,"E21.0.4.3"),sQuery(id+"F6.wireOp",EDGE,"E21.0.4.4"),sQuery(id+"F6.wireOp",EDGE,"E21.0.4.5"),sQuery(id+"F6.wireOp",EDGE,"E21.0.4.6"),sQuery(id+"F6.wireOp",EDGE,"E21.0.4.7")])],"isStart":true});
            var Q33;
            Q33=makeQuery(id+"F7.opExtrude","CAP_FACE",FACE,{"disambiguationData":[OSD([sQuery(id+"F6.wireOp",EDGE,"E21.1.4.0"),sQuery(id+"F6.wireOp",EDGE,"E21.1.4.1"),sQuery(id+"F6.wireOp",EDGE,"E21.1.4.2"),sQuery(id+"F6.wireOp",EDGE,"E21.1.4.3"),sQuery(id+"F6.wireOp",EDGE,"E21.1.4.4"),sQuery(id+"F6.wireOp",EDGE,"E21.1.4.5"),sQuery(id+"F6.wireOp",EDGE,"E21.1.4.6"),sQuery(id+"F6.wireOp",EDGE,"E21.1.4.7")])],"isStart":true});
            var Q34;
            Q34=makeQuery(id+"F7.opExtrude","CAP_FACE",FACE,{"disambiguationData":[OSD([sQuery(id+"F6.wireOp",EDGE,"E21.2.4.0"),sQuery(id+"F6.wireOp",EDGE,"E21.2.4.1"),sQuery(id+"F6.wireOp",EDGE,"E21.2.4.2"),sQuery(id+"F6.wireOp",EDGE,"E21.2.4.3"),sQuery(id+"F6.wireOp",EDGE,"E21.2.4.4"),sQuery(id+"F6.wireOp",EDGE,"E21.2.4.5"),sQuery(id+"F6.wireOp",EDGE,"E21.2.4.6"),sQuery(id+"F6.wireOp",EDGE,"E21.2.4.7")])],"isStart":true});
            var Q35;
            Q35=makeQuery(id+"F7.opExtrude","CAP_FACE",FACE,{"disambiguationData":[OSD([sQuery(id+"F6.wireOp",EDGE,"E21.3.4.0"),sQuery(id+"F6.wireOp",EDGE,"E21.3.4.1"),sQuery(id+"F6.wireOp",EDGE,"E21.3.4.2"),sQuery(id+"F6.wireOp",EDGE,"E21.3.4.3"),sQuery(id+"F6.wireOp",EDGE,"E21.3.4.4"),sQuery(id+"F6.wireOp",EDGE,"E21.3.4.5"),sQuery(id+"F6.wireOp",EDGE,"E21.3.4.6"),sQuery(id+"F6.wireOp",EDGE,"E21.3.4.7")])],"isStart":true});
            var Q36;
            Q36=makeQuery(id+"F7.opExtrude","CAP_FACE",FACE,{"disambiguationData":[OSD([sQuery(id+"F6.wireOp",EDGE,"E21.4.4.0"),sQuery(id+"F6.wireOp",EDGE,"E21.4.4.1"),sQuery(id+"F6.wireOp",EDGE,"E21.4.4.2"),sQuery(id+"F6.wireOp",EDGE,"E21.4.4.3"),sQuery(id+"F6.wireOp",EDGE,"E21.4.4.4"),sQuery(id+"F6.wireOp",EDGE,"E21.4.4.5"),sQuery(id+"F6.wireOp",EDGE,"E21.4.4.6"),sQuery(id+"F6.wireOp",EDGE,"E21.4.4.7")])],"isStart":true});
            var Q37;
            Q37=makeQuery(id+"F7.opExtrude","CAP_FACE",FACE,{"disambiguationData":[OSD([sQuery(id+"F6.wireOp",EDGE,"E21.5.4.0"),sQuery(id+"F6.wireOp",EDGE,"E21.5.4.1"),sQuery(id+"F6.wireOp",EDGE,"E21.5.4.2"),sQuery(id+"F6.wireOp",EDGE,"E21.5.4.3"),sQuery(id+"F6.wireOp",EDGE,"E21.5.4.4"),sQuery(id+"F6.wireOp",EDGE,"E21.5.4.5"),sQuery(id+"F6.wireOp",EDGE,"E21.5.4.6"),sQuery(id+"F6.wireOp",EDGE,"E21.5.4.7")])],"isStart":true});
            var Q38;
            Q38=makeQuery(id+"F7.opExtrude","CAP_FACE",FACE,{"disambiguationData":[OSD([sQuery(id+"F6.wireOp",EDGE,"E21.6.4.0"),sQuery(id+"F6.wireOp",EDGE,"E21.6.4.1"),sQuery(id+"F6.wireOp",EDGE,"E21.6.4.2"),sQuery(id+"F6.wireOp",EDGE,"E21.6.4.3"),sQuery(id+"F6.wireOp",EDGE,"E21.6.4.4"),sQuery(id+"F6.wireOp",EDGE,"E21.6.4.5"),sQuery(id+"F6.wireOp",EDGE,"E21.6.4.6"),sQuery(id+"F6.wireOp",EDGE,"E21.6.4.7")])],"isStart":true});
            var Q39;
            Q39=makeQuery(id+"F7.opExtrude","CAP_FACE",FACE,{"disambiguationData":[OSD([sQuery(id+"F6.wireOp",EDGE,"E21.7.4.0"),sQuery(id+"F6.wireOp",EDGE,"E21.7.4.1"),sQuery(id+"F6.wireOp",EDGE,"E21.7.4.2"),sQuery(id+"F6.wireOp",EDGE,"E21.7.4.3"),sQuery(id+"F6.wireOp",EDGE,"E21.7.4.4"),sQuery(id+"F6.wireOp",EDGE,"E21.7.4.5"),sQuery(id+"F6.wireOp",EDGE,"E21.7.4.6"),sQuery(id+"F6.wireOp",EDGE,"E21.7.4.7")])],"isStart":true});
            var Q40;
            Q40=makeQuery(id+"F7.opExtrude","CAP_FACE",FACE,{"disambiguationData":[OSD([sQuery(id+"F6.wireOp",EDGE,"E21.7.5.0"),sQuery(id+"F6.wireOp",EDGE,"E21.7.5.1"),sQuery(id+"F6.wireOp",EDGE,"E21.7.5.2"),sQuery(id+"F6.wireOp",EDGE,"E21.7.5.3"),sQuery(id+"F6.wireOp",EDGE,"E21.7.5.4"),sQuery(id+"F6.wireOp",EDGE,"E21.7.5.5"),sQuery(id+"F6.wireOp",EDGE,"E21.7.5.6"),sQuery(id+"F6.wireOp",EDGE,"E21.7.5.7")])],"isStart":true});
            var Q41;
            Q41=makeQuery(id+"F7.opExtrude","CAP_FACE",FACE,{"disambiguationData":[OSD([sQuery(id+"F6.wireOp",EDGE,"E21.6.5.0"),sQuery(id+"F6.wireOp",EDGE,"E21.6.5.1"),sQuery(id+"F6.wireOp",EDGE,"E21.6.5.2"),sQuery(id+"F6.wireOp",EDGE,"E21.6.5.3"),sQuery(id+"F6.wireOp",EDGE,"E21.6.5.4"),sQuery(id+"F6.wireOp",EDGE,"E21.6.5.5"),sQuery(id+"F6.wireOp",EDGE,"E21.6.5.6"),sQuery(id+"F6.wireOp",EDGE,"E21.6.5.7")])],"isStart":true});
            var Q42;
            Q42=makeQuery(id+"F7.opExtrude","CAP_FACE",FACE,{"disambiguationData":[OSD([sQuery(id+"F6.wireOp",EDGE,"E21.5.5.0"),sQuery(id+"F6.wireOp",EDGE,"E21.5.5.1"),sQuery(id+"F6.wireOp",EDGE,"E21.5.5.2"),sQuery(id+"F6.wireOp",EDGE,"E21.5.5.3"),sQuery(id+"F6.wireOp",EDGE,"E21.5.5.4"),sQuery(id+"F6.wireOp",EDGE,"E21.5.5.5"),sQuery(id+"F6.wireOp",EDGE,"E21.5.5.6"),sQuery(id+"F6.wireOp",EDGE,"E21.5.5.7")])],"isStart":true});
            var Q43;
            Q43=makeQuery(id+"F7.opExtrude","CAP_FACE",FACE,{"disambiguationData":[OSD([sQuery(id+"F6.wireOp",EDGE,"E21.4.5.0"),sQuery(id+"F6.wireOp",EDGE,"E21.4.5.1"),sQuery(id+"F6.wireOp",EDGE,"E21.4.5.2"),sQuery(id+"F6.wireOp",EDGE,"E21.4.5.3"),sQuery(id+"F6.wireOp",EDGE,"E21.4.5.4"),sQuery(id+"F6.wireOp",EDGE,"E21.4.5.5"),sQuery(id+"F6.wireOp",EDGE,"E21.4.5.6"),sQuery(id+"F6.wireOp",EDGE,"E21.4.5.7")])],"isStart":true});
            var Q44;
            Q44=makeQuery(id+"F7.opExtrude","CAP_FACE",FACE,{"disambiguationData":[OSD([sQuery(id+"F6.wireOp",EDGE,"E21.3.5.0"),sQuery(id+"F6.wireOp",EDGE,"E21.3.5.1"),sQuery(id+"F6.wireOp",EDGE,"E21.3.5.2"),sQuery(id+"F6.wireOp",EDGE,"E21.3.5.3"),sQuery(id+"F6.wireOp",EDGE,"E21.3.5.4"),sQuery(id+"F6.wireOp",EDGE,"E21.3.5.5"),sQuery(id+"F6.wireOp",EDGE,"E21.3.5.6"),sQuery(id+"F6.wireOp",EDGE,"E21.3.5.7")])],"isStart":true});
            var Q45;
            Q45=makeQuery(id+"F7.opExtrude","CAP_FACE",FACE,{"disambiguationData":[OSD([sQuery(id+"F6.wireOp",EDGE,"E21.2.5.0"),sQuery(id+"F6.wireOp",EDGE,"E21.2.5.1"),sQuery(id+"F6.wireOp",EDGE,"E21.2.5.2"),sQuery(id+"F6.wireOp",EDGE,"E21.2.5.3"),sQuery(id+"F6.wireOp",EDGE,"E21.2.5.4"),sQuery(id+"F6.wireOp",EDGE,"E21.2.5.5"),sQuery(id+"F6.wireOp",EDGE,"E21.2.5.6"),sQuery(id+"F6.wireOp",EDGE,"E21.2.5.7")])],"isStart":true});
            var Q46;
            Q46=makeQuery(id+"F7.opExtrude","CAP_FACE",FACE,{"disambiguationData":[OSD([sQuery(id+"F6.wireOp",EDGE,"E21.1.5.0"),sQuery(id+"F6.wireOp",EDGE,"E21.1.5.1"),sQuery(id+"F6.wireOp",EDGE,"E21.1.5.2"),sQuery(id+"F6.wireOp",EDGE,"E21.1.5.3"),sQuery(id+"F6.wireOp",EDGE,"E21.1.5.4"),sQuery(id+"F6.wireOp",EDGE,"E21.1.5.5"),sQuery(id+"F6.wireOp",EDGE,"E21.1.5.6"),sQuery(id+"F6.wireOp",EDGE,"E21.1.5.7")])],"isStart":true});
            var Q47;
            Q47=makeQuery(id+"F7.opExtrude","CAP_FACE",FACE,{"disambiguationData":[OSD([sQuery(id+"F6.wireOp",EDGE,"E21.0.5.0"),sQuery(id+"F6.wireOp",EDGE,"E21.0.5.1"),sQuery(id+"F6.wireOp",EDGE,"E21.0.5.2"),sQuery(id+"F6.wireOp",EDGE,"E21.0.5.3"),sQuery(id+"F6.wireOp",EDGE,"E21.0.5.4"),sQuery(id+"F6.wireOp",EDGE,"E21.0.5.5"),sQuery(id+"F6.wireOp",EDGE,"E21.0.5.6"),sQuery(id+"F6.wireOp",EDGE,"E21.0.5.7")])],"isStart":true});
            var Q48;
            Q48=makeQuery(id+"F7.opExtrude","CAP_FACE",FACE,{"disambiguationData":[OSD([sQuery(id+"F6.wireOp",EDGE,"E21.0.6.0"),sQuery(id+"F6.wireOp",EDGE,"E21.0.6.1"),sQuery(id+"F6.wireOp",EDGE,"E21.0.6.2"),sQuery(id+"F6.wireOp",EDGE,"E21.0.6.3"),sQuery(id+"F6.wireOp",EDGE,"E21.0.6.4"),sQuery(id+"F6.wireOp",EDGE,"E21.0.6.5"),sQuery(id+"F6.wireOp",EDGE,"E21.0.6.6"),sQuery(id+"F6.wireOp",EDGE,"E21.0.6.7")])],"isStart":true});
            var Q49;
            Q49=makeQuery(id+"F7.opExtrude","CAP_FACE",FACE,{"disambiguationData":[OSD([sQuery(id+"F6.wireOp",EDGE,"E21.0.7.0"),sQuery(id+"F6.wireOp",EDGE,"E21.0.7.1"),sQuery(id+"F6.wireOp",EDGE,"E21.0.7.2"),sQuery(id+"F6.wireOp",EDGE,"E21.0.7.3"),sQuery(id+"F6.wireOp",EDGE,"E21.0.7.4"),sQuery(id+"F6.wireOp",EDGE,"E21.0.7.5"),sQuery(id+"F6.wireOp",EDGE,"E21.0.7.6"),sQuery(id+"F6.wireOp",EDGE,"E21.0.7.7")])],"isStart":true});
            var Q50;
            Q50=makeQuery(id+"F7.opExtrude","CAP_FACE",FACE,{"disambiguationData":[OSD([sQuery(id+"F6.wireOp",EDGE,"E21.1.6.0"),sQuery(id+"F6.wireOp",EDGE,"E21.1.6.1"),sQuery(id+"F6.wireOp",EDGE,"E21.1.6.2"),sQuery(id+"F6.wireOp",EDGE,"E21.1.6.3"),sQuery(id+"F6.wireOp",EDGE,"E21.1.6.4"),sQuery(id+"F6.wireOp",EDGE,"E21.1.6.5"),sQuery(id+"F6.wireOp",EDGE,"E21.1.6.6"),sQuery(id+"F6.wireOp",EDGE,"E21.1.6.7")])],"isStart":true});
            var Q51;
            Q51=makeQuery(id+"F7.opExtrude","CAP_FACE",FACE,{"disambiguationData":[OSD([sQuery(id+"F6.wireOp",EDGE,"E21.1.7.0"),sQuery(id+"F6.wireOp",EDGE,"E21.1.7.1"),sQuery(id+"F6.wireOp",EDGE,"E21.1.7.2"),sQuery(id+"F6.wireOp",EDGE,"E21.1.7.3"),sQuery(id+"F6.wireOp",EDGE,"E21.1.7.4"),sQuery(id+"F6.wireOp",EDGE,"E21.1.7.5"),sQuery(id+"F6.wireOp",EDGE,"E21.1.7.6"),sQuery(id+"F6.wireOp",EDGE,"E21.1.7.7")])],"isStart":true});
            var Q52;
            Q52=makeQuery(id+"F7.opExtrude","CAP_FACE",FACE,{"disambiguationData":[OSD([sQuery(id+"F6.wireOp",EDGE,"E21.2.6.0"),sQuery(id+"F6.wireOp",EDGE,"E21.2.6.1"),sQuery(id+"F6.wireOp",EDGE,"E21.2.6.2"),sQuery(id+"F6.wireOp",EDGE,"E21.2.6.3"),sQuery(id+"F6.wireOp",EDGE,"E21.2.6.4"),sQuery(id+"F6.wireOp",EDGE,"E21.2.6.5"),sQuery(id+"F6.wireOp",EDGE,"E21.2.6.6"),sQuery(id+"F6.wireOp",EDGE,"E21.2.6.7")])],"isStart":true});
            var Q53;
            Q53=makeQuery(id+"F7.opExtrude","CAP_FACE",FACE,{"disambiguationData":[OSD([sQuery(id+"F6.wireOp",EDGE,"E21.2.7.0"),sQuery(id+"F6.wireOp",EDGE,"E21.2.7.1"),sQuery(id+"F6.wireOp",EDGE,"E21.2.7.2"),sQuery(id+"F6.wireOp",EDGE,"E21.2.7.3"),sQuery(id+"F6.wireOp",EDGE,"E21.2.7.4"),sQuery(id+"F6.wireOp",EDGE,"E21.2.7.5"),sQuery(id+"F6.wireOp",EDGE,"E21.2.7.6"),sQuery(id+"F6.wireOp",EDGE,"E21.2.7.7")])],"isStart":true});
            var Q54;
            Q54=makeQuery(id+"F7.opExtrude","CAP_FACE",FACE,{"disambiguationData":[OSD([sQuery(id+"F6.wireOp",EDGE,"E21.3.7.0"),sQuery(id+"F6.wireOp",EDGE,"E21.3.7.1"),sQuery(id+"F6.wireOp",EDGE,"E21.3.7.2"),sQuery(id+"F6.wireOp",EDGE,"E21.3.7.3"),sQuery(id+"F6.wireOp",EDGE,"E21.3.7.4"),sQuery(id+"F6.wireOp",EDGE,"E21.3.7.5"),sQuery(id+"F6.wireOp",EDGE,"E21.3.7.6"),sQuery(id+"F6.wireOp",EDGE,"E21.3.7.7")])],"isStart":true});
            var Q55;
            Q55=makeQuery(id+"F7.opExtrude","CAP_FACE",FACE,{"disambiguationData":[OSD([sQuery(id+"F6.wireOp",EDGE,"E21.3.6.0"),sQuery(id+"F6.wireOp",EDGE,"E21.3.6.1"),sQuery(id+"F6.wireOp",EDGE,"E21.3.6.2"),sQuery(id+"F6.wireOp",EDGE,"E21.3.6.3"),sQuery(id+"F6.wireOp",EDGE,"E21.3.6.4"),sQuery(id+"F6.wireOp",EDGE,"E21.3.6.5"),sQuery(id+"F6.wireOp",EDGE,"E21.3.6.6"),sQuery(id+"F6.wireOp",EDGE,"E21.3.6.7")])],"isStart":true});
            var Q56;
            Q56=makeQuery(id+"F7.opExtrude","CAP_FACE",FACE,{"disambiguationData":[OSD([sQuery(id+"F6.wireOp",EDGE,"E21.4.6.0"),sQuery(id+"F6.wireOp",EDGE,"E21.4.6.1"),sQuery(id+"F6.wireOp",EDGE,"E21.4.6.2"),sQuery(id+"F6.wireOp",EDGE,"E21.4.6.3"),sQuery(id+"F6.wireOp",EDGE,"E21.4.6.4"),sQuery(id+"F6.wireOp",EDGE,"E21.4.6.5"),sQuery(id+"F6.wireOp",EDGE,"E21.4.6.6"),sQuery(id+"F6.wireOp",EDGE,"E21.4.6.7")])],"isStart":true});
            var Q57;
            Q57=makeQuery(id+"F7.opExtrude","CAP_FACE",FACE,{"disambiguationData":[OSD([sQuery(id+"F6.wireOp",EDGE,"E21.4.7.0"),sQuery(id+"F6.wireOp",EDGE,"E21.4.7.1"),sQuery(id+"F6.wireOp",EDGE,"E21.4.7.2"),sQuery(id+"F6.wireOp",EDGE,"E21.4.7.3"),sQuery(id+"F6.wireOp",EDGE,"E21.4.7.4"),sQuery(id+"F6.wireOp",EDGE,"E21.4.7.5"),sQuery(id+"F6.wireOp",EDGE,"E21.4.7.6"),sQuery(id+"F6.wireOp",EDGE,"E21.4.7.7")])],"isStart":true});
            var Q58;
            Q58=makeQuery(id+"F7.opExtrude","CAP_FACE",FACE,{"disambiguationData":[OSD([sQuery(id+"F6.wireOp",EDGE,"E21.5.7.0"),sQuery(id+"F6.wireOp",EDGE,"E21.5.7.1"),sQuery(id+"F6.wireOp",EDGE,"E21.5.7.2"),sQuery(id+"F6.wireOp",EDGE,"E21.5.7.3"),sQuery(id+"F6.wireOp",EDGE,"E21.5.7.4"),sQuery(id+"F6.wireOp",EDGE,"E21.5.7.5"),sQuery(id+"F6.wireOp",EDGE,"E21.5.7.6"),sQuery(id+"F6.wireOp",EDGE,"E21.5.7.7")])],"isStart":true});
            var Q59;
            Q59=makeQuery(id+"F7.opExtrude","CAP_FACE",FACE,{"disambiguationData":[OSD([sQuery(id+"F6.wireOp",EDGE,"E21.5.6.0"),sQuery(id+"F6.wireOp",EDGE,"E21.5.6.1"),sQuery(id+"F6.wireOp",EDGE,"E21.5.6.2"),sQuery(id+"F6.wireOp",EDGE,"E21.5.6.3"),sQuery(id+"F6.wireOp",EDGE,"E21.5.6.4"),sQuery(id+"F6.wireOp",EDGE,"E21.5.6.5"),sQuery(id+"F6.wireOp",EDGE,"E21.5.6.6"),sQuery(id+"F6.wireOp",EDGE,"E21.5.6.7")])],"isStart":true});
            var Q60;
            Q60=makeQuery(id+"F7.opExtrude","CAP_FACE",FACE,{"disambiguationData":[OSD([sQuery(id+"F6.wireOp",EDGE,"E21.6.6.0"),sQuery(id+"F6.wireOp",EDGE,"E21.6.6.1"),sQuery(id+"F6.wireOp",EDGE,"E21.6.6.2"),sQuery(id+"F6.wireOp",EDGE,"E21.6.6.3"),sQuery(id+"F6.wireOp",EDGE,"E21.6.6.4"),sQuery(id+"F6.wireOp",EDGE,"E21.6.6.5"),sQuery(id+"F6.wireOp",EDGE,"E21.6.6.6"),sQuery(id+"F6.wireOp",EDGE,"E21.6.6.7")])],"isStart":true});
            var Q61;
            Q61=makeQuery(id+"F7.opExtrude","CAP_FACE",FACE,{"disambiguationData":[OSD([sQuery(id+"F6.wireOp",EDGE,"E21.6.7.0"),sQuery(id+"F6.wireOp",EDGE,"E21.6.7.1"),sQuery(id+"F6.wireOp",EDGE,"E21.6.7.2"),sQuery(id+"F6.wireOp",EDGE,"E21.6.7.3"),sQuery(id+"F6.wireOp",EDGE,"E21.6.7.4"),sQuery(id+"F6.wireOp",EDGE,"E21.6.7.5"),sQuery(id+"F6.wireOp",EDGE,"E21.6.7.6"),sQuery(id+"F6.wireOp",EDGE,"E21.6.7.7")])],"isStart":true});
            var Q62;
            Q62=makeQuery(id+"F7.opExtrude","CAP_FACE",FACE,{"disambiguationData":[OSD([sQuery(id+"F6.wireOp",EDGE,"E21.7.7.0"),sQuery(id+"F6.wireOp",EDGE,"E21.7.7.1"),sQuery(id+"F6.wireOp",EDGE,"E21.7.7.2"),sQuery(id+"F6.wireOp",EDGE,"E21.7.7.3"),sQuery(id+"F6.wireOp",EDGE,"E21.7.7.4"),sQuery(id+"F6.wireOp",EDGE,"E21.7.7.5"),sQuery(id+"F6.wireOp",EDGE,"E21.7.7.6"),sQuery(id+"F6.wireOp",EDGE,"E21.7.7.7")])],"isStart":true});
            var Q63;
            Q63=makeQuery(id+"F7.opExtrude","CAP_FACE",FACE,{"disambiguationData":[OSD([sQuery(id+"F6.wireOp",EDGE,"E21.7.6.0"),sQuery(id+"F6.wireOp",EDGE,"E21.7.6.1"),sQuery(id+"F6.wireOp",EDGE,"E21.7.6.2"),sQuery(id+"F6.wireOp",EDGE,"E21.7.6.3"),sQuery(id+"F6.wireOp",EDGE,"E21.7.6.4"),sQuery(id+"F6.wireOp",EDGE,"E21.7.6.5"),sQuery(id+"F6.wireOp",EDGE,"E21.7.6.6"),sQuery(id+"F6.wireOp",EDGE,"E21.7.6.7")])],"isStart":true});
            fillet(context, id + "F8", {"entities" : qUnion([Q0, Q1, Q2, Q3, Q4, Q5, Q6, Q7, Q8, Q9, Q10, Q11, Q12, Q13, Q14, Q15, Q16, Q17, Q18, Q19, Q20, Q21, Q22, Q23, Q24, Q25, Q26, Q27, Q28, Q29, Q30, Q31, Q32, Q33, Q34, Q35, Q36, Q37, Q38, Q39, Q40, Q41, Q42, Q43, Q44, Q45, Q46, Q47, Q48, Q49, Q50, Q51, Q52, Q53, Q54, Q55, Q56, Q57, Q58, Q59, Q60, Q61, Q62, Q63]), "radius" : 0.64 * mm, "tangentPropagation" : true, "allowEdgeOverflow" : false});
        }
        {
            var Q0;
            Q0=makeQuery(id+"F4.opExtrude","CAP_FACE",FACE,{"disambiguationData":[OSD([sQuery(id+"F3.wireOp",EDGE,"E14.0.0"),sQuery(id+"F3.wireOp",EDGE,"E14.0.1"),sQuery(id+"F3.wireOp",EDGE,"E14.0.2"),sQuery(id+"F3.wireOp",EDGE,"E14.0.3"),sQuery(id+"F3.wireOp",EDGE,"E14.0.4"),sQuery(id+"F3.wireOp",EDGE,"E14.0.5"),sQuery(id+"F3.wireOp",EDGE,"E13.0"),sQuery(id+"F3.wireOp",EDGE,"E14.0.7"),sQuery(id+"F3.wireOp",EDGE,"37720200-3e0b-494f-8942-b4e86ef1e2dd.0"),sQuery(id+"F3.wireOp",EDGE,"37720200-3e0b-494f-8942-b4e86ef1e2dd.1"),sQuery(id+"F3.wireOp",EDGE,"37720200-3e0b-494f-8942-b4e86ef1e2dd.2"),sQuery(id+"F3.wireOp",EDGE,"37720200-3e0b-494f-8942-b4e86ef1e2dd.3")])],"isStart":false});
            var sketch = newSketch(context, id + "F9", { "sketchPlane" : qUnion([Q0])});
            skPoint(sketch, "E22.0", {"position": v(0, 0) * mm});
            skArc(sketch, "E23.0.0", {"start": v(85.09, 82.55) * mm, "mid": v(84.35, 84.35) * mm, "end": v(82.55, 85.1) * mm});
            skLineSegment(sketch, "E23.0.1", {"start": v(82.55, 85.1) * mm, "end": v(-82.55, 85.1) * mm});
            skArc(sketch, "E23.0.2", {"start": v(-82.55, 85.1) * mm, "mid": v(-84.35, 84.35) * mm, "end": v(-85.1, 82.55) * mm});
            skLineSegment(sketch, "E23.0.3", {"start": v(-85.1, 82.55) * mm, "end": v(-85.1, -82.55) * mm});
            skArc(sketch, "E23.0.4", {"start": v(-85.1, -82.55) * mm, "mid": v(-84.35, -84.35) * mm, "end": v(-82.55, -85.1) * mm});
            skLineSegment(sketch, "E23.0.5", {"start": v(-82.55, -85.1) * mm, "end": v(82.55, -85.1) * mm});
            skArc(sketch, "E23.0.6", {"start": v(82.55, -85.1) * mm, "mid": v(84.35, -84.35) * mm, "end": v(85.1, -82.55) * mm});
            skLineSegment(sketch, "E23.0.7", {"start": v(85.1, -82.55) * mm, "end": v(85.09, 82.55) * mm});
            skSolve(sketch);
        }
        {
            var Q0;
            Q0 = qSketchRegion(id + "F9", true);
            extrude(context, id + "F10", {"entities" : qUnion([Q0]), "depth" : 6.35 * mm, "offsetDistance" : 25.4 * mm});
        }
        {
            var Q0;
            Q0=makeQuery(id+"F10.opExtrude","CAP_FACE",FACE,{"disambiguationData":[OSD([sQuery(id+"F9.wireOp",EDGE,"E23.0.0"),sQuery(id+"F9.wireOp",EDGE,"E23.0.1"),sQuery(id+"F9.wireOp",EDGE,"E23.0.2"),sQuery(id+"F9.wireOp",EDGE,"E23.0.3"),sQuery(id+"F9.wireOp",EDGE,"E23.0.4"),sQuery(id+"F9.wireOp",EDGE,"E23.0.5"),sQuery(id+"F9.wireOp",EDGE,"E23.0.6"),sQuery(id+"F9.wireOp",EDGE,"E23.0.7")])],"isStart":true});
            var sketch = newSketch(context, id + "F11", { "sketchPlane" : qUnion([Q0])});
            skLineSegment(sketch, "E24.bottom", {"start": v(81.92, 81.92) * mm, "end": v(-81.92, 81.92) * mm});
            skLineSegment(sketch, "E24.top", {"start": v(81.92, -81.92) * mm, "end": v(-81.92, -81.92) * mm});
            skLineSegment(sketch, "E24.left", {"start": v(81.92, 81.92) * mm, "end": v(81.92, -81.92) * mm});
            skLineSegment(sketch, "E24.right", {"start": v(-81.92, 81.92) * mm, "end": v(-81.92, -81.92) * mm});
            skPoint(sketch, "E24.middle", {"position": v(0, 0) * mm});
            skLineSegment(sketch, "E25.0", {"start": v(79.38, 79.38) * mm, "end": v(-79.38, 79.38) * mm});
            skLineSegment(sketch, "E25.1", {"start": v(79.38, 79.38) * mm, "end": v(79.38, -79.38) * mm});
            skLineSegment(sketch, "E25.2", {"start": v(79.38, -79.38) * mm, "end": v(-79.38, -79.38) * mm});
            skLineSegment(sketch, "E25.3", {"start": v(-79.38, 79.38) * mm, "end": v(-79.38, -79.38) * mm});
            skLineSegment(sketch, "E26.top", {"start": v(163.83, 163.83) * mm, "end": v(0, 163.83) * mm});
            skLineSegment(sketch, "E26.right", {"start": v(163.83, 0) * mm, "end": v(163.83, 163.83) * mm});
            skPoint(sketch, "E26.middle", {"position": v(81.92, 81.92) * mm});
            skLineSegment(sketch, "E27.bottom", {"start": v(1.27, -162.56) * mm, "end": v(162.56, -162.56) * mm});
            skLineSegment(sketch, "E27.right", {"start": v(162.56, -162.56) * mm, "end": v(162.56, -1.27) * mm});
            skPoint(sketch, "E27.middle", {"position": v(81.92, -81.92) * mm});
            skSolve(sketch);
        }
        {
            var Q0;
            Q0=makeQuery(id+"F11.imprint","IMPRINT",FACE,{"disambiguationData":[TD([[makeQuery(id+"F11.imprint","IMPRINT",EDGE,{"derivedFrom":sQuery(id+"F11.wireOp",EDGE,"E24.bottom")}),1.0]])]});
            extrude(context, id + "F12", {"entities" : qUnion([Q0]), "operationType" : NewBodyOperationType.ADD, "depth" : 12.7 * mm, "offsetDistance" : 25.4 * mm});
        }
        {
            var Q0;
            {var subQ0=sQuery(id+"F9.wireOp",EDGE,"E23.0.2");var subQ1=sQuery(id+"F9.wireOp",EDGE,"E23.0.7");var subQ2=sQuery(id+"F9.wireOp",EDGE,"E23.0.6");var subQ3=sQuery(id+"F9.wireOp",EDGE,"E23.0.5");var subQ4=sQuery(id+"F9.wireOp",EDGE,"E23.0.4");var subQ5=sQuery(id+"F9.wireOp",EDGE,"E23.0.0");var subQ6=sQuery(id+"F9.wireOp",EDGE,"E23.0.3");var subQ7=sQuery(id+"F9.wireOp",EDGE,"E23.0.1");Q0=makeQuery(id+"F12.boolean.opBoolean","SPLIT",FACE,{"disambiguationData":[TD([makeQuery(id+"F10.opExtrude","SWEPT_FACE",FACE,{"disambiguationData":[OSD([subQ5])]})])],"derivedFrom":makeQuery(id+"F10.opExtrude","CAP_FACE",FACE,{"disambiguationData":[OSD([subQ5,subQ7,subQ0,subQ6,subQ4,subQ3,subQ2,subQ1])],"isStart":true})});}
            fillet(context, id + "F13", {"entities" : qUnion([Q0]), "radius" : 0.25 * mm, "tangentPropagation" : true, "allowEdgeOverflow" : false});
        }
        {
            var Q0;
            Q0=makeQuery(id+"F4.boolean.opBoolean","MERGE",FACE,{"derivedFrom":[makeQuery(id+"F1.opExtrude","SWEPT_FACE",FACE,{"disambiguationData":[OSD([sQuery(id+"F0.wireOp",EDGE,"E0.bottom")])]}),makeQuery(id+"F4.opExtrude","SWEPT_FACE",FACE,{"disambiguationData":[OSD([sQuery(id+"F3.wireOp",EDGE,"E14.0.4")])]})]});
            var sketch = newSketch(context, id + "F14", { "sketchPlane" : qUnion([Q0])});
            skCircle(sketch, "E28", {"center": v(0, -15.87) * mm, "radius": 6.35 * mm});
            skPoint(sketch, "E28.centerSnap0", {"position": v(-82.55, -15.87) * mm});
            skCircle(sketch, "E29.1.0.0", {"center": v(-25.4, -15.74) * mm, "radius": 6.35 * mm});
            skLineSegment(sketch, "E29.direction1", {"start": v(0, -15.87) * mm, "end": v(-25.4, -15.74) * mm, "construction": true});
            skCircle(sketch, "E30.1.0.0", {"center": v(25.4, -15.87) * mm, "radius": 6.35 * mm});
            skLineSegment(sketch, "E30.direction1", {"start": v(0, -15.87) * mm, "end": v(25.4, -15.87) * mm, "construction": true});
            skCircle(sketch, "E31.0", {"center": v(25.4, -15.87) * mm, "radius": 6.6 * mm});
            skCircle(sketch, "E32.0", {"center": v(0, -15.87) * mm, "radius": 6.6 * mm});
            skCircle(sketch, "E33.0", {"center": v(-25.4, -15.74) * mm, "radius": 6.6 * mm});
            skSolve(sketch);
        }
        {
            var Q0;
            Q0=makeQuery(id+"F14.imprint","IMPRINT",FACE,{"disambiguationData":[TD([[makeQuery(id+"F14.imprint","IMPRINT",EDGE,{"derivedFrom":sQuery(id+"F14.wireOp",EDGE,"E28")}),-1.0]])]});
            var Q1;
            Q1=makeQuery(id+"F14.imprint","IMPRINT",FACE,{"disambiguationData":[TD([[makeQuery(id+"F14.imprint","IMPRINT",EDGE,{"derivedFrom":sQuery(id+"F14.wireOp",EDGE,"E29.1.0.0")}),-1.0]])]});
            var Q2;
            Q2=makeQuery(id+"F14.imprint","IMPRINT",FACE,{"disambiguationData":[TD([[makeQuery(id+"F14.imprint","IMPRINT",EDGE,{"derivedFrom":sQuery(id+"F14.wireOp",EDGE,"E30.1.0.0")}),-1.0]])]});
            extrude(context, id + "F15", {"entities" : qUnion([Q0, Q1, Q2]), "operationType" : NewBodyOperationType.REMOVE, "oppositeDirection" : true, "depth" : 12.7 * mm, "offsetDistance" : 25.4 * mm});
        }
        {
            var Q0;
            {var subQ3=sQuery(id+"F3.wireOp",EDGE,"E14.0.4");var subQ4=sQuery(id+"F0.wireOp",EDGE,"E1.filletArc");var subQ5=sQuery(id+"F0.wireOp",EDGE,"E0.bottom");Q0=makeQuery(id+"F15.boolean.opBoolean","SPLIT",FACE,{"disambiguationData":[TD([makeQuery(id+"F1.opExtrude","SWEPT_FACE",FACE,{"disambiguationData":[OSD([subQ4])]})])],"derivedFrom":makeQuery(id+"F4.boolean.opBoolean","MERGE",FACE,{"derivedFrom":[makeQuery(id+"F1.opExtrude","SWEPT_FACE",FACE,{"disambiguationData":[OSD([subQ5])]}),makeQuery(id+"F4.opExtrude","SWEPT_FACE",FACE,{"disambiguationData":[OSD([subQ3])]})]})});}
            var Q1;
            Q1=makeQuery(id+"F15.boolean.opBoolean","SPLIT",FACE,{"disambiguationData":[TD([makeQuery(id+"F15.opExtrude","SWEPT_FACE",FACE,{"disambiguationData":[OSD([sQuery(id+"F14.wireOp",EDGE,"E30.1.0.0")])]})])],"derivedFrom":makeQuery(id+"F4.boolean.opBoolean","MERGE",FACE,{"derivedFrom":[makeQuery(id+"F1.opExtrude","SWEPT_FACE",FACE,{"disambiguationData":[OSD([sQuery(id+"F0.wireOp",EDGE,"E0.bottom")])]}),makeQuery(id+"F4.opExtrude","SWEPT_FACE",FACE,{"disambiguationData":[OSD([sQuery(id+"F3.wireOp",EDGE,"E14.0.4")])]})]})});
            var Q2;
            Q2=makeQuery(id+"F15.boolean.opBoolean","SPLIT",FACE,{"disambiguationData":[TD([makeQuery(id+"F15.opExtrude","SWEPT_FACE",FACE,{"disambiguationData":[OSD([sQuery(id+"F14.wireOp",EDGE,"E28")])]})])],"derivedFrom":makeQuery(id+"F4.boolean.opBoolean","MERGE",FACE,{"derivedFrom":[makeQuery(id+"F1.opExtrude","SWEPT_FACE",FACE,{"disambiguationData":[OSD([sQuery(id+"F0.wireOp",EDGE,"E0.bottom")])]}),makeQuery(id+"F4.opExtrude","SWEPT_FACE",FACE,{"disambiguationData":[OSD([sQuery(id+"F3.wireOp",EDGE,"E14.0.4")])]})]})});
            var Q3;
            Q3=makeQuery(id+"F15.boolean.opBoolean","SPLIT",FACE,{"disambiguationData":[TD([makeQuery(id+"F15.opExtrude","SWEPT_FACE",FACE,{"disambiguationData":[OSD([sQuery(id+"F14.wireOp",EDGE,"E29.1.0.0")])]})])],"derivedFrom":makeQuery(id+"F4.boolean.opBoolean","MERGE",FACE,{"derivedFrom":[makeQuery(id+"F1.opExtrude","SWEPT_FACE",FACE,{"disambiguationData":[OSD([sQuery(id+"F0.wireOp",EDGE,"E0.bottom")])]}),makeQuery(id+"F4.opExtrude","SWEPT_FACE",FACE,{"disambiguationData":[OSD([sQuery(id+"F3.wireOp",EDGE,"E14.0.4")])]})]})});
            fillet(context, id + "F16", {"entities" : qUnion([Q0, Q1, Q2, Q3]), "radius" : 0.25 * mm, "tangentPropagation" : true, "allowEdgeOverflow" : false});
        }
    });
